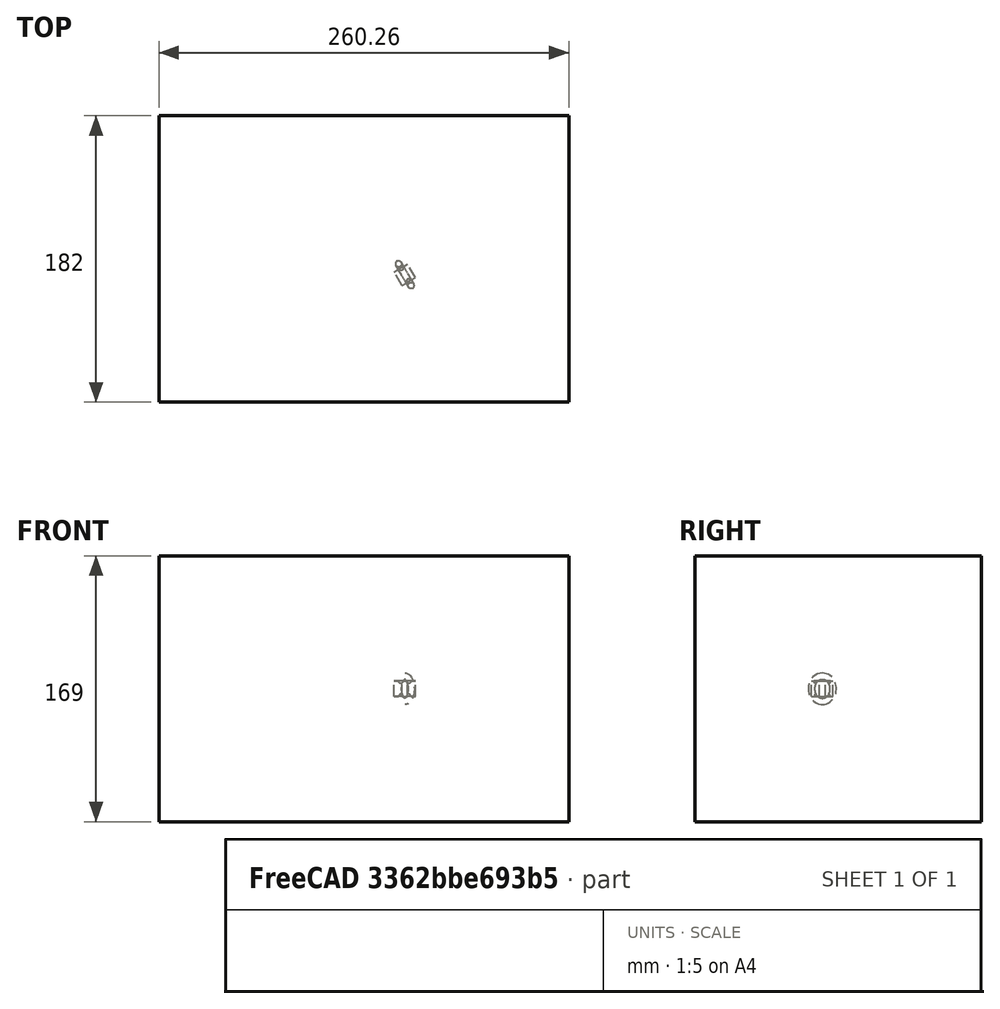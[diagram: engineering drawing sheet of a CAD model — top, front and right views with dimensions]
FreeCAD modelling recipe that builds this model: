
FCSTD DOCUMENT  (FreeCAD 0.21R33694 (Git))
Label: polarArray-7-Base-rotated-translated
License: All rights reserved
objects: App::DocumentObjectGroupPython×1251, Part::FeaturePython×4, App::Part×2, Part::MultiFuse×1
note: 4 computed .brp shape members not serialized (recipe doc carries the construction recipe); baked Part::Feature solids carry a one-line shape summary decoded from their .brp

FEATURE [App::DocumentObjectGroupPython] HALFPI  # scripted group (container) (typed FeaturePython)
  name = HALFPI
  value = pi/2.
FEATURE [App::DocumentObjectGroupPython] PI  # scripted group (container) (typed FeaturePython)
  name = PI
  value = 1.*pi
FEATURE [App::DocumentObjectGroupPython] TWOPI  # scripted group (container) (typed FeaturePython)
  name = TWOPI
  value = 2.*pi
FEATURE [App::DocumentObjectGroupPython] Constants  # scripted group (container) (typed FeaturePython)
  Group = -> [HALFPI,PI,TWOPI]
FEATURE [App::DocumentObjectGroupPython] Variables  # scripted group (container) (typed FeaturePython)
FEATURE [App::DocumentObjectGroupPython] Quantities  # scripted group (container) (typed FeaturePython)
FEATURE [App::DocumentObjectGroupPython] Isotopes  # scripted group (container) (typed FeaturePython)
FEATURE [App::DocumentObjectGroupPython] Elements  # scripted group (container) (typed FeaturePython)
FEATURE [App::DocumentObjectGroupPython] Matrix  # scripted group (container) (typed FeaturePython)
FEATURE [App::DocumentObjectGroupPython] Surfaces  # scripted group (container) (typed FeaturePython)
FEATURE [App::DocumentObjectGroupPython] Opticals  # scripted group (container) (typed FeaturePython)
  Group = -> [Matrix,Surfaces]
FEATURE [App::DocumentObjectGroupPython] G4Isotopes  # scripted group (container) (typed FeaturePython)
FEATURE [App::DocumentObjectGroupPython] H_element  # scripted group (container) (typed FeaturePython)
  Z = 1
  atom_value = 1.008
  formula = H
  name = H_element
FEATURE [App::DocumentObjectGroupPython] He_element  # scripted group (container) (typed FeaturePython)
  Z = 2
  atom_value = 4.0026
  formula = He
  name = He_element
FEATURE [App::DocumentObjectGroupPython] Li_element  # scripted group (container) (typed FeaturePython)
  Z = 3
  atom_value = 6.94
  formula = Li
  name = Li_element
FEATURE [App::DocumentObjectGroupPython] Be_element  # scripted group (container) (typed FeaturePython)
  Z = 4
  atom_value = 9.01218
  formula = Be
  name = Be_element
FEATURE [App::DocumentObjectGroupPython] B_element  # scripted group (container) (typed FeaturePython)
  Z = 5
  atom_value = 10.81
  formula = B
  name = B_element
FEATURE [App::DocumentObjectGroupPython] C_element  # scripted group (container) (typed FeaturePython)
  Z = 6
  atom_value = 12.011
  formula = C
  name = C_element
FEATURE [App::DocumentObjectGroupPython] N_element  # scripted group (container) (typed FeaturePython)
  Z = 7
  atom_value = 14.007
  formula = N
  name = N_element
FEATURE [App::DocumentObjectGroupPython] O_element  # scripted group (container) (typed FeaturePython)
  Z = 8
  atom_value = 15.999
  formula = O
  name = O_element
FEATURE [App::DocumentObjectGroupPython] F_element  # scripted group (container) (typed FeaturePython)
  Z = 9
  atom_value = 18.9984
  formula = F
  name = F_element
FEATURE [App::DocumentObjectGroupPython] Ne_element  # scripted group (container) (typed FeaturePython)
  Z = 10
  atom_value = 20.1797
  formula = Ne
  name = Ne_element
FEATURE [App::DocumentObjectGroupPython] Na_element  # scripted group (container) (typed FeaturePython)
  Z = 11
  atom_value = 22.9898
  formula = Na
  name = Na_element
FEATURE [App::DocumentObjectGroupPython] Mg_element  # scripted group (container) (typed FeaturePython)
  Z = 12
  atom_value = 24.305
  formula = Mg
  name = Mg_element
FEATURE [App::DocumentObjectGroupPython] Al_element  # scripted group (container) (typed FeaturePython)
  Z = 13
  atom_value = 26.9815
  formula = Al
  name = Al_element
FEATURE [App::DocumentObjectGroupPython] Si_element  # scripted group (container) (typed FeaturePython)
  Z = 14
  atom_value = 28.085
  formula = Si
  name = Si_element
FEATURE [App::DocumentObjectGroupPython] P_element  # scripted group (container) (typed FeaturePython)
  Z = 15
  atom_value = 30.9738
  formula = P
  name = P_element
FEATURE [App::DocumentObjectGroupPython] S_element  # scripted group (container) (typed FeaturePython)
  Z = 16
  atom_value = 32.06
  formula = S
  name = S_element
FEATURE [App::DocumentObjectGroupPython] Cl_element  # scripted group (container) (typed FeaturePython)
  Z = 17
  atom_value = 35.45
  formula = Cl
  name = Cl_element
FEATURE [App::DocumentObjectGroupPython] Ar_element  # scripted group (container) (typed FeaturePython)
  Z = 18
  atom_value = 39.95
  formula = Ar
  name = Ar_element
FEATURE [App::DocumentObjectGroupPython] K_element  # scripted group (container) (typed FeaturePython)
  Z = 19
  atom_value = 39.0983
  formula = K
  name = K_element
FEATURE [App::DocumentObjectGroupPython] Ca_element  # scripted group (container) (typed FeaturePython)
  Z = 20
  atom_value = 40.078
  formula = Ca
  name = Ca_element
FEATURE [App::DocumentObjectGroupPython] Sc_element  # scripted group (container) (typed FeaturePython)
  Z = 21
  atom_value = 44.9559
  formula = Sc
  name = Sc_element
FEATURE [App::DocumentObjectGroupPython] Ti_element  # scripted group (container) (typed FeaturePython)
  Z = 22
  atom_value = 47.867
  formula = Ti
  name = Ti_element
FEATURE [App::DocumentObjectGroupPython] V_element  # scripted group (container) (typed FeaturePython)
  Z = 23
  atom_value = 50.9415
  formula = V
  name = V_element
FEATURE [App::DocumentObjectGroupPython] Cr_element  # scripted group (container) (typed FeaturePython)
  Z = 24
  atom_value = 51.9961
  formula = Cr
  name = Cr_element
FEATURE [App::DocumentObjectGroupPython] Mn_element  # scripted group (container) (typed FeaturePython)
  Z = 25
  atom_value = 54.938
  formula = Mn
  name = Mn_element
FEATURE [App::DocumentObjectGroupPython] Fe_element  # scripted group (container) (typed FeaturePython)
  Z = 26
  atom_value = 55.845
  formula = Fe
  name = Fe_element
FEATURE [App::DocumentObjectGroupPython] Co_element  # scripted group (container) (typed FeaturePython)
  Z = 27
  atom_value = 58.9332
  formula = Co
  name = Co_element
FEATURE [App::DocumentObjectGroupPython] Ni_element  # scripted group (container) (typed FeaturePython)
  Z = 28
  atom_value = 58.6934
  formula = Ni
  name = Ni_element
FEATURE [App::DocumentObjectGroupPython] Cu_element  # scripted group (container) (typed FeaturePython)
  Z = 29
  atom_value = 63.546
  formula = Cu
  name = Cu_element
FEATURE [App::DocumentObjectGroupPython] Zn_element  # scripted group (container) (typed FeaturePython)
  Z = 30
  atom_value = 65.38
  formula = Zn
  name = Zn_element
FEATURE [App::DocumentObjectGroupPython] Ga_element  # scripted group (container) (typed FeaturePython)
  Z = 31
  atom_value = 69.723
  formula = Ga
  name = Ga_element
FEATURE [App::DocumentObjectGroupPython] Ge_element  # scripted group (container) (typed FeaturePython)
  Z = 32
  atom_value = 72.63
  formula = Ge
  name = Ge_element
FEATURE [App::DocumentObjectGroupPython] As_element  # scripted group (container) (typed FeaturePython)
  Z = 33
  atom_value = 74.9216
  formula = As
  name = As_element
FEATURE [App::DocumentObjectGroupPython] Se_element  # scripted group (container) (typed FeaturePython)
  Z = 34
  atom_value = 78.971
  formula = Se
  name = Se_element
FEATURE [App::DocumentObjectGroupPython] Br_element  # scripted group (container) (typed FeaturePython)
  Z = 35
  atom_value = 79.904
  formula = Br
  name = Br_element
FEATURE [App::DocumentObjectGroupPython] Kr_element  # scripted group (container) (typed FeaturePython)
  Z = 36
  atom_value = 83.798
  formula = Kr
  name = Kr_element
FEATURE [App::DocumentObjectGroupPython] Rb_element  # scripted group (container) (typed FeaturePython)
  Z = 37
  atom_value = 85.4678
  formula = Rb
  name = Rb_element
FEATURE [App::DocumentObjectGroupPython] Sr_element  # scripted group (container) (typed FeaturePython)
  Z = 38
  atom_value = 87.62
  formula = Sr
  name = Sr_element
FEATURE [App::DocumentObjectGroupPython] Y_element  # scripted group (container) (typed FeaturePython)
  Z = 39
  atom_value = 88.9058
  formula = Y
  name = Y_element
FEATURE [App::DocumentObjectGroupPython] Zr_element  # scripted group (container) (typed FeaturePython)
  Z = 40
  atom_value = 91.224
  formula = Zr
  name = Zr_element
FEATURE [App::DocumentObjectGroupPython] Nb_element  # scripted group (container) (typed FeaturePython)
  Z = 41
  atom_value = 92.9064
  formula = Nb
  name = Nb_element
FEATURE [App::DocumentObjectGroupPython] Mo_element  # scripted group (container) (typed FeaturePython)
  Z = 42
  atom_value = 95.95
  formula = Mo
  name = Mo_element
FEATURE [App::DocumentObjectGroupPython] Tc_element  # scripted group (container) (typed FeaturePython)
  Z = 43
  atom_value = 97
  formula = Tc
  name = Tc_element
FEATURE [App::DocumentObjectGroupPython] Ru_element  # scripted group (container) (typed FeaturePython)
  Z = 44
  atom_value = 101.07
  formula = Ru
  name = Ru_element
FEATURE [App::DocumentObjectGroupPython] Rh_element  # scripted group (container) (typed FeaturePython)
  Z = 45
  atom_value = 102.905
  formula = Rh
  name = Rh_element
FEATURE [App::DocumentObjectGroupPython] Pd_element  # scripted group (container) (typed FeaturePython)
  Z = 46
  atom_value = 106.42
  formula = Pd
  name = Pd_element
FEATURE [App::DocumentObjectGroupPython] Ag_element  # scripted group (container) (typed FeaturePython)
  Z = 47
  atom_value = 107.868
  formula = Ag
  name = Ag_element
FEATURE [App::DocumentObjectGroupPython] Cd_element  # scripted group (container) (typed FeaturePython)
  Z = 48
  atom_value = 112.414
  formula = Cd
  name = Cd_element
FEATURE [App::DocumentObjectGroupPython] In_element  # scripted group (container) (typed FeaturePython)
  Z = 49
  atom_value = 114.818
  formula = In
  name = In_element
FEATURE [App::DocumentObjectGroupPython] Sn_element  # scripted group (container) (typed FeaturePython)
  Z = 50
  atom_value = 118.71
  formula = Sn
  name = Sn_element
FEATURE [App::DocumentObjectGroupPython] Sb_element  # scripted group (container) (typed FeaturePython)
  Z = 51
  atom_value = 121.76
  formula = Sb
  name = Sb_element
FEATURE [App::DocumentObjectGroupPython] Te_element  # scripted group (container) (typed FeaturePython)
  Z = 52
  atom_value = 127.6
  formula = Te
  name = Te_element
FEATURE [App::DocumentObjectGroupPython] I_element  # scripted group (container) (typed FeaturePython)
  Z = 53
  atom_value = 126.904
  formula = I
  name = I_element
FEATURE [App::DocumentObjectGroupPython] Xe_element  # scripted group (container) (typed FeaturePython)
  Z = 54
  atom_value = 131.293
  formula = Xe
  name = Xe_element
FEATURE [App::DocumentObjectGroupPython] Cs_element  # scripted group (container) (typed FeaturePython)
  Z = 55
  atom_value = 132.905
  formula = Cs
  name = Cs_element
FEATURE [App::DocumentObjectGroupPython] Ba_element  # scripted group (container) (typed FeaturePython)
  Z = 56
  atom_value = 137.327
  formula = Ba
  name = Ba_element
FEATURE [App::DocumentObjectGroupPython] La_element  # scripted group (container) (typed FeaturePython)
  Z = 57
  atom_value = 138.905
  formula = La
  name = La_element
FEATURE [App::DocumentObjectGroupPython] Ce_element  # scripted group (container) (typed FeaturePython)
  Z = 58
  atom_value = 140.116
  formula = Ce
  name = Ce_element
FEATURE [App::DocumentObjectGroupPython] Pr_element  # scripted group (container) (typed FeaturePython)
  Z = 59
  atom_value = 140.908
  formula = Pr
  name = Pr_element
FEATURE [App::DocumentObjectGroupPython] Nd_element  # scripted group (container) (typed FeaturePython)
  Z = 60
  atom_value = 144.242
  formula = Nd
  name = Nd_element
FEATURE [App::DocumentObjectGroupPython] Pm_element  # scripted group (container) (typed FeaturePython)
  Z = 61
  atom_value = 145
  formula = Pm
  name = Pm_element
FEATURE [App::DocumentObjectGroupPython] Sm_element  # scripted group (container) (typed FeaturePython)
  Z = 62
  atom_value = 150.36
  formula = Sm
  name = Sm_element
FEATURE [App::DocumentObjectGroupPython] Eu_element  # scripted group (container) (typed FeaturePython)
  Z = 63
  atom_value = 151.964
  formula = Eu
  name = Eu_element
FEATURE [App::DocumentObjectGroupPython] Gd_element  # scripted group (container) (typed FeaturePython)
  Z = 64
  atom_value = 157.25
  formula = Gd
  name = Gd_element
FEATURE [App::DocumentObjectGroupPython] Tb_element  # scripted group (container) (typed FeaturePython)
  Z = 65
  atom_value = 158.925
  formula = Tb
  name = Tb_element
FEATURE [App::DocumentObjectGroupPython] Dy_element  # scripted group (container) (typed FeaturePython)
  Z = 66
  atom_value = 162.5
  formula = Dy
  name = Dy_element
FEATURE [App::DocumentObjectGroupPython] Ho_element  # scripted group (container) (typed FeaturePython)
  Z = 67
  atom_value = 164.93
  formula = Ho
  name = Ho_element
FEATURE [App::DocumentObjectGroupPython] Er_element  # scripted group (container) (typed FeaturePython)
  Z = 68
  atom_value = 167.259
  formula = Er
  name = Er_element
FEATURE [App::DocumentObjectGroupPython] Tm_element  # scripted group (container) (typed FeaturePython)
  Z = 69
  atom_value = 168.934
  formula = Tm
  name = Tm_element
FEATURE [App::DocumentObjectGroupPython] Yb_element  # scripted group (container) (typed FeaturePython)
  Z = 70
  atom_value = 173.045
  formula = Yb
  name = Yb_element
FEATURE [App::DocumentObjectGroupPython] Lu_element  # scripted group (container) (typed FeaturePython)
  Z = 71
  atom_value = 174.967
  formula = Lu
  name = Lu_element
FEATURE [App::DocumentObjectGroupPython] Hf_element  # scripted group (container) (typed FeaturePython)
  Z = 72
  atom_value = 178.49
  formula = Hf
  name = Hf_element
FEATURE [App::DocumentObjectGroupPython] Ta_element  # scripted group (container) (typed FeaturePython)
  Z = 73
  atom_value = 180.948
  formula = Ta
  name = Ta_element
FEATURE [App::DocumentObjectGroupPython] W_element  # scripted group (container) (typed FeaturePython)
  Z = 74
  atom_value = 183.84
  formula = W
  name = W_element
FEATURE [App::DocumentObjectGroupPython] Re_element  # scripted group (container) (typed FeaturePython)
  Z = 75
  atom_value = 186.207
  formula = Re
  name = Re_element
FEATURE [App::DocumentObjectGroupPython] Os_element  # scripted group (container) (typed FeaturePython)
  Z = 76
  atom_value = 190.23
  formula = Os
  name = Os_element
FEATURE [App::DocumentObjectGroupPython] Ir_element  # scripted group (container) (typed FeaturePython)
  Z = 77
  atom_value = 192.217
  formula = Ir
  name = Ir_element
FEATURE [App::DocumentObjectGroupPython] Pt_element  # scripted group (container) (typed FeaturePython)
  Z = 78
  atom_value = 195.084
  formula = Pt
  name = Pt_element
FEATURE [App::DocumentObjectGroupPython] Au_element  # scripted group (container) (typed FeaturePython)
  Z = 79
  atom_value = 196.967
  formula = Au
  name = Au_element
FEATURE [App::DocumentObjectGroupPython] Hg_element  # scripted group (container) (typed FeaturePython)
  Z = 80
  atom_value = 200.592
  formula = Hg
  name = Hg_element
FEATURE [App::DocumentObjectGroupPython] Tl_element  # scripted group (container) (typed FeaturePython)
  Z = 81
  atom_value = 204.38
  formula = Tl
  name = Tl_element
FEATURE [App::DocumentObjectGroupPython] Pb_element  # scripted group (container) (typed FeaturePython)
  Z = 82
  atom_value = 207.2
  formula = Pb
  name = Pb_element
FEATURE [App::DocumentObjectGroupPython] Bi_element  # scripted group (container) (typed FeaturePython)
  Z = 83
  atom_value = 208.98
  formula = Bi
  name = Bi_element
FEATURE [App::DocumentObjectGroupPython] Po_element  # scripted group (container) (typed FeaturePython)
  Z = 84
  atom_value = 209
  formula = Po
  name = Po_element
FEATURE [App::DocumentObjectGroupPython] At_element  # scripted group (container) (typed FeaturePython)
  Z = 85
  atom_value = 210
  formula = At
  name = At_element
FEATURE [App::DocumentObjectGroupPython] Rn_element  # scripted group (container) (typed FeaturePython)
  Z = 86
  atom_value = 222
  formula = Rn
  name = Rn_element
FEATURE [App::DocumentObjectGroupPython] Fr_element  # scripted group (container) (typed FeaturePython)
  Z = 87
  atom_value = 223
  formula = Fr
  name = Fr_element
FEATURE [App::DocumentObjectGroupPython] Ra_element  # scripted group (container) (typed FeaturePython)
  Z = 88
  atom_value = 226
  formula = Ra
  name = Ra_element
FEATURE [App::DocumentObjectGroupPython] Ac_element  # scripted group (container) (typed FeaturePython)
  Z = 89
  atom_value = 227
  formula = Ac
  name = Ac_element
FEATURE [App::DocumentObjectGroupPython] Th_element  # scripted group (container) (typed FeaturePython)
  Z = 90
  atom_value = 232.038
  formula = Th
  name = Th_element
FEATURE [App::DocumentObjectGroupPython] Pa_element  # scripted group (container) (typed FeaturePython)
  Z = 91
  atom_value = 231.036
  formula = Pa
  name = Pa_element
FEATURE [App::DocumentObjectGroupPython] U_element  # scripted group (container) (typed FeaturePython)
  Z = 92
  atom_value = 238.029
  formula = U
  name = U_element
FEATURE [App::DocumentObjectGroupPython] Np_element  # scripted group (container) (typed FeaturePython)
  Z = 93
  atom_value = 237
  formula = Np
  name = Np_element
FEATURE [App::DocumentObjectGroupPython] Pu_element  # scripted group (container) (typed FeaturePython)
  Z = 94
  atom_value = 244
  formula = Pu
  name = Pu_element
FEATURE [App::DocumentObjectGroupPython] Am_element  # scripted group (container) (typed FeaturePython)
  Z = 95
  atom_value = 243
  formula = Am
  name = Am_element
FEATURE [App::DocumentObjectGroupPython] Cm_element  # scripted group (container) (typed FeaturePython)
  Z = 96
  atom_value = 247
  formula = Cm
  name = Cm_element
FEATURE [App::DocumentObjectGroupPython] Bk_element  # scripted group (container) (typed FeaturePython)
  Z = 97
  atom_value = 247
  formula = Bk
  name = Bk_element
FEATURE [App::DocumentObjectGroupPython] Cf_element  # scripted group (container) (typed FeaturePython)
  Z = 98
  atom_value = 251
  formula = Cf
  name = Cf_element
FEATURE [App::DocumentObjectGroupPython] G4Elements  # scripted group (container) (typed FeaturePython)
  Group = -> [H_element,He_element,Li_element,Be_element,B_element,C_element,N_element,O_element,F_element,Ne_element,Na_element,Mg_element,Al_element,Si_element,P_element,S_element,Cl_element,Ar_element,K_element,Ca_element,Sc_element,Ti_element,V_element,Cr_element,Mn_element,Fe_element,Co_element,Ni_element,Cu_element,Zn_element,Ga_element,Ge_element,As_element,Se_element,Br_element,Kr_element,Rb_element,+61 more]
FEATURE [App::DocumentObjectGroupPython] H_element001  label="H_element : 0.101"  # scripted group (container) (typed FeaturePython)
  n = 0.101327
FEATURE [App::DocumentObjectGroupPython] C_element001  label="C_element : 0.775"  # scripted group (container) (typed FeaturePython)
  n = 0.7755
FEATURE [App::DocumentObjectGroupPython] N_element001  label="N_element : 0.035"  # scripted group (container) (typed FeaturePython)
  n = 0.035057
FEATURE [App::DocumentObjectGroupPython] O_element001  label="O_element : 0.052"  # scripted group (container) (typed FeaturePython)
  n = 0.0523159
FEATURE [App::DocumentObjectGroupPython] F_element001  label="F_element : 0.017"  # scripted group (container) (typed FeaturePython)
  n = 0.017422
FEATURE [App::DocumentObjectGroupPython] Ca_element001  label="Ca_element : 0.018"  # scripted group (container) (typed FeaturePython)
  n = 0.018378
FEATURE [App::DocumentObjectGroupPython] G4_A_150_TISSUE  label="G4_A-150_TISSUE"  # scripted group (container) (typed FeaturePython)
  Dunit = g/cm3
  Dvalue = 1.127
  Group = -> [H_element001,C_element001,N_element001,O_element001,F_element001,Ca_element001]
  conduct = 2
  density = 1
  expand = 3
  formula = G4_A-150_TISSUE
  name = G4_A-150_TISSUE
  specific = 4
FEATURE [App::DocumentObjectGroupPython] C_element002  label="C_element : 3"  # scripted group (container) (typed FeaturePython)
  n = 3
  ref = C_element
FEATURE [App::DocumentObjectGroupPython] H_element002  label="H_element : 6"  # scripted group (container) (typed FeaturePython)
  n = 6
  ref = H_element
FEATURE [App::DocumentObjectGroupPython] O_element002  label="O_element : 1"  # scripted group (container) (typed FeaturePython)
  n = 1
  ref = O_element
FEATURE [App::DocumentObjectGroupPython] G4_ACETONE  # scripted group (container) (typed FeaturePython)
  Dunit = g/cm3
  Dvalue = 0.7899
  Group = -> [C_element002,H_element002,O_element002]
  conduct = 2
  density = 1
  expand = 3
  formula = G4_ACETONE
  name = G4_ACETONE
  specific = 4
FEATURE [App::DocumentObjectGroupPython] C_element003  label="C_element : 2"  # scripted group (container) (typed FeaturePython)
  n = 2
  ref = C_element
FEATURE [App::DocumentObjectGroupPython] H_element003  label="H_element : 2"  # scripted group (container) (typed FeaturePython)
  n = 2
  ref = H_element
FEATURE [App::DocumentObjectGroupPython] G4_ACETYLENE  # scripted group (container) (typed FeaturePython)
  Dunit = g/cm3
  Dvalue = 0.0010967
  Group = -> [C_element003,H_element003]
  conduct = 2
  density = 1
  expand = 3
  formula = G4_ACETYLENE
  name = G4_ACETYLENE
  specific = 4
FEATURE [App::DocumentObjectGroupPython] C_element004  label="C_element : 5"  # scripted group (container) (typed FeaturePython)
  n = 5
  ref = C_element
FEATURE [App::DocumentObjectGroupPython] H_element004  label="H_element : 5"  # scripted group (container) (typed FeaturePython)
  n = 5
  ref = H_element
FEATURE [App::DocumentObjectGroupPython] N_element002  label="N_element : 5"  # scripted group (container) (typed FeaturePython)
  n = 5
  ref = N_element
FEATURE [App::DocumentObjectGroupPython] G4_ADENINE  # scripted group (container) (typed FeaturePython)
  Dunit = g/cm3
  Dvalue = 1.6
  Group = -> [C_element004,H_element004,N_element002]
  conduct = 2
  density = 1
  expand = 3
  formula = G4_ADENINE
  name = G4_ADENINE
  specific = 4
FEATURE [App::DocumentObjectGroupPython] H_element005  label="H_element : 0.114"  # scripted group (container) (typed FeaturePython)
  n = 0.114
FEATURE [App::DocumentObjectGroupPython] C_element005  label="C_element : 0.598"  # scripted group (container) (typed FeaturePython)
  n = 0.598
FEATURE [App::DocumentObjectGroupPython] N_element003  label="N_element : 0.007"  # scripted group (container) (typed FeaturePython)
  n = 0.007
FEATURE [App::DocumentObjectGroupPython] O_element003  label="O_element : 0.278"  # scripted group (container) (typed FeaturePython)
  n = 0.278
FEATURE [App::DocumentObjectGroupPython] Na_element001  label="Na_element : 0.001"  # scripted group (container) (typed FeaturePython)
  n = 0.001
FEATURE [App::DocumentObjectGroupPython] S_element001  label="S_element : 0.001"  # scripted group (container) (typed FeaturePython)
  n = 0.001
FEATURE [App::DocumentObjectGroupPython] Cl_element001  label="Cl_element : 0.001"  # scripted group (container) (typed FeaturePython)
  n = 0.001
FEATURE [App::DocumentObjectGroupPython] G4_ADIPOSE_TISSUE_ICRP  # scripted group (container) (typed FeaturePython)
  Dunit = g/cm3
  Dvalue = 0.95
  Group = -> [H_element005,C_element005,N_element003,O_element003,Na_element001,S_element001,Cl_element001]
  conduct = 2
  density = 1
  expand = 3
  formula = G4_ADIPOSE_TISSUE_ICRP
  name = G4_ADIPOSE_TISSUE_ICRP
  specific = 4
FEATURE [App::DocumentObjectGroupPython] C_element006  label="C_element : 0.000"  # scripted group (container) (typed FeaturePython)
  n = 0.000124
FEATURE [App::DocumentObjectGroupPython] N_element004  label="N_element : 0.755"  # scripted group (container) (typed FeaturePython)
  n = 0.755268
FEATURE [App::DocumentObjectGroupPython] O_element004  label="O_element : 0.232"  # scripted group (container) (typed FeaturePython)
  n = 0.231781
FEATURE [App::DocumentObjectGroupPython] Ar_element001  label="Ar_element : 0.013"  # scripted group (container) (typed FeaturePython)
  n = 0.012827
FEATURE [App::DocumentObjectGroupPython] G4_AIR  # scripted group (container) (typed FeaturePython)
  Dunit = g/cm3
  Dvalue = 0.00120479
  Group = -> [C_element006,N_element004,O_element004,Ar_element001]
  conduct = 2
  density = 1
  expand = 3
  formula = G4_AIR
  name = G4_AIR
  specific = 4
FEATURE [App::DocumentObjectGroupPython] C_element007  label="C_element : 006"  # scripted group (container) (typed FeaturePython)
  n = 3
  ref = C_element
FEATURE [App::DocumentObjectGroupPython] H_element006  label="H_element : 7"  # scripted group (container) (typed FeaturePython)
  n = 7
  ref = H_element
FEATURE [App::DocumentObjectGroupPython] N_element005  label="N_element : 1"  # scripted group (container) (typed FeaturePython)
  n = 1
  ref = N_element
FEATURE [App::DocumentObjectGroupPython] O_element005  label="O_element : 2"  # scripted group (container) (typed FeaturePython)
  n = 2
  ref = O_element
FEATURE [App::DocumentObjectGroupPython] G4_ALANINE  # scripted group (container) (typed FeaturePython)
  Dunit = g/cm3
  Dvalue = 1.42
  Group = -> [C_element007,H_element006,N_element005,O_element005]
  conduct = 2
  density = 1
  expand = 3
  formula = G4_ALANINE
  name = G4_ALANINE
  specific = 4
FEATURE [App::DocumentObjectGroupPython] Al_element001  label="Al_element : 2"  # scripted group (container) (typed FeaturePython)
  n = 2
  ref = Al_element
FEATURE [App::DocumentObjectGroupPython] O_element006  label="O_element : 3"  # scripted group (container) (typed FeaturePython)
  n = 3
  ref = O_element
FEATURE [App::DocumentObjectGroupPython] G4_ALUMINUM_OXIDE  # scripted group (container) (typed FeaturePython)
  Dunit = g/cm3
  Dvalue = 3.97
  Group = -> [Al_element001,O_element006]
  conduct = 2
  density = 1
  expand = 3
  formula = G4_ALUMINUM_OXIDE
  name = G4_ALUMINUM_OXIDE
  specific = 4
FEATURE [App::DocumentObjectGroupPython] H_element007  label="H_element : 0.106"  # scripted group (container) (typed FeaturePython)
  n = 0.10593
FEATURE [App::DocumentObjectGroupPython] C_element008  label="C_element : 0.789"  # scripted group (container) (typed FeaturePython)
  n = 0.788974
FEATURE [App::DocumentObjectGroupPython] O_element007  label="O_element : 0.105"  # scripted group (container) (typed FeaturePython)
  n = 0.105096
FEATURE [App::DocumentObjectGroupPython] G4_AMBER  # scripted group (container) (typed FeaturePython)
  Dunit = g/cm3
  Dvalue = 1.1
  Group = -> [H_element007,C_element008,O_element007]
  conduct = 2
  density = 1
  expand = 3
  formula = G4_AMBER
  name = G4_AMBER
  specific = 4
FEATURE [App::DocumentObjectGroupPython] N_element006  label="N_element : 006"  # scripted group (container) (typed FeaturePython)
  n = 1
  ref = N_element
FEATURE [App::DocumentObjectGroupPython] H_element008  label="H_element : 3"  # scripted group (container) (typed FeaturePython)
  n = 3
  ref = H_element
FEATURE [App::DocumentObjectGroupPython] G4_AMMONIA  # scripted group (container) (typed FeaturePython)
  Dunit = g/cm3
  Dvalue = 0.000826019
  Group = -> [N_element006,H_element008]
  conduct = 2
  density = 1
  expand = 3
  formula = G4_AMMONIA
  name = G4_AMMONIA
  specific = 4
FEATURE [App::DocumentObjectGroupPython] C_element009  label="C_element : 6"  # scripted group (container) (typed FeaturePython)
  n = 6
  ref = C_element
FEATURE [App::DocumentObjectGroupPython] H_element009  label="H_element : 008"  # scripted group (container) (typed FeaturePython)
  n = 7
  ref = H_element
FEATURE [App::DocumentObjectGroupPython] N_element007  label="N_element : 007"  # scripted group (container) (typed FeaturePython)
  n = 1
  ref = N_element
FEATURE [App::DocumentObjectGroupPython] G4_ANILINE  # scripted group (container) (typed FeaturePython)
  Dunit = g/cm3
  Dvalue = 1.0235
  Group = -> [C_element009,H_element009,N_element007]
  conduct = 2
  density = 1
  expand = 3
  formula = G4_ANILINE
  name = G4_ANILINE
  specific = 4
FEATURE [App::DocumentObjectGroupPython] C_element010  label="C_element : 14"  # scripted group (container) (typed FeaturePython)
  n = 14
  ref = C_element
FEATURE [App::DocumentObjectGroupPython] H_element010  label="H_element : 10"  # scripted group (container) (typed FeaturePython)
  n = 10
  ref = H_element
FEATURE [App::DocumentObjectGroupPython] G4_ANTHRACENE  # scripted group (container) (typed FeaturePython)
  Dunit = g/cm3
  Dvalue = 1.283
  Group = -> [C_element010,H_element010]
  conduct = 2
  density = 1
  expand = 3
  formula = G4_ANTHRACENE
  name = G4_ANTHRACENE
  specific = 4
FEATURE [App::DocumentObjectGroupPython] H_element011  label="H_element : 0.065"  # scripted group (container) (typed FeaturePython)
  n = 0.0654709
FEATURE [App::DocumentObjectGroupPython] C_element011  label="C_element : 0.537"  # scripted group (container) (typed FeaturePython)
  n = 0.536944
FEATURE [App::DocumentObjectGroupPython] N_element008  label="N_element : 0.021"  # scripted group (container) (typed FeaturePython)
  n = 0.0215
FEATURE [App::DocumentObjectGroupPython] O_element008  label="O_element : 0.032"  # scripted group (container) (typed FeaturePython)
  n = 0.032085
FEATURE [App::DocumentObjectGroupPython] F_element002  label="F_element : 0.167"  # scripted group (container) (typed FeaturePython)
  n = 0.167411
FEATURE [App::DocumentObjectGroupPython] Ca_element002  label="Ca_element : 0.177"  # scripted group (container) (typed FeaturePython)
  n = 0.176589
FEATURE [App::DocumentObjectGroupPython] G4_B_100_BONE  label="G4_B-100_BONE"  # scripted group (container) (typed FeaturePython)
  Dunit = g/cm3
  Dvalue = 1.45
  Group = -> [H_element011,C_element011,N_element008,O_element008,F_element002,Ca_element002]
  conduct = 2
  density = 1
  expand = 3
  formula = G4_B-100_BONE
  name = G4_B-100_BONE
  specific = 4
FEATURE [App::DocumentObjectGroupPython] H_element012  label="H_element : 0.057"  # scripted group (container) (typed FeaturePython)
  n = 0.057441
FEATURE [App::DocumentObjectGroupPython] C_element012  label="C_element : 0.790"  # scripted group (container) (typed FeaturePython)
  n = 0.774591
FEATURE [App::DocumentObjectGroupPython] O_element009  label="O_element : 0.168"  # scripted group (container) (typed FeaturePython)
  n = 0.167968
FEATURE [App::DocumentObjectGroupPython] G4_BAKELITE  # scripted group (container) (typed FeaturePython)
  Dunit = g/cm3
  Dvalue = 1.25
  Group = -> [H_element012,C_element012,O_element009]
  conduct = 2
  density = 1
  expand = 3
  formula = G4_BAKELITE
  name = G4_BAKELITE
  specific = 4
FEATURE [App::DocumentObjectGroupPython] Ba_element001  label="Ba_element : 1"  # scripted group (container) (typed FeaturePython)
  n = 1
  ref = Ba_element
FEATURE [App::DocumentObjectGroupPython] F_element003  label="F_element : 2"  # scripted group (container) (typed FeaturePython)
  n = 2
  ref = F_element
FEATURE [App::DocumentObjectGroupPython] G4_BARIUM_FLUORIDE  # scripted group (container) (typed FeaturePython)
  Dunit = g/cm3
  Dvalue = 4.89
  Group = -> [Ba_element001,F_element003]
  conduct = 2
  density = 1
  expand = 3
  formula = G4_BARIUM_FLUORIDE
  name = G4_BARIUM_FLUORIDE
  specific = 4
FEATURE [App::DocumentObjectGroupPython] Ba_element002  label="Ba_element : 002"  # scripted group (container) (typed FeaturePython)
  n = 1
  ref = Ba_element
FEATURE [App::DocumentObjectGroupPython] S_element002  label="S_element : 1"  # scripted group (container) (typed FeaturePython)
  n = 1
  ref = S_element
FEATURE [App::DocumentObjectGroupPython] O_element010  label="O_element : 4"  # scripted group (container) (typed FeaturePython)
  n = 4
  ref = O_element
FEATURE [App::DocumentObjectGroupPython] G4_BARIUM_SULFATE  # scripted group (container) (typed FeaturePython)
  Dunit = g/cm3
  Dvalue = 4.5
  Group = -> [Ba_element002,S_element002,O_element010]
  conduct = 2
  density = 1
  expand = 3
  formula = G4_BARIUM_SULFATE
  name = G4_BARIUM_SULFATE
  specific = 4
FEATURE [App::DocumentObjectGroupPython] C_element013  label="C_element : 007"  # scripted group (container) (typed FeaturePython)
  n = 6
  ref = C_element
FEATURE [App::DocumentObjectGroupPython] H_element013  label="H_element : 009"  # scripted group (container) (typed FeaturePython)
  n = 6
  ref = H_element
FEATURE [App::DocumentObjectGroupPython] G4_BENZENE  # scripted group (container) (typed FeaturePython)
  Dunit = g/cm3
  Dvalue = 0.87865
  Group = -> [C_element013,H_element013]
  conduct = 2
  density = 1
  expand = 3
  formula = G4_BENZENE
  name = G4_BENZENE
  specific = 4
FEATURE [App::DocumentObjectGroupPython] Be_element001  label="Be_element : 1"  # scripted group (container) (typed FeaturePython)
  n = 1
  ref = Be_element
FEATURE [App::DocumentObjectGroupPython] O_element011  label="O_element : 005"  # scripted group (container) (typed FeaturePython)
  n = 1
  ref = O_element
FEATURE [App::DocumentObjectGroupPython] G4_BERYLLIUM_OXIDE  # scripted group (container) (typed FeaturePython)
  Dunit = g/cm3
  Dvalue = 3.01
  Group = -> [Be_element001,O_element011]
  conduct = 2
  density = 1
  expand = 3
  formula = G4_BERYLLIUM_OXIDE
  name = G4_BERYLLIUM_OXIDE
  specific = 4
FEATURE [App::DocumentObjectGroupPython] Bi_element001  label="Bi_element : 4"  # scripted group (container) (typed FeaturePython)
  n = 4
  ref = Bi_element
FEATURE [App::DocumentObjectGroupPython] Ge_element001  label="Ge_element : 3"  # scripted group (container) (typed FeaturePython)
  n = 3
  ref = Ge_element
FEATURE [App::DocumentObjectGroupPython] O_element012  label="O_element : 12"  # scripted group (container) (typed FeaturePython)
  n = 12
  ref = O_element
FEATURE [App::DocumentObjectGroupPython] G4_BGO  # scripted group (container) (typed FeaturePython)
  Dunit = g/cm3
  Dvalue = 7.13
  Group = -> [Bi_element001,Ge_element001,O_element012]
  conduct = 2
  density = 1
  expand = 3
  formula = G4_BGO
  name = G4_BGO
  specific = 4
FEATURE [App::DocumentObjectGroupPython] H_element014  label="H_element : 0.102"  # scripted group (container) (typed FeaturePython)
  n = 0.102
FEATURE [App::DocumentObjectGroupPython] C_element014  label="C_element : 0.110"  # scripted group (container) (typed FeaturePython)
  n = 0.11
FEATURE [App::DocumentObjectGroupPython] N_element009  label="N_element : 0.033"  # scripted group (container) (typed FeaturePython)
  n = 0.033
FEATURE [App::DocumentObjectGroupPython] O_element013  label="O_element : 0.745"  # scripted group (container) (typed FeaturePython)
  n = 0.745
FEATURE [App::DocumentObjectGroupPython] Na_element002  label="Na_element : 0.002"  # scripted group (container) (typed FeaturePython)
  n = 0.001
FEATURE [App::DocumentObjectGroupPython] P_element001  label="P_element : 0.001"  # scripted group (container) (typed FeaturePython)
  n = 0.001
FEATURE [App::DocumentObjectGroupPython] S_element003  label="S_element : 0.002"  # scripted group (container) (typed FeaturePython)
  n = 0.002
FEATURE [App::DocumentObjectGroupPython] Cl_element002  label="Cl_element : 0.003"  # scripted group (container) (typed FeaturePython)
  n = 0.003
FEATURE [App::DocumentObjectGroupPython] K_element001  label="K_element : 0.002"  # scripted group (container) (typed FeaturePython)
  n = 0.002
FEATURE [App::DocumentObjectGroupPython] Fe_element001  label="Fe_element : 0.001"  # scripted group (container) (typed FeaturePython)
  n = 0.001
FEATURE [App::DocumentObjectGroupPython] G4_BLOOD_ICRP  # scripted group (container) (typed FeaturePython)
  Dunit = g/cm3
  Dvalue = 1.06
  Group = -> [H_element014,C_element014,N_element009,O_element013,Na_element002,P_element001,S_element003,Cl_element002,K_element001,Fe_element001]
  conduct = 2
  density = 1
  expand = 3
  formula = G4_BLOOD_ICRP
  name = G4_BLOOD_ICRP
  specific = 4
FEATURE [App::DocumentObjectGroupPython] H_element015  label="H_element : 0.064"  # scripted group (container) (typed FeaturePython)
  n = 0.064
FEATURE [App::DocumentObjectGroupPython] C_element015  label="C_element : 0.278"  # scripted group (container) (typed FeaturePython)
  n = 0.278
FEATURE [App::DocumentObjectGroupPython] N_element010  label="N_element : 0.027"  # scripted group (container) (typed FeaturePython)
  n = 0.027
FEATURE [App::DocumentObjectGroupPython] O_element014  label="O_element : 0.410"  # scripted group (container) (typed FeaturePython)
  n = 0.41
FEATURE [App::DocumentObjectGroupPython] Mg_element001  label="Mg_element : 0.002"  # scripted group (container) (typed FeaturePython)
  n = 0.002
FEATURE [App::DocumentObjectGroupPython] P_element002  label="P_element : 0.070"  # scripted group (container) (typed FeaturePython)
  n = 0.07
FEATURE [App::DocumentObjectGroupPython] S_element004  label="S_element : 0.003"  # scripted group (container) (typed FeaturePython)
  n = 0.002
FEATURE [App::DocumentObjectGroupPython] Ca_element003  label="Ca_element : 0.147"  # scripted group (container) (typed FeaturePython)
  n = 0.147
FEATURE [App::DocumentObjectGroupPython] G4_BONE_COMPACT_ICRU  # scripted group (container) (typed FeaturePython)
  Dunit = g/cm3
  Dvalue = 1.85
  Group = -> [H_element015,C_element015,N_element010,O_element014,Mg_element001,P_element002,S_element004,Ca_element003]
  conduct = 2
  density = 1
  expand = 3
  formula = G4_BONE_COMPACT_ICRU
  name = G4_BONE_COMPACT_ICRU
  specific = 4
FEATURE [App::DocumentObjectGroupPython] H_element016  label="H_element : 0.034"  # scripted group (container) (typed FeaturePython)
  n = 0.034
FEATURE [App::DocumentObjectGroupPython] C_element016  label="C_element : 0.155"  # scripted group (container) (typed FeaturePython)
  n = 0.155
FEATURE [App::DocumentObjectGroupPython] N_element011  label="N_element : 0.042"  # scripted group (container) (typed FeaturePython)
  n = 0.042
FEATURE [App::DocumentObjectGroupPython] O_element015  label="O_element : 0.435"  # scripted group (container) (typed FeaturePython)
  n = 0.435
FEATURE [App::DocumentObjectGroupPython] Na_element003  label="Na_element : 0.003"  # scripted group (container) (typed FeaturePython)
  n = 0.001
FEATURE [App::DocumentObjectGroupPython] Mg_element002  label="Mg_element : 0.003"  # scripted group (container) (typed FeaturePython)
  n = 0.002
FEATURE [App::DocumentObjectGroupPython] P_element003  label="P_element : 0.103"  # scripted group (container) (typed FeaturePython)
  n = 0.103
FEATURE [App::DocumentObjectGroupPython] S_element005  label="S_element : 0.004"  # scripted group (container) (typed FeaturePython)
  n = 0.003
FEATURE [App::DocumentObjectGroupPython] Ca_element004  label="Ca_element : 0.225"  # scripted group (container) (typed FeaturePython)
  n = 0.225
FEATURE [App::DocumentObjectGroupPython] G4_BONE_CORTICAL_ICRP  # scripted group (container) (typed FeaturePython)
  Dunit = g/cm3
  Dvalue = 1.92
  Group = -> [H_element016,C_element016,N_element011,O_element015,Na_element003,Mg_element002,P_element003,S_element005,Ca_element004]
  conduct = 2
  density = 1
  expand = 3
  formula = G4_BONE_CORTICAL_ICRP
  name = G4_BONE_CORTICAL_ICRP
  specific = 4
FEATURE [App::DocumentObjectGroupPython] B_element001  label="B_element : 4"  # scripted group (container) (typed FeaturePython)
  n = 4
  ref = B_element
FEATURE [App::DocumentObjectGroupPython] C_element017  label="C_element : 1"  # scripted group (container) (typed FeaturePython)
  n = 1
  ref = C_element
FEATURE [App::DocumentObjectGroupPython] G4_BORON_CARBIDE  # scripted group (container) (typed FeaturePython)
  Dunit = g/cm3
  Dvalue = 2.52
  Group = -> [B_element001,C_element017]
  conduct = 2
  density = 1
  expand = 3
  formula = G4_BORON_CARBIDE
  name = G4_BORON_CARBIDE
  specific = 4
FEATURE [App::DocumentObjectGroupPython] B_element002  label="B_element : 2"  # scripted group (container) (typed FeaturePython)
  n = 2
  ref = B_element
FEATURE [App::DocumentObjectGroupPython] O_element016  label="O_element : 006"  # scripted group (container) (typed FeaturePython)
  n = 3
  ref = O_element
FEATURE [App::DocumentObjectGroupPython] G4_BORON_OXIDE  # scripted group (container) (typed FeaturePython)
  Dunit = g/cm3
  Dvalue = 1.812
  Group = -> [B_element002,O_element016]
  conduct = 2
  density = 1
  expand = 3
  formula = G4_BORON_OXIDE
  name = G4_BORON_OXIDE
  specific = 4
FEATURE [App::DocumentObjectGroupPython] H_element017  label="H_element : 0.107"  # scripted group (container) (typed FeaturePython)
  n = 0.107
FEATURE [App::DocumentObjectGroupPython] C_element018  label="C_element : 0.145"  # scripted group (container) (typed FeaturePython)
  n = 0.145
FEATURE [App::DocumentObjectGroupPython] N_element012  label="N_element : 0.022"  # scripted group (container) (typed FeaturePython)
  n = 0.022
FEATURE [App::DocumentObjectGroupPython] O_element017  label="O_element : 0.712"  # scripted group (container) (typed FeaturePython)
  n = 0.712
FEATURE [App::DocumentObjectGroupPython] Na_element004  label="Na_element : 0.004"  # scripted group (container) (typed FeaturePython)
  n = 0.002
FEATURE [App::DocumentObjectGroupPython] P_element004  label="P_element : 0.004"  # scripted group (container) (typed FeaturePython)
  n = 0.004
FEATURE [App::DocumentObjectGroupPython] S_element006  label="S_element : 0.005"  # scripted group (container) (typed FeaturePython)
  n = 0.002
FEATURE [App::DocumentObjectGroupPython] Cl_element003  label="Cl_element : 0.004"  # scripted group (container) (typed FeaturePython)
  n = 0.003
FEATURE [App::DocumentObjectGroupPython] K_element002  label="K_element : 0.003"  # scripted group (container) (typed FeaturePython)
  n = 0.003
FEATURE [App::DocumentObjectGroupPython] G4_BRAIN_ICRP  # scripted group (container) (typed FeaturePython)
  Dunit = g/cm3
  Dvalue = 1.04
  Group = -> [H_element017,C_element018,N_element012,O_element017,Na_element004,P_element004,S_element006,Cl_element003,K_element002]
  conduct = 2
  density = 1
  expand = 3
  formula = G4_BRAIN_ICRP
  name = G4_BRAIN_ICRP
  specific = 4
FEATURE [App::DocumentObjectGroupPython] C_element019  label="C_element : 4"  # scripted group (container) (typed FeaturePython)
  n = 4
  ref = C_element
FEATURE [App::DocumentObjectGroupPython] H_element018  label="H_element : 010"  # scripted group (container) (typed FeaturePython)
  n = 10
  ref = H_element
FEATURE [App::DocumentObjectGroupPython] G4_BUTANE  # scripted group (container) (typed FeaturePython)
  Dunit = g/cm3
  Dvalue = 0.00249343
  Group = -> [C_element019,H_element018]
  conduct = 2
  density = 1
  expand = 3
  formula = G4_BUTANE
  name = G4_BUTANE
  specific = 4
FEATURE [App::DocumentObjectGroupPython] C_element020  label="C_element : 008"  # scripted group (container) (typed FeaturePython)
  n = 4
  ref = C_element
FEATURE [App::DocumentObjectGroupPython] H_element019  label="H_element : 011"  # scripted group (container) (typed FeaturePython)
  n = 10
  ref = H_element
FEATURE [App::DocumentObjectGroupPython] O_element018  label="O_element : 007"  # scripted group (container) (typed FeaturePython)
  n = 1
  ref = O_element
FEATURE [App::DocumentObjectGroupPython] G4_N_BUTYL_ALCOHOL  label="G4_N-BUTYL_ALCOHOL"  # scripted group (container) (typed FeaturePython)
  Dunit = g/cm3
  Dvalue = 0.8098
  Group = -> [C_element020,H_element019,O_element018]
  conduct = 2
  density = 1
  expand = 3
  formula = G4_N-BUTYL_ALCOHOL
  name = G4_N-BUTYL_ALCOHOL
  specific = 4
FEATURE [App::DocumentObjectGroupPython] H_element020  label="H_element : 0.025"  # scripted group (container) (typed FeaturePython)
  n = 0.02468
FEATURE [App::DocumentObjectGroupPython] C_element021  label="C_element : 0.502"  # scripted group (container) (typed FeaturePython)
  n = 0.501611
FEATURE [App::DocumentObjectGroupPython] O_element019  label="O_element : 0.005"  # scripted group (container) (typed FeaturePython)
  n = 0.004527
FEATURE [App::DocumentObjectGroupPython] F_element004  label="F_element : 0.465"  # scripted group (container) (typed FeaturePython)
  n = 0.465209
FEATURE [App::DocumentObjectGroupPython] Si_element001  label="Si_element : 0.004"  # scripted group (container) (typed FeaturePython)
  n = 0.003973
FEATURE [App::DocumentObjectGroupPython] G4_C_552  label="G4_C-552"  # scripted group (container) (typed FeaturePython)
  Dunit = g/cm3
  Dvalue = 1.76
  Group = -> [H_element020,C_element021,O_element019,F_element004,Si_element001]
  conduct = 2
  density = 1
  expand = 3
  formula = G4_C-552
  name = G4_C-552
  specific = 4
FEATURE [App::DocumentObjectGroupPython] Cd_element001  label="Cd_element : 1"  # scripted group (container) (typed FeaturePython)
  n = 1
  ref = Cd_element
FEATURE [App::DocumentObjectGroupPython] Te_element001  label="Te_element : 1"  # scripted group (container) (typed FeaturePython)
  n = 1
  ref = Te_element
FEATURE [App::DocumentObjectGroupPython] G4_CADMIUM_TELLURIDE  # scripted group (container) (typed FeaturePython)
  Dunit = g/cm3
  Dvalue = 6.2
  Group = -> [Cd_element001,Te_element001]
  conduct = 2
  density = 1
  expand = 3
  formula = G4_CADMIUM_TELLURIDE
  name = G4_CADMIUM_TELLURIDE
  specific = 4
FEATURE [App::DocumentObjectGroupPython] Cd_element002  label="Cd_element : 002"  # scripted group (container) (typed FeaturePython)
  n = 1
  ref = Cd_element
FEATURE [App::DocumentObjectGroupPython] W_element001  label="W_element : 1"  # scripted group (container) (typed FeaturePython)
  n = 1
  ref = W_element
FEATURE [App::DocumentObjectGroupPython] O_element020  label="O_element : 008"  # scripted group (container) (typed FeaturePython)
  n = 4
  ref = O_element
FEATURE [App::DocumentObjectGroupPython] G4_CADMIUM_TUNGSTATE  # scripted group (container) (typed FeaturePython)
  Dunit = g/cm3
  Dvalue = 7.9
  Group = -> [Cd_element002,W_element001,O_element020]
  conduct = 2
  density = 1
  expand = 3
  formula = G4_CADMIUM_TUNGSTATE
  name = G4_CADMIUM_TUNGSTATE
  specific = 4
FEATURE [App::DocumentObjectGroupPython] Ca_element005  label="Ca_element : 1"  # scripted group (container) (typed FeaturePython)
  n = 1
  ref = Ca_element
FEATURE [App::DocumentObjectGroupPython] C_element022  label="C_element : 009"  # scripted group (container) (typed FeaturePython)
  n = 1
  ref = C_element
FEATURE [App::DocumentObjectGroupPython] O_element021  label="O_element : 009"  # scripted group (container) (typed FeaturePython)
  n = 3
  ref = O_element
FEATURE [App::DocumentObjectGroupPython] G4_CALCIUM_CARBONATE  # scripted group (container) (typed FeaturePython)
  Dunit = g/cm3
  Dvalue = 2.8
  Group = -> [Ca_element005,C_element022,O_element021]
  conduct = 2
  density = 1
  expand = 3
  formula = G4_CALCIUM_CARBONATE
  name = G4_CALCIUM_CARBONATE
  specific = 4
FEATURE [App::DocumentObjectGroupPython] Ca_element006  label="Ca_element : 002"  # scripted group (container) (typed FeaturePython)
  n = 1
  ref = Ca_element
FEATURE [App::DocumentObjectGroupPython] F_element005  label="F_element : 003"  # scripted group (container) (typed FeaturePython)
  n = 2
  ref = F_element
FEATURE [App::DocumentObjectGroupPython] G4_CALCIUM_FLUORIDE  # scripted group (container) (typed FeaturePython)
  Dunit = g/cm3
  Dvalue = 3.18
  Group = -> [Ca_element006,F_element005]
  conduct = 2
  density = 1
  expand = 3
  formula = G4_CALCIUM_FLUORIDE
  name = G4_CALCIUM_FLUORIDE
  specific = 4
FEATURE [App::DocumentObjectGroupPython] Ca_element007  label="Ca_element : 003"  # scripted group (container) (typed FeaturePython)
  n = 1
  ref = Ca_element
FEATURE [App::DocumentObjectGroupPython] O_element022  label="O_element : 010"  # scripted group (container) (typed FeaturePython)
  n = 1
  ref = O_element
FEATURE [App::DocumentObjectGroupPython] G4_CALCIUM_OXIDE  # scripted group (container) (typed FeaturePython)
  Dunit = g/cm3
  Dvalue = 3.3
  Group = -> [Ca_element007,O_element022]
  conduct = 2
  density = 1
  expand = 3
  formula = G4_CALCIUM_OXIDE
  name = G4_CALCIUM_OXIDE
  specific = 4
FEATURE [App::DocumentObjectGroupPython] Ca_element008  label="Ca_element : 004"  # scripted group (container) (typed FeaturePython)
  n = 1
  ref = Ca_element
FEATURE [App::DocumentObjectGroupPython] S_element007  label="S_element : 002"  # scripted group (container) (typed FeaturePython)
  n = 1
  ref = S_element
FEATURE [App::DocumentObjectGroupPython] O_element023  label="O_element : 011"  # scripted group (container) (typed FeaturePython)
  n = 4
  ref = O_element
FEATURE [App::DocumentObjectGroupPython] G4_CALCIUM_SULFATE  # scripted group (container) (typed FeaturePython)
  Dunit = g/cm3
  Dvalue = 2.96
  Group = -> [Ca_element008,S_element007,O_element023]
  conduct = 2
  density = 1
  expand = 3
  formula = G4_CALCIUM_SULFATE
  name = G4_CALCIUM_SULFATE
  specific = 4
FEATURE [App::DocumentObjectGroupPython] Ca_element009  label="Ca_element : 005"  # scripted group (container) (typed FeaturePython)
  n = 1
  ref = Ca_element
FEATURE [App::DocumentObjectGroupPython] W_element002  label="W_element : 002"  # scripted group (container) (typed FeaturePython)
  n = 1
  ref = W_element
FEATURE [App::DocumentObjectGroupPython] O_element024  label="O_element : 012"  # scripted group (container) (typed FeaturePython)
  n = 4
  ref = O_element
FEATURE [App::DocumentObjectGroupPython] G4_CALCIUM_TUNGSTATE  # scripted group (container) (typed FeaturePython)
  Dunit = g/cm3
  Dvalue = 6.062
  Group = -> [Ca_element009,W_element002,O_element024]
  conduct = 2
  density = 1
  expand = 3
  formula = G4_CALCIUM_TUNGSTATE
  name = G4_CALCIUM_TUNGSTATE
  specific = 4
FEATURE [App::DocumentObjectGroupPython] C_element023  label="C_element : 010"  # scripted group (container) (typed FeaturePython)
  n = 1
  ref = C_element
FEATURE [App::DocumentObjectGroupPython] O_element025  label="O_element : 013"  # scripted group (container) (typed FeaturePython)
  n = 2
  ref = O_element
FEATURE [App::DocumentObjectGroupPython] G4_CARBON_DIOXIDE  # scripted group (container) (typed FeaturePython)
  Dunit = g/cm3
  Dvalue = 0.00184212
  Group = -> [C_element023,O_element025]
  conduct = 2
  density = 1
  expand = 3
  formula = G4_CARBON_DIOXIDE
  name = G4_CARBON_DIOXIDE
  specific = 4
FEATURE [App::DocumentObjectGroupPython] C_element024  label="C_element : 011"  # scripted group (container) (typed FeaturePython)
  n = 1
  ref = C_element
FEATURE [App::DocumentObjectGroupPython] Cl_element004  label="Cl_element : 4"  # scripted group (container) (typed FeaturePython)
  n = 4
  ref = Cl_element
FEATURE [App::DocumentObjectGroupPython] G4_CARBON_TETRACHLORIDE  # scripted group (container) (typed FeaturePython)
  Dunit = g/cm3
  Dvalue = 1.594
  Group = -> [C_element024,Cl_element004]
  conduct = 2
  density = 1
  expand = 3
  formula = G4_CARBON_TETRACHLORIDE
  name = G4_CARBON_TETRACHLORIDE
  specific = 4
FEATURE [App::DocumentObjectGroupPython] C_element025  label="C_element : 012"  # scripted group (container) (typed FeaturePython)
  n = 6
  ref = C_element
FEATURE [App::DocumentObjectGroupPython] H_element021  label="H_element : 012"  # scripted group (container) (typed FeaturePython)
  n = 10
  ref = H_element
FEATURE [App::DocumentObjectGroupPython] O_element026  label="O_element : 5"  # scripted group (container) (typed FeaturePython)
  n = 5
  ref = O_element
FEATURE [App::DocumentObjectGroupPython] G4_CELLULOSE_CELLOPHANE  # scripted group (container) (typed FeaturePython)
  Dunit = g/cm3
  Dvalue = 1.42
  Group = -> [C_element025,H_element021,O_element026]
  conduct = 2
  density = 1
  expand = 3
  formula = G4_CELLULOSE_CELLOPHANE
  name = G4_CELLULOSE_CELLOPHANE
  specific = 4
FEATURE [App::DocumentObjectGroupPython] H_element022  label="H_element : 0.067"  # scripted group (container) (typed FeaturePython)
  n = 0.067125
FEATURE [App::DocumentObjectGroupPython] C_element026  label="C_element : 0.545"  # scripted group (container) (typed FeaturePython)
  n = 0.545403
FEATURE [App::DocumentObjectGroupPython] O_element027  label="O_element : 0.387"  # scripted group (container) (typed FeaturePython)
  n = 0.387472
FEATURE [App::DocumentObjectGroupPython] G4_CELLULOSE_BUTYRATE  # scripted group (container) (typed FeaturePython)
  Dunit = g/cm3
  Dvalue = 1.2
  Group = -> [H_element022,C_element026,O_element027]
  conduct = 2
  density = 1
  expand = 3
  formula = G4_CELLULOSE_BUTYRATE
  name = G4_CELLULOSE_BUTYRATE
  specific = 4
FEATURE [App::DocumentObjectGroupPython] H_element023  label="H_element : 0.029"  # scripted group (container) (typed FeaturePython)
  n = 0.029216
FEATURE [App::DocumentObjectGroupPython] C_element027  label="C_element : 0.271"  # scripted group (container) (typed FeaturePython)
  n = 0.271296
FEATURE [App::DocumentObjectGroupPython] N_element013  label="N_element : 0.121"  # scripted group (container) (typed FeaturePython)
  n = 0.121276
FEATURE [App::DocumentObjectGroupPython] O_element028  label="O_element : 0.578"  # scripted group (container) (typed FeaturePython)
  n = 0.578212
FEATURE [App::DocumentObjectGroupPython] G4_CELLULOSE_NITRATE  # scripted group (container) (typed FeaturePython)
  Dunit = g/cm3
  Dvalue = 1.49
  Group = -> [H_element023,C_element027,N_element013,O_element028]
  conduct = 2
  density = 1
  expand = 3
  formula = G4_CELLULOSE_NITRATE
  name = G4_CELLULOSE_NITRATE
  specific = 4
FEATURE [App::DocumentObjectGroupPython] H_element024  label="H_element : 0.108"  # scripted group (container) (typed FeaturePython)
  n = 0.107596
FEATURE [App::DocumentObjectGroupPython] N_element014  label="N_element : 0.001"  # scripted group (container) (typed FeaturePython)
  n = 0.0008
FEATURE [App::DocumentObjectGroupPython] O_element029  label="O_element : 0.875"  # scripted group (container) (typed FeaturePython)
  n = 0.874976
FEATURE [App::DocumentObjectGroupPython] S_element008  label="S_element : 0.015"  # scripted group (container) (typed FeaturePython)
  n = 0.014627
FEATURE [App::DocumentObjectGroupPython] Ce_element001  label="Ce_element : 0.002"  # scripted group (container) (typed FeaturePython)
  n = 0.002001
FEATURE [App::DocumentObjectGroupPython] G4_CERIC_SULFATE  # scripted group (container) (typed FeaturePython)
  Dunit = g/cm3
  Dvalue = 1.03
  Group = -> [H_element024,N_element014,O_element029,S_element008,Ce_element001]
  conduct = 2
  density = 1
  expand = 3
  formula = G4_CERIC_SULFATE
  name = G4_CERIC_SULFATE
  specific = 4
FEATURE [App::DocumentObjectGroupPython] Cs_element001  label="Cs_element : 1"  # scripted group (container) (typed FeaturePython)
  n = 1
  ref = Cs_element
FEATURE [App::DocumentObjectGroupPython] F_element006  label="F_element : 1"  # scripted group (container) (typed FeaturePython)
  n = 1
  ref = F_element
FEATURE [App::DocumentObjectGroupPython] G4_CESIUM_FLUORIDE  # scripted group (container) (typed FeaturePython)
  Dunit = g/cm3
  Dvalue = 4.115
  Group = -> [Cs_element001,F_element006]
  conduct = 2
  density = 1
  expand = 3
  formula = G4_CESIUM_FLUORIDE
  name = G4_CESIUM_FLUORIDE
  specific = 4
FEATURE [App::DocumentObjectGroupPython] Cs_element002  label="Cs_element : 002"  # scripted group (container) (typed FeaturePython)
  n = 1
  ref = Cs_element
FEATURE [App::DocumentObjectGroupPython] I_element001  label="I_element : 1"  # scripted group (container) (typed FeaturePython)
  n = 1
  ref = I_element
FEATURE [App::DocumentObjectGroupPython] G4_CESIUM_IODIDE  # scripted group (container) (typed FeaturePython)
  Dunit = g/cm3
  Dvalue = 4.51
  Group = -> [Cs_element002,I_element001]
  conduct = 2
  density = 1
  expand = 3
  formula = G4_CESIUM_IODIDE
  name = G4_CESIUM_IODIDE
  specific = 4
FEATURE [App::DocumentObjectGroupPython] C_element028  label="C_element : 013"  # scripted group (container) (typed FeaturePython)
  n = 6
  ref = C_element
FEATURE [App::DocumentObjectGroupPython] H_element025  label="H_element : 013"  # scripted group (container) (typed FeaturePython)
  n = 5
  ref = H_element
FEATURE [App::DocumentObjectGroupPython] Cl_element005  label="Cl_element : 1"  # scripted group (container) (typed FeaturePython)
  n = 1
  ref = Cl_element
FEATURE [App::DocumentObjectGroupPython] G4_CHLOROBENZENE  # scripted group (container) (typed FeaturePython)
  Dunit = g/cm3
  Dvalue = 1.1058
  Group = -> [C_element028,H_element025,Cl_element005]
  conduct = 2
  density = 1
  expand = 3
  formula = G4_CHLOROBENZENE
  name = G4_CHLOROBENZENE
  specific = 4
FEATURE [App::DocumentObjectGroupPython] C_element029  label="C_element : 014"  # scripted group (container) (typed FeaturePython)
  n = 1
  ref = C_element
FEATURE [App::DocumentObjectGroupPython] H_element026  label="H_element : 1"  # scripted group (container) (typed FeaturePython)
  n = 1
  ref = H_element
FEATURE [App::DocumentObjectGroupPython] Cl_element006  label="Cl_element : 3"  # scripted group (container) (typed FeaturePython)
  n = 3
  ref = Cl_element
FEATURE [App::DocumentObjectGroupPython] G4_CHLOROFORM  # scripted group (container) (typed FeaturePython)
  Dunit = g/cm3
  Dvalue = 1.4832
  Group = -> [C_element029,H_element026,Cl_element006]
  conduct = 2
  density = 1
  expand = 3
  formula = G4_CHLOROFORM
  name = G4_CHLOROFORM
  specific = 4
FEATURE [App::DocumentObjectGroupPython] H_element027  label="H_element : 0.010"  # scripted group (container) (typed FeaturePython)
  n = 0.01
FEATURE [App::DocumentObjectGroupPython] C_element030  label="C_element : 0.001"  # scripted group (container) (typed FeaturePython)
  n = 0.001
FEATURE [App::DocumentObjectGroupPython] O_element030  label="O_element : 0.529"  # scripted group (container) (typed FeaturePython)
  n = 0.529107
FEATURE [App::DocumentObjectGroupPython] Na_element005  label="Na_element : 0.016"  # scripted group (container) (typed FeaturePython)
  n = 0.016
FEATURE [App::DocumentObjectGroupPython] Mg_element003  label="Mg_element : 0.004"  # scripted group (container) (typed FeaturePython)
  n = 0.002
FEATURE [App::DocumentObjectGroupPython] Al_element002  label="Al_element : 0.034"  # scripted group (container) (typed FeaturePython)
  n = 0.033872
FEATURE [App::DocumentObjectGroupPython] Si_element002  label="Si_element : 0.337"  # scripted group (container) (typed FeaturePython)
  n = 0.337021
FEATURE [App::DocumentObjectGroupPython] K_element003  label="K_element : 0.013"  # scripted group (container) (typed FeaturePython)
  n = 0.013
FEATURE [App::DocumentObjectGroupPython] Ca_element010  label="Ca_element : 0.044"  # scripted group (container) (typed FeaturePython)
  n = 0.044
FEATURE [App::DocumentObjectGroupPython] Fe_element002  label="Fe_element : 0.014"  # scripted group (container) (typed FeaturePython)
  n = 0.014
FEATURE [App::DocumentObjectGroupPython] G4_CONCRETE  # scripted group (container) (typed FeaturePython)
  Dunit = g/cm3
  Dvalue = 2.3
  Group = -> [H_element027,C_element030,O_element030,Na_element005,Mg_element003,Al_element002,Si_element002,K_element003,Ca_element010,Fe_element002]
  conduct = 2
  density = 1
  expand = 3
  formula = G4_CONCRETE
  name = G4_CONCRETE
  specific = 4
FEATURE [App::DocumentObjectGroupPython] C_element031  label="C_element : 015"  # scripted group (container) (typed FeaturePython)
  n = 6
  ref = C_element
FEATURE [App::DocumentObjectGroupPython] H_element028  label="H_element : 12"  # scripted group (container) (typed FeaturePython)
  n = 12
  ref = H_element
FEATURE [App::DocumentObjectGroupPython] G4_CYCLOHEXANE  # scripted group (container) (typed FeaturePython)
  Dunit = g/cm3
  Dvalue = 0.779
  Group = -> [C_element031,H_element028]
  conduct = 2
  density = 1
  expand = 3
  formula = G4_CYCLOHEXANE
  name = G4_CYCLOHEXANE
  specific = 4
FEATURE [App::DocumentObjectGroupPython] C_element032  label="C_element : 016"  # scripted group (container) (typed FeaturePython)
  n = 6
  ref = C_element
FEATURE [App::DocumentObjectGroupPython] H_element029  label="H_element : 4"  # scripted group (container) (typed FeaturePython)
  n = 4
  ref = H_element
FEATURE [App::DocumentObjectGroupPython] Cl_element007  label="Cl_element : 2"  # scripted group (container) (typed FeaturePython)
  n = 2
  ref = Cl_element
FEATURE [App::DocumentObjectGroupPython] G4_1_2_DICHLOROBENZENE  label="G4_1.2-DICHLOROBENZENE"  # scripted group (container) (typed FeaturePython)
  Dunit = g/cm3
  Dvalue = 1.3048
  Group = -> [C_element032,H_element029,Cl_element007]
  conduct = 2
  density = 1
  expand = 3
  formula = G4_1.2-DICHLOROBENZENE
  name = G4_1.2-DICHLOROBENZENE
  specific = 4
FEATURE [App::DocumentObjectGroupPython] C_element033  label="C_element : 017"  # scripted group (container) (typed FeaturePython)
  n = 4
  ref = C_element
FEATURE [App::DocumentObjectGroupPython] H_element030  label="H_element : 8"  # scripted group (container) (typed FeaturePython)
  n = 8
  ref = H_element
FEATURE [App::DocumentObjectGroupPython] O_element031  label="O_element : 014"  # scripted group (container) (typed FeaturePython)
  n = 1
  ref = O_element
FEATURE [App::DocumentObjectGroupPython] Cl_element008  label="Cl_element : 005"  # scripted group (container) (typed FeaturePython)
  n = 2
  ref = Cl_element
FEATURE [App::DocumentObjectGroupPython] G4_DICHLORODIETHYL_ETHER  # scripted group (container) (typed FeaturePython)
  Dunit = g/cm3
  Dvalue = 1.2199
  Group = -> [C_element033,H_element030,O_element031,Cl_element008]
  conduct = 2
  density = 1
  expand = 3
  formula = G4_DICHLORODIETHYL_ETHER
  name = G4_DICHLORODIETHYL_ETHER
  specific = 4
FEATURE [App::DocumentObjectGroupPython] C_element034  label="C_element : 018"  # scripted group (container) (typed FeaturePython)
  n = 2
  ref = C_element
FEATURE [App::DocumentObjectGroupPython] H_element031  label="H_element : 014"  # scripted group (container) (typed FeaturePython)
  n = 4
  ref = H_element
FEATURE [App::DocumentObjectGroupPython] Cl_element009  label="Cl_element : 006"  # scripted group (container) (typed FeaturePython)
  n = 2
  ref = Cl_element
FEATURE [App::DocumentObjectGroupPython] G4_1_2_DICHLOROETHANE  label="G4_1.2-DICHLOROETHANE"  # scripted group (container) (typed FeaturePython)
  Dunit = g/cm3
  Dvalue = 1.2351
  Group = -> [C_element034,H_element031,Cl_element009]
  conduct = 2
  density = 1
  expand = 3
  formula = G4_1.2-DICHLOROETHANE
  name = G4_1.2-DICHLOROETHANE
  specific = 4
FEATURE [App::DocumentObjectGroupPython] C_element035  label="C_element : 019"  # scripted group (container) (typed FeaturePython)
  n = 4
  ref = C_element
FEATURE [App::DocumentObjectGroupPython] H_element032  label="H_element : 015"  # scripted group (container) (typed FeaturePython)
  n = 10
  ref = H_element
FEATURE [App::DocumentObjectGroupPython] O_element032  label="O_element : 015"  # scripted group (container) (typed FeaturePython)
  n = 1
  ref = O_element
FEATURE [App::DocumentObjectGroupPython] G4_DIETHYL_ETHER  # scripted group (container) (typed FeaturePython)
  Dunit = g/cm3
  Dvalue = 0.71378
  Group = -> [C_element035,H_element032,O_element032]
  conduct = 2
  density = 1
  expand = 3
  formula = G4_DIETHYL_ETHER
  name = G4_DIETHYL_ETHER
  specific = 4
FEATURE [App::DocumentObjectGroupPython] C_element036  label="C_element : 020"  # scripted group (container) (typed FeaturePython)
  n = 3
  ref = C_element
FEATURE [App::DocumentObjectGroupPython] H_element033  label="H_element : 016"  # scripted group (container) (typed FeaturePython)
  n = 7
  ref = H_element
FEATURE [App::DocumentObjectGroupPython] N_element015  label="N_element : 008"  # scripted group (container) (typed FeaturePython)
  n = 1
  ref = N_element
FEATURE [App::DocumentObjectGroupPython] O_element033  label="O_element : 016"  # scripted group (container) (typed FeaturePython)
  n = 1
  ref = O_element
FEATURE [App::DocumentObjectGroupPython] G4_N_N_DIMETHYL_FORMAMIDE  label="G4_N.N-DIMETHYL_FORMAMIDE"  # scripted group (container) (typed FeaturePython)
  Dunit = g/cm3
  Dvalue = 0.9487
  Group = -> [C_element036,H_element033,N_element015,O_element033]
  conduct = 2
  density = 1
  expand = 3
  formula = G4_N.N-DIMETHYL_FORMAMIDE
  name = G4_N.N-DIMETHYL_FORMAMIDE
  specific = 4
FEATURE [App::DocumentObjectGroupPython] C_element037  label="C_element : 021"  # scripted group (container) (typed FeaturePython)
  n = 2
  ref = C_element
FEATURE [App::DocumentObjectGroupPython] H_element034  label="H_element : 017"  # scripted group (container) (typed FeaturePython)
  n = 6
  ref = H_element
FEATURE [App::DocumentObjectGroupPython] O_element034  label="O_element : 017"  # scripted group (container) (typed FeaturePython)
  n = 1
  ref = O_element
FEATURE [App::DocumentObjectGroupPython] S_element009  label="S_element : 003"  # scripted group (container) (typed FeaturePython)
  n = 1
  ref = S_element
FEATURE [App::DocumentObjectGroupPython] G4_DIMETHYL_SULFOXIDE  # scripted group (container) (typed FeaturePython)
  Dunit = g/cm3
  Dvalue = 1.1014
  Group = -> [C_element037,H_element034,O_element034,S_element009]
  conduct = 2
  density = 1
  expand = 3
  formula = G4_DIMETHYL_SULFOXIDE
  name = G4_DIMETHYL_SULFOXIDE
  specific = 4
FEATURE [App::DocumentObjectGroupPython] C_element038  label="C_element : 022"  # scripted group (container) (typed FeaturePython)
  n = 2
  ref = C_element
FEATURE [App::DocumentObjectGroupPython] H_element035  label="H_element : 018"  # scripted group (container) (typed FeaturePython)
  n = 6
  ref = H_element
FEATURE [App::DocumentObjectGroupPython] G4_ETHANE  # scripted group (container) (typed FeaturePython)
  Dunit = g/cm3
  Dvalue = 0.00125324
  Group = -> [C_element038,H_element035]
  conduct = 2
  density = 1
  expand = 3
  formula = G4_ETHANE
  name = G4_ETHANE
  specific = 4
FEATURE [App::DocumentObjectGroupPython] C_element039  label="C_element : 023"  # scripted group (container) (typed FeaturePython)
  n = 2
  ref = C_element
FEATURE [App::DocumentObjectGroupPython] H_element036  label="H_element : 019"  # scripted group (container) (typed FeaturePython)
  n = 6
  ref = H_element
FEATURE [App::DocumentObjectGroupPython] O_element035  label="O_element : 018"  # scripted group (container) (typed FeaturePython)
  n = 1
  ref = O_element
FEATURE [App::DocumentObjectGroupPython] G4_ETHYL_ALCOHOL  # scripted group (container) (typed FeaturePython)
  Dunit = g/cm3
  Dvalue = 0.7893
  Group = -> [C_element039,H_element036,O_element035]
  conduct = 2
  density = 1
  expand = 3
  formula = G4_ETHYL_ALCOHOL
  name = G4_ETHYL_ALCOHOL
  specific = 4
FEATURE [App::DocumentObjectGroupPython] H_element037  label="H_element : 0.090"  # scripted group (container) (typed FeaturePython)
  n = 0.090027
FEATURE [App::DocumentObjectGroupPython] C_element040  label="C_element : 0.585"  # scripted group (container) (typed FeaturePython)
  n = 0.585182
FEATURE [App::DocumentObjectGroupPython] O_element036  label="O_element : 0.325"  # scripted group (container) (typed FeaturePython)
  n = 0.324791
FEATURE [App::DocumentObjectGroupPython] G4_ETHYL_CELLULOSE  # scripted group (container) (typed FeaturePython)
  Dunit = g/cm3
  Dvalue = 1.13
  Group = -> [H_element037,C_element040,O_element036]
  conduct = 2
  density = 1
  expand = 3
  formula = G4_ETHYL_CELLULOSE
  name = G4_ETHYL_CELLULOSE
  specific = 4
FEATURE [App::DocumentObjectGroupPython] C_element041  label="C_element : 024"  # scripted group (container) (typed FeaturePython)
  n = 2
  ref = C_element
FEATURE [App::DocumentObjectGroupPython] H_element038  label="H_element : 020"  # scripted group (container) (typed FeaturePython)
  n = 4
  ref = H_element
FEATURE [App::DocumentObjectGroupPython] G4_ETHYLENE  # scripted group (container) (typed FeaturePython)
  Dunit = g/cm3
  Dvalue = 0.00117497
  Group = -> [C_element041,H_element038]
  conduct = 2
  density = 1
  expand = 3
  formula = G4_ETHYLENE
  name = G4_ETHYLENE
  specific = 4
FEATURE [App::DocumentObjectGroupPython] H_element039  label="H_element : 0.096"  # scripted group (container) (typed FeaturePython)
  n = 0.096
FEATURE [App::DocumentObjectGroupPython] C_element042  label="C_element : 0.195"  # scripted group (container) (typed FeaturePython)
  n = 0.195
FEATURE [App::DocumentObjectGroupPython] N_element016  label="N_element : 0.057"  # scripted group (container) (typed FeaturePython)
  n = 0.057
FEATURE [App::DocumentObjectGroupPython] O_element037  label="O_element : 0.646"  # scripted group (container) (typed FeaturePython)
  n = 0.646
FEATURE [App::DocumentObjectGroupPython] Na_element006  label="Na_element : 0.017"  # scripted group (container) (typed FeaturePython)
  n = 0.001
FEATURE [App::DocumentObjectGroupPython] P_element005  label="P_element : 0.104"  # scripted group (container) (typed FeaturePython)
  n = 0.001
FEATURE [App::DocumentObjectGroupPython] S_element010  label="S_element : 0.016"  # scripted group (container) (typed FeaturePython)
  n = 0.003
FEATURE [App::DocumentObjectGroupPython] Cl_element010  label="Cl_element : 0.005"  # scripted group (container) (typed FeaturePython)
  n = 0.001
FEATURE [App::DocumentObjectGroupPython] G4_EYE_LENS_ICRP  # scripted group (container) (typed FeaturePython)
  Dunit = g/cm3
  Dvalue = 1.07
  Group = -> [H_element039,C_element042,N_element016,O_element037,Na_element006,P_element005,S_element010,Cl_element010]
  conduct = 2
  density = 1
  expand = 3
  formula = G4_EYE_LENS_ICRP
  name = G4_EYE_LENS_ICRP
  specific = 4
FEATURE [App::DocumentObjectGroupPython] Fe_element003  label="Fe_element : 2"  # scripted group (container) (typed FeaturePython)
  n = 2
  ref = Fe_element
FEATURE [App::DocumentObjectGroupPython] O_element038  label="O_element : 019"  # scripted group (container) (typed FeaturePython)
  n = 3
  ref = O_element
FEATURE [App::DocumentObjectGroupPython] G4_FERRIC_OXIDE  # scripted group (container) (typed FeaturePython)
  Dunit = g/cm3
  Dvalue = 5.2
  Group = -> [Fe_element003,O_element038]
  conduct = 2
  density = 1
  expand = 3
  formula = G4_FERRIC_OXIDE
  name = G4_FERRIC_OXIDE
  specific = 4
FEATURE [App::DocumentObjectGroupPython] Fe_element004  label="Fe_element : 1"  # scripted group (container) (typed FeaturePython)
  n = 1
  ref = Fe_element
FEATURE [App::DocumentObjectGroupPython] B_element003  label="B_element : 1"  # scripted group (container) (typed FeaturePython)
  n = 1
  ref = B_element
FEATURE [App::DocumentObjectGroupPython] G4_FERROBORIDE  # scripted group (container) (typed FeaturePython)
  Dunit = g/cm3
  Dvalue = 7.15
  Group = -> [Fe_element004,B_element003]
  conduct = 2
  density = 1
  expand = 3
  formula = G4_FERROBORIDE
  name = G4_FERROBORIDE
  specific = 4
FEATURE [App::DocumentObjectGroupPython] Fe_element005  label="Fe_element : 003"  # scripted group (container) (typed FeaturePython)
  n = 1
  ref = Fe_element
FEATURE [App::DocumentObjectGroupPython] O_element039  label="O_element : 020"  # scripted group (container) (typed FeaturePython)
  n = 1
  ref = O_element
FEATURE [App::DocumentObjectGroupPython] G4_FERROUS_OXIDE  # scripted group (container) (typed FeaturePython)
  Dunit = g/cm3
  Dvalue = 5.7
  Group = -> [Fe_element005,O_element039]
  conduct = 2
  density = 1
  expand = 3
  formula = G4_FERROUS_OXIDE
  name = G4_FERROUS_OXIDE
  specific = 4
FEATURE [App::DocumentObjectGroupPython] H_element040  label="H_element : 0.115"  # scripted group (container) (typed FeaturePython)
  n = 0.108259
FEATURE [App::DocumentObjectGroupPython] N_element017  label="N_element : 0.000"  # scripted group (container) (typed FeaturePython)
  n = 2.7e-05
FEATURE [App::DocumentObjectGroupPython] O_element040  label="O_element : 0.879"  # scripted group (container) (typed FeaturePython)
  n = 0.878636
FEATURE [App::DocumentObjectGroupPython] Na_element007  label="Na_element : 0.000"  # scripted group (container) (typed FeaturePython)
  n = 2.2e-05
FEATURE [App::DocumentObjectGroupPython] S_element011  label="S_element : 0.013"  # scripted group (container) (typed FeaturePython)
  n = 0.012968
FEATURE [App::DocumentObjectGroupPython] Cl_element011  label="Cl_element : 0.000"  # scripted group (container) (typed FeaturePython)
  n = 3.4e-05
FEATURE [App::DocumentObjectGroupPython] Fe_element006  label="Fe_element : 0.000"  # scripted group (container) (typed FeaturePython)
  n = 5.4e-05
FEATURE [App::DocumentObjectGroupPython] G4_FERROUS_SULFATE  # scripted group (container) (typed FeaturePython)
  Dunit = g/cm3
  Dvalue = 1.024
  Group = -> [H_element040,N_element017,O_element040,Na_element007,S_element011,Cl_element011,Fe_element006]
  conduct = 2
  density = 1
  expand = 3
  formula = G4_FERROUS_SULFATE
  name = G4_FERROUS_SULFATE
  specific = 4
FEATURE [App::DocumentObjectGroupPython] C_element043  label="C_element : 0.099"  # scripted group (container) (typed FeaturePython)
  n = 0.099335
FEATURE [App::DocumentObjectGroupPython] F_element007  label="F_element : 0.314"  # scripted group (container) (typed FeaturePython)
  n = 0.314247
FEATURE [App::DocumentObjectGroupPython] Cl_element012  label="Cl_element : 0.586"  # scripted group (container) (typed FeaturePython)
  n = 0.586418
FEATURE [App::DocumentObjectGroupPython] G4_FREON_12  label="G4_FREON-12"  # scripted group (container) (typed FeaturePython)
  Dunit = g/cm3
  Dvalue = 1.12
  Group = -> [C_element043,F_element007,Cl_element012]
  conduct = 2
  density = 1
  expand = 3
  formula = G4_FREON-12
  name = G4_FREON-12
  specific = 4
FEATURE [App::DocumentObjectGroupPython] C_element044  label="C_element : 0.057"  # scripted group (container) (typed FeaturePython)
  n = 0.057245
FEATURE [App::DocumentObjectGroupPython] F_element008  label="F_element : 0.181"  # scripted group (container) (typed FeaturePython)
  n = 0.181096
FEATURE [App::DocumentObjectGroupPython] Br_element001  label="Br_element : 0.762"  # scripted group (container) (typed FeaturePython)
  n = 0.761659
FEATURE [App::DocumentObjectGroupPython] G4_FREON_12B2  label="G4_FREON-12B2"  # scripted group (container) (typed FeaturePython)
  Dunit = g/cm3
  Dvalue = 1.8
  Group = -> [C_element044,F_element008,Br_element001]
  conduct = 2
  density = 1
  expand = 3
  formula = G4_FREON-12B2
  name = G4_FREON-12B2
  specific = 4
FEATURE [App::DocumentObjectGroupPython] C_element045  label="C_element : 0.115"  # scripted group (container) (typed FeaturePython)
  n = 0.114983
FEATURE [App::DocumentObjectGroupPython] F_element009  label="F_element : 0.546"  # scripted group (container) (typed FeaturePython)
  n = 0.545621
FEATURE [App::DocumentObjectGroupPython] Cl_element013  label="Cl_element : 0.339"  # scripted group (container) (typed FeaturePython)
  n = 0.339396
FEATURE [App::DocumentObjectGroupPython] G4_FREON_13  label="G4_FREON-13"  # scripted group (container) (typed FeaturePython)
  Dunit = g/cm3
  Dvalue = 0.95
  Group = -> [C_element045,F_element009,Cl_element013]
  conduct = 2
  density = 1
  expand = 3
  formula = G4_FREON-13
  name = G4_FREON-13
  specific = 4
FEATURE [App::DocumentObjectGroupPython] C_element046  label="C_element : 025"  # scripted group (container) (typed FeaturePython)
  n = 1
  ref = C_element
FEATURE [App::DocumentObjectGroupPython] F_element010  label="F_element : 3"  # scripted group (container) (typed FeaturePython)
  n = 3
  ref = F_element
FEATURE [App::DocumentObjectGroupPython] Br_element002  label="Br_element : 1"  # scripted group (container) (typed FeaturePython)
  n = 1
  ref = Br_element
FEATURE [App::DocumentObjectGroupPython] G4_FREON_13B1  label="G4_FREON-13B1"  # scripted group (container) (typed FeaturePython)
  Dunit = g/cm3
  Dvalue = 1.5
  Group = -> [C_element046,F_element010,Br_element002]
  conduct = 2
  density = 1
  expand = 3
  formula = G4_FREON-13B1
  name = G4_FREON-13B1
  specific = 4
FEATURE [App::DocumentObjectGroupPython] C_element047  label="C_element : 0.061"  # scripted group (container) (typed FeaturePython)
  n = 0.061309
FEATURE [App::DocumentObjectGroupPython] F_element011  label="F_element : 0.291"  # scripted group (container) (typed FeaturePython)
  n = 0.290924
FEATURE [App::DocumentObjectGroupPython] I_element002  label="I_element : 0.648"  # scripted group (container) (typed FeaturePython)
  n = 0.647767
FEATURE [App::DocumentObjectGroupPython] G4_FREON_13I1  label="G4_FREON-13I1"  # scripted group (container) (typed FeaturePython)
  Dunit = g/cm3
  Dvalue = 1.8
  Group = -> [C_element047,F_element011,I_element002]
  conduct = 2
  density = 1
  expand = 3
  formula = G4_FREON-13I1
  name = G4_FREON-13I1
  specific = 4
FEATURE [App::DocumentObjectGroupPython] Gd_element001  label="Gd_element : 2"  # scripted group (container) (typed FeaturePython)
  n = 2
  ref = Gd_element
FEATURE [App::DocumentObjectGroupPython] O_element041  label="O_element : 021"  # scripted group (container) (typed FeaturePython)
  n = 2
  ref = O_element
FEATURE [App::DocumentObjectGroupPython] S_element012  label="S_element : 004"  # scripted group (container) (typed FeaturePython)
  n = 1
  ref = S_element
FEATURE [App::DocumentObjectGroupPython] G4_GADOLINIUM_OXYSULFIDE  # scripted group (container) (typed FeaturePython)
  Dunit = g/cm3
  Dvalue = 7.44
  Group = -> [Gd_element001,O_element041,S_element012]
  conduct = 2
  density = 1
  expand = 3
  formula = G4_GADOLINIUM_OXYSULFIDE
  name = G4_GADOLINIUM_OXYSULFIDE
  specific = 4
FEATURE [App::DocumentObjectGroupPython] Ga_element001  label="Ga_element : 1"  # scripted group (container) (typed FeaturePython)
  n = 1
  ref = Ga_element
FEATURE [App::DocumentObjectGroupPython] As_element001  label="As_element : 1"  # scripted group (container) (typed FeaturePython)
  n = 1
  ref = As_element
FEATURE [App::DocumentObjectGroupPython] G4_GALLIUM_ARSENIDE  # scripted group (container) (typed FeaturePython)
  Dunit = g/cm3
  Dvalue = 5.31
  Group = -> [Ga_element001,As_element001]
  conduct = 2
  density = 1
  expand = 3
  formula = G4_GALLIUM_ARSENIDE
  name = G4_GALLIUM_ARSENIDE
  specific = 4
FEATURE [App::DocumentObjectGroupPython] H_element041  label="H_element : 0.081"  # scripted group (container) (typed FeaturePython)
  n = 0.08118
FEATURE [App::DocumentObjectGroupPython] C_element048  label="C_element : 0.416"  # scripted group (container) (typed FeaturePython)
  n = 0.41606
FEATURE [App::DocumentObjectGroupPython] N_element018  label="N_element : 0.111"  # scripted group (container) (typed FeaturePython)
  n = 0.11124
FEATURE [App::DocumentObjectGroupPython] O_element042  label="O_element : 0.381"  # scripted group (container) (typed FeaturePython)
  n = 0.38064
FEATURE [App::DocumentObjectGroupPython] S_element013  label="S_element : 0.011"  # scripted group (container) (typed FeaturePython)
  n = 0.01088
FEATURE [App::DocumentObjectGroupPython] G4_GEL_PHOTO_EMULSION  # scripted group (container) (typed FeaturePython)
  Dunit = g/cm3
  Dvalue = 1.2914
  Group = -> [H_element041,C_element048,N_element018,O_element042,S_element013]
  conduct = 2
  density = 1
  expand = 3
  formula = G4_GEL_PHOTO_EMULSION
  name = G4_GEL_PHOTO_EMULSION
  specific = 4
FEATURE [App::DocumentObjectGroupPython] B_element004  label="B_element : 0.040"  # scripted group (container) (typed FeaturePython)
  n = 0.0400639
FEATURE [App::DocumentObjectGroupPython] O_element043  label="O_element : 0.540"  # scripted group (container) (typed FeaturePython)
  n = 0.539561
FEATURE [App::DocumentObjectGroupPython] Na_element008  label="Na_element : 0.028"  # scripted group (container) (typed FeaturePython)
  n = 0.0281909
FEATURE [App::DocumentObjectGroupPython] Al_element003  label="Al_element : 0.012"  # scripted group (container) (typed FeaturePython)
  n = 0.011644
FEATURE [App::DocumentObjectGroupPython] Si_element003  label="Si_element : 0.377"  # scripted group (container) (typed FeaturePython)
  n = 0.377219
FEATURE [App::DocumentObjectGroupPython] K_element004  label="K_element : 0.014"  # scripted group (container) (typed FeaturePython)
  n = 0.00332099
FEATURE [App::DocumentObjectGroupPython] G4_Pyrex_Glass  # scripted group (container) (typed FeaturePython)
  Dunit = g/cm3
  Dvalue = 2.23
  Group = -> [B_element004,O_element043,Na_element008,Al_element003,Si_element003,K_element004]
  conduct = 2
  density = 1
  expand = 3
  formula = G4_Pyrex_Glass
  name = G4_Pyrex_Glass
  specific = 4
FEATURE [App::DocumentObjectGroupPython] O_element044  label="O_element : 0.156"  # scripted group (container) (typed FeaturePython)
  n = 0.156453
FEATURE [App::DocumentObjectGroupPython] Si_element004  label="Si_element : 0.081"  # scripted group (container) (typed FeaturePython)
  n = 0.080866
FEATURE [App::DocumentObjectGroupPython] Ti_element001  label="Ti_element : 0.008"  # scripted group (container) (typed FeaturePython)
  n = 0.008092
FEATURE [App::DocumentObjectGroupPython] As_element002  label="As_element : 0.003"  # scripted group (container) (typed FeaturePython)
  n = 0.002651
FEATURE [App::DocumentObjectGroupPython] Pb_element001  label="Pb_element : 0.752"  # scripted group (container) (typed FeaturePython)
  n = 0.751938
FEATURE [App::DocumentObjectGroupPython] G4_GLASS_LEAD  # scripted group (container) (typed FeaturePython)
  Dunit = g/cm3
  Dvalue = 6.22
  Group = -> [O_element044,Si_element004,Ti_element001,As_element002,Pb_element001]
  conduct = 2
  density = 1
  expand = 3
  formula = G4_GLASS_LEAD
  name = G4_GLASS_LEAD
  specific = 4
FEATURE [App::DocumentObjectGroupPython] O_element045  label="O_element : 0.460"  # scripted group (container) (typed FeaturePython)
  n = 0.4598
FEATURE [App::DocumentObjectGroupPython] Na_element009  label="Na_element : 0.096"  # scripted group (container) (typed FeaturePython)
  n = 0.0964411
FEATURE [App::DocumentObjectGroupPython] Si_element005  label="Si_element : 0.378"  # scripted group (container) (typed FeaturePython)
  n = 0.336553
FEATURE [App::DocumentObjectGroupPython] Ca_element011  label="Ca_element : 0.107"  # scripted group (container) (typed FeaturePython)
  n = 0.107205
FEATURE [App::DocumentObjectGroupPython] G4_GLASS_PLATE  # scripted group (container) (typed FeaturePython)
  Dunit = g/cm3
  Dvalue = 2.4
  Group = -> [O_element045,Na_element009,Si_element005,Ca_element011]
  conduct = 2
  density = 1
  expand = 3
  formula = G4_GLASS_PLATE
  name = G4_GLASS_PLATE
  specific = 4
FEATURE [App::DocumentObjectGroupPython] C_element049  label="C_element : 026"  # scripted group (container) (typed FeaturePython)
  n = 5
  ref = C_element
FEATURE [App::DocumentObjectGroupPython] H_element042  label="H_element : 021"  # scripted group (container) (typed FeaturePython)
  n = 10
  ref = H_element
FEATURE [App::DocumentObjectGroupPython] N_element019  label="N_element : 2"  # scripted group (container) (typed FeaturePython)
  n = 2
  ref = N_element
FEATURE [App::DocumentObjectGroupPython] O_element046  label="O_element : 022"  # scripted group (container) (typed FeaturePython)
  n = 3
  ref = O_element
FEATURE [App::DocumentObjectGroupPython] G4_GLUTAMINE  # scripted group (container) (typed FeaturePython)
  Dunit = g/cm3
  Dvalue = 1.46
  Group = -> [C_element049,H_element042,N_element019,O_element046]
  conduct = 2
  density = 1
  expand = 3
  formula = G4_GLUTAMINE
  name = G4_GLUTAMINE
  specific = 4
FEATURE [App::DocumentObjectGroupPython] C_element050  label="C_element : 027"  # scripted group (container) (typed FeaturePython)
  n = 3
  ref = C_element
FEATURE [App::DocumentObjectGroupPython] H_element043  label="H_element : 022"  # scripted group (container) (typed FeaturePython)
  n = 8
  ref = H_element
FEATURE [App::DocumentObjectGroupPython] O_element047  label="O_element : 023"  # scripted group (container) (typed FeaturePython)
  n = 3
  ref = O_element
FEATURE [App::DocumentObjectGroupPython] G4_GLYCEROL  # scripted group (container) (typed FeaturePython)
  Dunit = g/cm3
  Dvalue = 1.2613
  Group = -> [C_element050,H_element043,O_element047]
  conduct = 2
  density = 1
  expand = 3
  formula = G4_GLYCEROL
  name = G4_GLYCEROL
  specific = 4
FEATURE [App::DocumentObjectGroupPython] C_element051  label="C_element : 028"  # scripted group (container) (typed FeaturePython)
  n = 5
  ref = C_element
FEATURE [App::DocumentObjectGroupPython] H_element044  label="H_element : 023"  # scripted group (container) (typed FeaturePython)
  n = 5
  ref = H_element
FEATURE [App::DocumentObjectGroupPython] N_element020  label="N_element : 009"  # scripted group (container) (typed FeaturePython)
  n = 5
  ref = N_element
FEATURE [App::DocumentObjectGroupPython] O_element048  label="O_element : 024"  # scripted group (container) (typed FeaturePython)
  n = 1
  ref = O_element
FEATURE [App::DocumentObjectGroupPython] G4_GUANINE  # scripted group (container) (typed FeaturePython)
  Dunit = g/cm3
  Dvalue = 2.2
  Group = -> [C_element051,H_element044,N_element020,O_element048]
  conduct = 2
  density = 1
  expand = 3
  formula = G4_GUANINE
  name = G4_GUANINE
  specific = 4
FEATURE [App::DocumentObjectGroupPython] Ca_element012  label="Ca_element : 006"  # scripted group (container) (typed FeaturePython)
  n = 1
  ref = Ca_element
FEATURE [App::DocumentObjectGroupPython] S_element014  label="S_element : 005"  # scripted group (container) (typed FeaturePython)
  n = 1
  ref = S_element
FEATURE [App::DocumentObjectGroupPython] O_element049  label="O_element : 6"  # scripted group (container) (typed FeaturePython)
  n = 6
  ref = O_element
FEATURE [App::DocumentObjectGroupPython] H_element045  label="H_element : 024"  # scripted group (container) (typed FeaturePython)
  n = 4
  ref = H_element
FEATURE [App::DocumentObjectGroupPython] G4_GYPSUM  # scripted group (container) (typed FeaturePython)
  Dunit = g/cm3
  Dvalue = 2.32
  Group = -> [Ca_element012,S_element014,O_element049,H_element045]
  conduct = 2
  density = 1
  expand = 3
  formula = G4_GYPSUM
  name = G4_GYPSUM
  specific = 4
FEATURE [App::DocumentObjectGroupPython] C_element052  label="C_element : 7"  # scripted group (container) (typed FeaturePython)
  n = 7
  ref = C_element
FEATURE [App::DocumentObjectGroupPython] H_element046  label="H_element : 16"  # scripted group (container) (typed FeaturePython)
  n = 16
  ref = H_element
FEATURE [App::DocumentObjectGroupPython] G4_N_HEPTANE  label="G4_N-HEPTANE"  # scripted group (container) (typed FeaturePython)
  Dunit = g/cm3
  Dvalue = 0.68376
  Group = -> [C_element052,H_element046]
  conduct = 2
  density = 1
  expand = 3
  formula = G4_N-HEPTANE
  name = G4_N-HEPTANE
  specific = 4
FEATURE [App::DocumentObjectGroupPython] C_element053  label="C_element : 029"  # scripted group (container) (typed FeaturePython)
  n = 6
  ref = C_element
FEATURE [App::DocumentObjectGroupPython] H_element047  label="H_element : 14"  # scripted group (container) (typed FeaturePython)
  n = 14
  ref = H_element
FEATURE [App::DocumentObjectGroupPython] G4_N_HEXANE  label="G4_N-HEXANE"  # scripted group (container) (typed FeaturePython)
  Dunit = g/cm3
  Dvalue = 0.6603
  Group = -> [C_element053,H_element047]
  conduct = 2
  density = 1
  expand = 3
  formula = G4_N-HEXANE
  name = G4_N-HEXANE
  specific = 4
FEATURE [App::DocumentObjectGroupPython] C_element054  label="C_element : 22"  # scripted group (container) (typed FeaturePython)
  n = 22
  ref = C_element
FEATURE [App::DocumentObjectGroupPython] H_element048  label="H_element : 025"  # scripted group (container) (typed FeaturePython)
  n = 10
  ref = H_element
FEATURE [App::DocumentObjectGroupPython] N_element021  label="N_element : 010"  # scripted group (container) (typed FeaturePython)
  n = 2
  ref = N_element
FEATURE [App::DocumentObjectGroupPython] O_element050  label="O_element : 025"  # scripted group (container) (typed FeaturePython)
  n = 5
  ref = O_element
FEATURE [App::DocumentObjectGroupPython] G4_KAPTON  # scripted group (container) (typed FeaturePython)
  Dunit = g/cm3
  Dvalue = 1.42
  Group = -> [C_element054,H_element048,N_element021,O_element050]
  conduct = 2
  density = 1
  expand = 3
  formula = G4_KAPTON
  name = G4_KAPTON
  specific = 4
FEATURE [App::DocumentObjectGroupPython] La_element001  label="La_element : 1"  # scripted group (container) (typed FeaturePython)
  n = 1
  ref = La_element
FEATURE [App::DocumentObjectGroupPython] Br_element003  label="Br_element : 002"  # scripted group (container) (typed FeaturePython)
  n = 1
  ref = Br_element
FEATURE [App::DocumentObjectGroupPython] O_element051  label="O_element : 026"  # scripted group (container) (typed FeaturePython)
  n = 1
  ref = O_element
FEATURE [App::DocumentObjectGroupPython] G4_LANTHANUM_OXYBROMIDE  # scripted group (container) (typed FeaturePython)
  Dunit = g/cm3
  Dvalue = 6.28
  Group = -> [La_element001,Br_element003,O_element051]
  conduct = 2
  density = 1
  expand = 3
  formula = G4_LANTHANUM_OXYBROMIDE
  name = G4_LANTHANUM_OXYBROMIDE
  specific = 4
FEATURE [App::DocumentObjectGroupPython] La_element002  label="La_element : 2"  # scripted group (container) (typed FeaturePython)
  n = 2
  ref = La_element
FEATURE [App::DocumentObjectGroupPython] O_element052  label="O_element : 027"  # scripted group (container) (typed FeaturePython)
  n = 2
  ref = O_element
FEATURE [App::DocumentObjectGroupPython] S_element015  label="S_element : 006"  # scripted group (container) (typed FeaturePython)
  n = 1
  ref = S_element
FEATURE [App::DocumentObjectGroupPython] G4_LANTHANUM_OXYSULFIDE  # scripted group (container) (typed FeaturePython)
  Dunit = g/cm3
  Dvalue = 5.86
  Group = -> [La_element002,O_element052,S_element015]
  conduct = 2
  density = 1
  expand = 3
  formula = G4_LANTHANUM_OXYSULFIDE
  name = G4_LANTHANUM_OXYSULFIDE
  specific = 4
FEATURE [App::DocumentObjectGroupPython] O_element053  label="O_element : 0.072"  # scripted group (container) (typed FeaturePython)
  n = 0.071682
FEATURE [App::DocumentObjectGroupPython] Pb_element002  label="Pb_element : 0.928"  # scripted group (container) (typed FeaturePython)
  n = 0.928318
FEATURE [App::DocumentObjectGroupPython] G4_LEAD_OXIDE  # scripted group (container) (typed FeaturePython)
  Dunit = g/cm3
  Dvalue = 9.53
  Group = -> [O_element053,Pb_element002]
  conduct = 2
  density = 1
  expand = 3
  formula = G4_LEAD_OXIDE
  name = G4_LEAD_OXIDE
  specific = 4
FEATURE [App::DocumentObjectGroupPython] Li_element001  label="Li_element : 1"  # scripted group (container) (typed FeaturePython)
  n = 1
  ref = Li_element
FEATURE [App::DocumentObjectGroupPython] N_element022  label="N_element : 011"  # scripted group (container) (typed FeaturePython)
  n = 1
  ref = N_element
FEATURE [App::DocumentObjectGroupPython] H_element049  label="H_element : 026"  # scripted group (container) (typed FeaturePython)
  n = 2
  ref = H_element
FEATURE [App::DocumentObjectGroupPython] G4_LITHIUM_AMIDE  # scripted group (container) (typed FeaturePython)
  Dunit = g/cm3
  Dvalue = 1.178
  Group = -> [Li_element001,N_element022,H_element049]
  conduct = 2
  density = 1
  expand = 3
  formula = G4_LITHIUM_AMIDE
  name = G4_LITHIUM_AMIDE
  specific = 4
FEATURE [App::DocumentObjectGroupPython] Li_element002  label="Li_element : 2"  # scripted group (container) (typed FeaturePython)
  n = 2
  ref = Li_element
FEATURE [App::DocumentObjectGroupPython] C_element055  label="C_element : 030"  # scripted group (container) (typed FeaturePython)
  n = 1
  ref = C_element
FEATURE [App::DocumentObjectGroupPython] O_element054  label="O_element : 028"  # scripted group (container) (typed FeaturePython)
  n = 3
  ref = O_element
FEATURE [App::DocumentObjectGroupPython] G4_LITHIUM_CARBONATE  # scripted group (container) (typed FeaturePython)
  Dunit = g/cm3
  Dvalue = 2.11
  Group = -> [Li_element002,C_element055,O_element054]
  conduct = 2
  density = 1
  expand = 3
  formula = G4_LITHIUM_CARBONATE
  name = G4_LITHIUM_CARBONATE
  specific = 4
FEATURE [App::DocumentObjectGroupPython] Li_element003  label="Li_element : 003"  # scripted group (container) (typed FeaturePython)
  n = 1
  ref = Li_element
FEATURE [App::DocumentObjectGroupPython] F_element012  label="F_element : 004"  # scripted group (container) (typed FeaturePython)
  n = 1
  ref = F_element
FEATURE [App::DocumentObjectGroupPython] G4_LITHIUM_FLUORIDE  # scripted group (container) (typed FeaturePython)
  Dunit = g/cm3
  Dvalue = 2.635
  Group = -> [Li_element003,F_element012]
  conduct = 2
  density = 1
  expand = 3
  formula = G4_LITHIUM_FLUORIDE
  name = G4_LITHIUM_FLUORIDE
  specific = 4
FEATURE [App::DocumentObjectGroupPython] Li_element004  label="Li_element : 004"  # scripted group (container) (typed FeaturePython)
  n = 1
  ref = Li_element
FEATURE [App::DocumentObjectGroupPython] H_element050  label="H_element : 027"  # scripted group (container) (typed FeaturePython)
  n = 1
  ref = H_element
FEATURE [App::DocumentObjectGroupPython] G4_LITHIUM_HYDRIDE  # scripted group (container) (typed FeaturePython)
  Dunit = g/cm3
  Dvalue = 0.82
  Group = -> [Li_element004,H_element050]
  conduct = 2
  density = 1
  expand = 3
  formula = G4_LITHIUM_HYDRIDE
  name = G4_LITHIUM_HYDRIDE
  specific = 4
FEATURE [App::DocumentObjectGroupPython] Li_element005  label="Li_element : 005"  # scripted group (container) (typed FeaturePython)
  n = 1
  ref = Li_element
FEATURE [App::DocumentObjectGroupPython] I_element003  label="I_element : 002"  # scripted group (container) (typed FeaturePython)
  n = 1
  ref = I_element
FEATURE [App::DocumentObjectGroupPython] G4_LITHIUM_IODIDE  # scripted group (container) (typed FeaturePython)
  Dunit = g/cm3
  Dvalue = 3.494
  Group = -> [Li_element005,I_element003]
  conduct = 2
  density = 1
  expand = 3
  formula = G4_LITHIUM_IODIDE
  name = G4_LITHIUM_IODIDE
  specific = 4
FEATURE [App::DocumentObjectGroupPython] Li_element006  label="Li_element : 006"  # scripted group (container) (typed FeaturePython)
  n = 2
  ref = Li_element
FEATURE [App::DocumentObjectGroupPython] O_element055  label="O_element : 029"  # scripted group (container) (typed FeaturePython)
  n = 1
  ref = O_element
FEATURE [App::DocumentObjectGroupPython] G4_LITHIUM_OXIDE  # scripted group (container) (typed FeaturePython)
  Dunit = g/cm3
  Dvalue = 2.013
  Group = -> [Li_element006,O_element055]
  conduct = 2
  density = 1
  expand = 3
  formula = G4_LITHIUM_OXIDE
  name = G4_LITHIUM_OXIDE
  specific = 4
FEATURE [App::DocumentObjectGroupPython] Li_element007  label="Li_element : 007"  # scripted group (container) (typed FeaturePython)
  n = 2
  ref = Li_element
FEATURE [App::DocumentObjectGroupPython] B_element005  label="B_element : 005"  # scripted group (container) (typed FeaturePython)
  n = 4
  ref = B_element
FEATURE [App::DocumentObjectGroupPython] O_element056  label="O_element : 7"  # scripted group (container) (typed FeaturePython)
  n = 7
  ref = O_element
FEATURE [App::DocumentObjectGroupPython] G4_LITHIUM_TETRABORATE  # scripted group (container) (typed FeaturePython)
  Dunit = g/cm3
  Dvalue = 2.44
  Group = -> [Li_element007,B_element005,O_element056]
  conduct = 2
  density = 1
  expand = 3
  formula = G4_LITHIUM_TETRABORATE
  name = G4_LITHIUM_TETRABORATE
  specific = 4
FEATURE [App::DocumentObjectGroupPython] H_element051  label="H_element : 0.105"  # scripted group (container) (typed FeaturePython)
  n = 0.105
FEATURE [App::DocumentObjectGroupPython] C_element056  label="C_element : 0.083"  # scripted group (container) (typed FeaturePython)
  n = 0.083
FEATURE [App::DocumentObjectGroupPython] N_element023  label="N_element : 0.023"  # scripted group (container) (typed FeaturePython)
  n = 0.023
FEATURE [App::DocumentObjectGroupPython] O_element057  label="O_element : 0.779"  # scripted group (container) (typed FeaturePython)
  n = 0.779
FEATURE [App::DocumentObjectGroupPython] Na_element010  label="Na_element : 0.097"  # scripted group (container) (typed FeaturePython)
  n = 0.002
FEATURE [App::DocumentObjectGroupPython] P_element006  label="P_element : 0.105"  # scripted group (container) (typed FeaturePython)
  n = 0.001
FEATURE [App::DocumentObjectGroupPython] S_element016  label="S_element : 0.017"  # scripted group (container) (typed FeaturePython)
  n = 0.002
FEATURE [App::DocumentObjectGroupPython] Cl_element014  label="Cl_element : 0.587"  # scripted group (container) (typed FeaturePython)
  n = 0.003
FEATURE [App::DocumentObjectGroupPython] K_element005  label="K_element : 0.015"  # scripted group (container) (typed FeaturePython)
  n = 0.002
FEATURE [App::DocumentObjectGroupPython] G4_LUNG_ICRP  # scripted group (container) (typed FeaturePython)
  Dunit = g/cm3
  Dvalue = 1.04
  Group = -> [H_element051,C_element056,N_element023,O_element057,Na_element010,P_element006,S_element016,Cl_element014,K_element005]
  conduct = 2
  density = 1
  expand = 3
  formula = G4_LUNG_ICRP
  name = G4_LUNG_ICRP
  specific = 4
FEATURE [App::DocumentObjectGroupPython] H_element052  label="H_element : 0.116"  # scripted group (container) (typed FeaturePython)
  n = 0.114318
FEATURE [App::DocumentObjectGroupPython] C_element057  label="C_element : 0.656"  # scripted group (container) (typed FeaturePython)
  n = 0.655824
FEATURE [App::DocumentObjectGroupPython] O_element058  label="O_element : 0.092"  # scripted group (container) (typed FeaturePython)
  n = 0.0921831
FEATURE [App::DocumentObjectGroupPython] Mg_element004  label="Mg_element : 0.135"  # scripted group (container) (typed FeaturePython)
  n = 0.134792
FEATURE [App::DocumentObjectGroupPython] Ca_element013  label="Ca_element : 0.003"  # scripted group (container) (typed FeaturePython)
  n = 0.002883
FEATURE [App::DocumentObjectGroupPython] G4_M3_WAX  # scripted group (container) (typed FeaturePython)
  Dunit = g/cm3
  Dvalue = 1.05
  Group = -> [H_element052,C_element057,O_element058,Mg_element004,Ca_element013]
  conduct = 2
  density = 1
  expand = 3
  formula = G4_M3_WAX
  name = G4_M3_WAX
  specific = 4
FEATURE [App::DocumentObjectGroupPython] Mg_element005  label="Mg_element : 1"  # scripted group (container) (typed FeaturePython)
  n = 1
  ref = Mg_element
FEATURE [App::DocumentObjectGroupPython] C_element058  label="C_element : 031"  # scripted group (container) (typed FeaturePython)
  n = 1
  ref = C_element
FEATURE [App::DocumentObjectGroupPython] O_element059  label="O_element : 030"  # scripted group (container) (typed FeaturePython)
  n = 3
  ref = O_element
FEATURE [App::DocumentObjectGroupPython] G4_MAGNESIUM_CARBONATE  # scripted group (container) (typed FeaturePython)
  Dunit = g/cm3
  Dvalue = 2.958
  Group = -> [Mg_element005,C_element058,O_element059]
  conduct = 2
  density = 1
  expand = 3
  formula = G4_MAGNESIUM_CARBONATE
  name = G4_MAGNESIUM_CARBONATE
  specific = 4
FEATURE [App::DocumentObjectGroupPython] Mg_element006  label="Mg_element : 002"  # scripted group (container) (typed FeaturePython)
  n = 1
  ref = Mg_element
FEATURE [App::DocumentObjectGroupPython] F_element013  label="F_element : 005"  # scripted group (container) (typed FeaturePython)
  n = 2
  ref = F_element
FEATURE [App::DocumentObjectGroupPython] G4_MAGNESIUM_FLUORIDE  # scripted group (container) (typed FeaturePython)
  Dunit = g/cm3
  Dvalue = 3
  Group = -> [Mg_element006,F_element013]
  conduct = 2
  density = 1
  expand = 3
  formula = G4_MAGNESIUM_FLUORIDE
  name = G4_MAGNESIUM_FLUORIDE
  specific = 4
FEATURE [App::DocumentObjectGroupPython] Mg_element007  label="Mg_element : 003"  # scripted group (container) (typed FeaturePython)
  n = 1
  ref = Mg_element
FEATURE [App::DocumentObjectGroupPython] O_element060  label="O_element : 031"  # scripted group (container) (typed FeaturePython)
  n = 1
  ref = O_element
FEATURE [App::DocumentObjectGroupPython] G4_MAGNESIUM_OXIDE  # scripted group (container) (typed FeaturePython)
  Dunit = g/cm3
  Dvalue = 3.58
  Group = -> [Mg_element007,O_element060]
  conduct = 2
  density = 1
  expand = 3
  formula = G4_MAGNESIUM_OXIDE
  name = G4_MAGNESIUM_OXIDE
  specific = 4
FEATURE [App::DocumentObjectGroupPython] Mg_element008  label="Mg_element : 004"  # scripted group (container) (typed FeaturePython)
  n = 1
  ref = Mg_element
FEATURE [App::DocumentObjectGroupPython] B_element006  label="B_element : 006"  # scripted group (container) (typed FeaturePython)
  n = 4
  ref = B_element
FEATURE [App::DocumentObjectGroupPython] O_element061  label="O_element : 032"  # scripted group (container) (typed FeaturePython)
  n = 7
  ref = O_element
FEATURE [App::DocumentObjectGroupPython] G4_MAGNESIUM_TETRABORATE  # scripted group (container) (typed FeaturePython)
  Dunit = g/cm3
  Dvalue = 2.53
  Group = -> [Mg_element008,B_element006,O_element061]
  conduct = 2
  density = 1
  expand = 3
  formula = G4_MAGNESIUM_TETRABORATE
  name = G4_MAGNESIUM_TETRABORATE
  specific = 4
FEATURE [App::DocumentObjectGroupPython] Hg_element001  label="Hg_element : 1"  # scripted group (container) (typed FeaturePython)
  n = 1
  ref = Hg_element
FEATURE [App::DocumentObjectGroupPython] I_element004  label="I_element : 2"  # scripted group (container) (typed FeaturePython)
  n = 2
  ref = I_element
FEATURE [App::DocumentObjectGroupPython] G4_MERCURIC_IODIDE  # scripted group (container) (typed FeaturePython)
  Dunit = g/cm3
  Dvalue = 6.36
  Group = -> [Hg_element001,I_element004]
  conduct = 2
  density = 1
  expand = 3
  formula = G4_MERCURIC_IODIDE
  name = G4_MERCURIC_IODIDE
  specific = 4
FEATURE [App::DocumentObjectGroupPython] C_element059  label="C_element : 032"  # scripted group (container) (typed FeaturePython)
  n = 1
  ref = C_element
FEATURE [App::DocumentObjectGroupPython] H_element053  label="H_element : 028"  # scripted group (container) (typed FeaturePython)
  n = 4
  ref = H_element
FEATURE [App::DocumentObjectGroupPython] G4_METHANE  # scripted group (container) (typed FeaturePython)
  Dunit = g/cm3
  Dvalue = 0.000667151
  Group = -> [C_element059,H_element053]
  conduct = 2
  density = 1
  expand = 3
  formula = G4_METHANE
  name = G4_METHANE
  specific = 4
FEATURE [App::DocumentObjectGroupPython] C_element060  label="C_element : 033"  # scripted group (container) (typed FeaturePython)
  n = 1
  ref = C_element
FEATURE [App::DocumentObjectGroupPython] H_element054  label="H_element : 029"  # scripted group (container) (typed FeaturePython)
  n = 4
  ref = H_element
FEATURE [App::DocumentObjectGroupPython] O_element062  label="O_element : 033"  # scripted group (container) (typed FeaturePython)
  n = 1
  ref = O_element
FEATURE [App::DocumentObjectGroupPython] G4_METHANOL  # scripted group (container) (typed FeaturePython)
  Dunit = g/cm3
  Dvalue = 0.7914
  Group = -> [C_element060,H_element054,O_element062]
  conduct = 2
  density = 1
  expand = 3
  formula = G4_METHANOL
  name = G4_METHANOL
  specific = 4
FEATURE [App::DocumentObjectGroupPython] H_element055  label="H_element : 0.134"  # scripted group (container) (typed FeaturePython)
  n = 0.13404
FEATURE [App::DocumentObjectGroupPython] C_element061  label="C_element : 0.778"  # scripted group (container) (typed FeaturePython)
  n = 0.77796
FEATURE [App::DocumentObjectGroupPython] O_element063  label="O_element : 0.035"  # scripted group (container) (typed FeaturePython)
  n = 0.03502
FEATURE [App::DocumentObjectGroupPython] Mg_element009  label="Mg_element : 0.039"  # scripted group (container) (typed FeaturePython)
  n = 0.038594
FEATURE [App::DocumentObjectGroupPython] Ti_element002  label="Ti_element : 0.014"  # scripted group (container) (typed FeaturePython)
  n = 0.014386
FEATURE [App::DocumentObjectGroupPython] G4_MIX_D_WAX  # scripted group (container) (typed FeaturePython)
  Dunit = g/cm3
  Dvalue = 0.99
  Group = -> [H_element055,C_element061,O_element063,Mg_element009,Ti_element002]
  conduct = 2
  density = 1
  expand = 3
  formula = G4_MIX_D_WAX
  name = G4_MIX_D_WAX
  specific = 4
FEATURE [App::DocumentObjectGroupPython] H_element056  label="H_element : 0.135"  # scripted group (container) (typed FeaturePython)
  n = 0.081192
FEATURE [App::DocumentObjectGroupPython] C_element062  label="C_element : 0.583"  # scripted group (container) (typed FeaturePython)
  n = 0.583442
FEATURE [App::DocumentObjectGroupPython] N_element024  label="N_element : 0.018"  # scripted group (container) (typed FeaturePython)
  n = 0.017798
FEATURE [App::DocumentObjectGroupPython] O_element064  label="O_element : 0.186"  # scripted group (container) (typed FeaturePython)
  n = 0.186381
FEATURE [App::DocumentObjectGroupPython] Mg_element010  label="Mg_element : 0.130"  # scripted group (container) (typed FeaturePython)
  n = 0.130287
FEATURE [App::DocumentObjectGroupPython] Cl_element015  label="Cl_element : 0.588"  # scripted group (container) (typed FeaturePython)
  n = 0.0009
FEATURE [App::DocumentObjectGroupPython] G4_MS20_TISSUE  # scripted group (container) (typed FeaturePython)
  Dunit = g/cm3
  Dvalue = 1
  Group = -> [H_element056,C_element062,N_element024,O_element064,Mg_element010,Cl_element015]
  conduct = 2
  density = 1
  expand = 3
  formula = G4_MS20_TISSUE
  name = G4_MS20_TISSUE
  specific = 4
FEATURE [App::DocumentObjectGroupPython] H_element057  label="H_element : 0.136"  # scripted group (container) (typed FeaturePython)
  n = 0.102
FEATURE [App::DocumentObjectGroupPython] C_element063  label="C_element : 0.143"  # scripted group (container) (typed FeaturePython)
  n = 0.143
FEATURE [App::DocumentObjectGroupPython] N_element025  label="N_element : 0.034"  # scripted group (container) (typed FeaturePython)
  n = 0.034
FEATURE [App::DocumentObjectGroupPython] O_element065  label="O_element : 0.710"  # scripted group (container) (typed FeaturePython)
  n = 0.71
FEATURE [App::DocumentObjectGroupPython] Na_element011  label="Na_element : 0.098"  # scripted group (container) (typed FeaturePython)
  n = 0.001
FEATURE [App::DocumentObjectGroupPython] P_element007  label="P_element : 0.002"  # scripted group (container) (typed FeaturePython)
  n = 0.002
FEATURE [App::DocumentObjectGroupPython] S_element017  label="S_element : 0.018"  # scripted group (container) (typed FeaturePython)
  n = 0.003
FEATURE [App::DocumentObjectGroupPython] Cl_element016  label="Cl_element : 0.589"  # scripted group (container) (typed FeaturePython)
  n = 0.001
FEATURE [App::DocumentObjectGroupPython] K_element006  label="K_element : 0.004"  # scripted group (container) (typed FeaturePython)
  n = 0.004
FEATURE [App::DocumentObjectGroupPython] G4_MUSCLE_SKELETAL_ICRP  # scripted group (container) (typed FeaturePython)
  Dunit = g/cm3
  Dvalue = 1.05
  Group = -> [H_element057,C_element063,N_element025,O_element065,Na_element011,P_element007,S_element017,Cl_element016,K_element006]
  conduct = 2
  density = 1
  expand = 3
  formula = G4_MUSCLE_SKELETAL_ICRP
  name = G4_MUSCLE_SKELETAL_ICRP
  specific = 4
FEATURE [App::DocumentObjectGroupPython] H_element058  label="H_element : 0.137"  # scripted group (container) (typed FeaturePython)
  n = 0.102102
FEATURE [App::DocumentObjectGroupPython] C_element064  label="C_element : 0.123"  # scripted group (container) (typed FeaturePython)
  n = 0.123123
FEATURE [App::DocumentObjectGroupPython] N_element026  label="N_element : 0.756"  # scripted group (container) (typed FeaturePython)
  n = 0.035035
FEATURE [App::DocumentObjectGroupPython] O_element066  label="O_element : 0.730"  # scripted group (container) (typed FeaturePython)
  n = 0.72973
FEATURE [App::DocumentObjectGroupPython] Na_element012  label="Na_element : 0.099"  # scripted group (container) (typed FeaturePython)
  n = 0.001001
FEATURE [App::DocumentObjectGroupPython] P_element008  label="P_element : 0.106"  # scripted group (container) (typed FeaturePython)
  n = 0.002002
FEATURE [App::DocumentObjectGroupPython] S_element018  label="S_element : 0.019"  # scripted group (container) (typed FeaturePython)
  n = 0.004004
FEATURE [App::DocumentObjectGroupPython] K_element007  label="K_element : 0.016"  # scripted group (container) (typed FeaturePython)
  n = 0.003003
FEATURE [App::DocumentObjectGroupPython] G4_MUSCLE_STRIATED_ICRU  # scripted group (container) (typed FeaturePython)
  Dunit = g/cm3
  Dvalue = 1.04
  Group = -> [H_element058,C_element064,N_element026,O_element066,Na_element012,P_element008,S_element018,K_element007]
  conduct = 2
  density = 1
  expand = 3
  formula = G4_MUSCLE_STRIATED_ICRU
  name = G4_MUSCLE_STRIATED_ICRU
  specific = 4
FEATURE [App::DocumentObjectGroupPython] H_element059  label="H_element : 0.098"  # scripted group (container) (typed FeaturePython)
  n = 0.0982341
FEATURE [App::DocumentObjectGroupPython] C_element065  label="C_element : 0.156"  # scripted group (container) (typed FeaturePython)
  n = 0.156214
FEATURE [App::DocumentObjectGroupPython] N_element027  label="N_element : 0.757"  # scripted group (container) (typed FeaturePython)
  n = 0.035451
FEATURE [App::DocumentObjectGroupPython] O_element067  label="O_element : 0.880"  # scripted group (container) (typed FeaturePython)
  n = 0.710101
FEATURE [App::DocumentObjectGroupPython] G4_MUSCLE_WITH_SUCROSE  # scripted group (container) (typed FeaturePython)
  Dunit = g/cm3
  Dvalue = 1.11
  Group = -> [H_element059,C_element065,N_element027,O_element067]
  conduct = 2
  density = 1
  expand = 3
  formula = G4_MUSCLE_WITH_SUCROSE
  name = G4_MUSCLE_WITH_SUCROSE
  specific = 4
FEATURE [App::DocumentObjectGroupPython] H_element060  label="H_element : 0.138"  # scripted group (container) (typed FeaturePython)
  n = 0.101969
FEATURE [App::DocumentObjectGroupPython] C_element066  label="C_element : 0.120"  # scripted group (container) (typed FeaturePython)
  n = 0.120058
FEATURE [App::DocumentObjectGroupPython] N_element028  label="N_element : 0.758"  # scripted group (container) (typed FeaturePython)
  n = 0.035451
FEATURE [App::DocumentObjectGroupPython] O_element068  label="O_element : 0.743"  # scripted group (container) (typed FeaturePython)
  n = 0.742522
FEATURE [App::DocumentObjectGroupPython] G4_MUSCLE_WITHOUT_SUCROSE  # scripted group (container) (typed FeaturePython)
  Dunit = g/cm3
  Dvalue = 1.07
  Group = -> [H_element060,C_element066,N_element028,O_element068]
  conduct = 2
  density = 1
  expand = 3
  formula = G4_MUSCLE_WITHOUT_SUCROSE
  name = G4_MUSCLE_WITHOUT_SUCROSE
  specific = 4
FEATURE [App::DocumentObjectGroupPython] C_element067  label="C_element : 10"  # scripted group (container) (typed FeaturePython)
  n = 10
  ref = C_element
FEATURE [App::DocumentObjectGroupPython] H_element061  label="H_element : 030"  # scripted group (container) (typed FeaturePython)
  n = 8
  ref = H_element
FEATURE [App::DocumentObjectGroupPython] G4_NAPHTHALENE  # scripted group (container) (typed FeaturePython)
  Dunit = g/cm3
  Dvalue = 1.145
  Group = -> [C_element067,H_element061]
  conduct = 2
  density = 1
  expand = 3
  formula = G4_NAPHTHALENE
  name = G4_NAPHTHALENE
  specific = 4
FEATURE [App::DocumentObjectGroupPython] C_element068  label="C_element : 034"  # scripted group (container) (typed FeaturePython)
  n = 6
  ref = C_element
FEATURE [App::DocumentObjectGroupPython] H_element062  label="H_element : 031"  # scripted group (container) (typed FeaturePython)
  n = 5
  ref = H_element
FEATURE [App::DocumentObjectGroupPython] N_element029  label="N_element : 012"  # scripted group (container) (typed FeaturePython)
  n = 1
  ref = N_element
FEATURE [App::DocumentObjectGroupPython] O_element069  label="O_element : 034"  # scripted group (container) (typed FeaturePython)
  n = 2
  ref = O_element
FEATURE [App::DocumentObjectGroupPython] G4_NITROBENZENE  # scripted group (container) (typed FeaturePython)
  Dunit = g/cm3
  Dvalue = 1.19867
  Group = -> [C_element068,H_element062,N_element029,O_element069]
  conduct = 2
  density = 1
  expand = 3
  formula = G4_NITROBENZENE
  name = G4_NITROBENZENE
  specific = 4
FEATURE [App::DocumentObjectGroupPython] N_element030  label="N_element : 013"  # scripted group (container) (typed FeaturePython)
  n = 2
  ref = N_element
FEATURE [App::DocumentObjectGroupPython] O_element070  label="O_element : 035"  # scripted group (container) (typed FeaturePython)
  n = 1
  ref = O_element
FEATURE [App::DocumentObjectGroupPython] G4_NITROUS_OXIDE  # scripted group (container) (typed FeaturePython)
  Dunit = g/cm3
  Dvalue = 0.00183094
  Group = -> [N_element030,O_element070]
  conduct = 2
  density = 1
  expand = 3
  formula = G4_NITROUS_OXIDE
  name = G4_NITROUS_OXIDE
  specific = 4
FEATURE [App::DocumentObjectGroupPython] H_element063  label="H_element : 0.104"  # scripted group (container) (typed FeaturePython)
  n = 0.103509
FEATURE [App::DocumentObjectGroupPython] C_element069  label="C_element : 0.648"  # scripted group (container) (typed FeaturePython)
  n = 0.648416
FEATURE [App::DocumentObjectGroupPython] N_element031  label="N_element : 0.100"  # scripted group (container) (typed FeaturePython)
  n = 0.0995361
FEATURE [App::DocumentObjectGroupPython] O_element071  label="O_element : 0.149"  # scripted group (container) (typed FeaturePython)
  n = 0.148539
FEATURE [App::DocumentObjectGroupPython] G4_NYLON_8062  label="G4_NYLON-8062"  # scripted group (container) (typed FeaturePython)
  Dunit = g/cm3
  Dvalue = 1.08
  Group = -> [H_element063,C_element069,N_element031,O_element071]
  conduct = 2
  density = 1
  expand = 3
  formula = G4_NYLON-8062
  name = G4_NYLON-8062
  specific = 4
FEATURE [App::DocumentObjectGroupPython] C_element070  label="C_element : 035"  # scripted group (container) (typed FeaturePython)
  n = 6
  ref = C_element
FEATURE [App::DocumentObjectGroupPython] H_element064  label="H_element : 11"  # scripted group (container) (typed FeaturePython)
  n = 11
  ref = H_element
FEATURE [App::DocumentObjectGroupPython] N_element032  label="N_element : 014"  # scripted group (container) (typed FeaturePython)
  n = 1
  ref = N_element
FEATURE [App::DocumentObjectGroupPython] O_element072  label="O_element : 036"  # scripted group (container) (typed FeaturePython)
  n = 1
  ref = O_element
FEATURE [App::DocumentObjectGroupPython] G4_NYLON_6_6  label="G4_NYLON-6-6"  # scripted group (container) (typed FeaturePython)
  Dunit = g/cm3
  Dvalue = 1.14
  Group = -> [C_element070,H_element064,N_element032,O_element072]
  conduct = 2
  density = 1
  expand = 3
  formula = G4_NYLON-6-6
  name = G4_NYLON-6-6
  specific = 4
FEATURE [App::DocumentObjectGroupPython] H_element065  label="H_element : 0.139"  # scripted group (container) (typed FeaturePython)
  n = 0.107062
FEATURE [App::DocumentObjectGroupPython] C_element071  label="C_element : 0.680"  # scripted group (container) (typed FeaturePython)
  n = 0.680449
FEATURE [App::DocumentObjectGroupPython] N_element033  label="N_element : 0.099"  # scripted group (container) (typed FeaturePython)
  n = 0.099189
FEATURE [App::DocumentObjectGroupPython] O_element073  label="O_element : 0.113"  # scripted group (container) (typed FeaturePython)
  n = 0.1133
FEATURE [App::DocumentObjectGroupPython] G4_NYLON_6_10  label="G4_NYLON-6-10"  # scripted group (container) (typed FeaturePython)
  Dunit = g/cm3
  Dvalue = 1.14
  Group = -> [H_element065,C_element071,N_element033,O_element073]
  conduct = 2
  density = 1
  expand = 3
  formula = G4_NYLON-6-10
  name = G4_NYLON-6-10
  specific = 4
FEATURE [App::DocumentObjectGroupPython] H_element066  label="H_element : 0.140"  # scripted group (container) (typed FeaturePython)
  n = 0.115476
FEATURE [App::DocumentObjectGroupPython] C_element072  label="C_element : 0.721"  # scripted group (container) (typed FeaturePython)
  n = 0.720818
FEATURE [App::DocumentObjectGroupPython] N_element034  label="N_element : 0.076"  # scripted group (container) (typed FeaturePython)
  n = 0.0764169
FEATURE [App::DocumentObjectGroupPython] O_element074  label="O_element : 0.087"  # scripted group (container) (typed FeaturePython)
  n = 0.0872889
FEATURE [App::DocumentObjectGroupPython] G4_NYLON_11_RILSAN  label="G4_NYLON-11_RILSAN"  # scripted group (container) (typed FeaturePython)
  Dunit = g/cm3
  Dvalue = 1.425
  Group = -> [H_element066,C_element072,N_element034,O_element074]
  conduct = 2
  density = 1
  expand = 3
  formula = G4_NYLON-11_RILSAN
  name = G4_NYLON-11_RILSAN
  specific = 4
FEATURE [App::DocumentObjectGroupPython] C_element073  label="C_element : 8"  # scripted group (container) (typed FeaturePython)
  n = 8
  ref = C_element
FEATURE [App::DocumentObjectGroupPython] H_element067  label="H_element : 18"  # scripted group (container) (typed FeaturePython)
  n = 18
  ref = H_element
FEATURE [App::DocumentObjectGroupPython] G4_OCTANE  # scripted group (container) (typed FeaturePython)
  Dunit = g/cm3
  Dvalue = 0.7026
  Group = -> [C_element073,H_element067]
  conduct = 2
  density = 1
  expand = 3
  formula = G4_OCTANE
  name = G4_OCTANE
  specific = 4
FEATURE [App::DocumentObjectGroupPython] C_element074  label="C_element : 25"  # scripted group (container) (typed FeaturePython)
  n = 25
  ref = C_element
FEATURE [App::DocumentObjectGroupPython] H_element068  label="H_element : 52"  # scripted group (container) (typed FeaturePython)
  n = 52
  ref = H_element
FEATURE [App::DocumentObjectGroupPython] G4_PARAFFIN  # scripted group (container) (typed FeaturePython)
  Dunit = g/cm3
  Dvalue = 0.93
  Group = -> [C_element074,H_element068]
  conduct = 2
  density = 1
  expand = 3
  formula = G4_PARAFFIN
  name = G4_PARAFFIN
  specific = 4
FEATURE [App::DocumentObjectGroupPython] C_element075  label="C_element : 036"  # scripted group (container) (typed FeaturePython)
  n = 5
  ref = C_element
FEATURE [App::DocumentObjectGroupPython] H_element069  label="H_element : 032"  # scripted group (container) (typed FeaturePython)
  n = 12
  ref = H_element
FEATURE [App::DocumentObjectGroupPython] G4_N_PENTANE  label="G4_N-PENTANE"  # scripted group (container) (typed FeaturePython)
  Dunit = g/cm3
  Dvalue = 0.6262
  Group = -> [C_element075,H_element069]
  conduct = 2
  density = 1
  expand = 3
  formula = G4_N-PENTANE
  name = G4_N-PENTANE
  specific = 4
FEATURE [App::DocumentObjectGroupPython] H_element070  label="H_element : 0.014"  # scripted group (container) (typed FeaturePython)
  n = 0.0141
FEATURE [App::DocumentObjectGroupPython] C_element076  label="C_element : 0.072"  # scripted group (container) (typed FeaturePython)
  n = 0.072261
FEATURE [App::DocumentObjectGroupPython] N_element035  label="N_element : 0.019"  # scripted group (container) (typed FeaturePython)
  n = 0.01932
FEATURE [App::DocumentObjectGroupPython] O_element075  label="O_element : 0.066"  # scripted group (container) (typed FeaturePython)
  n = 0.066101
FEATURE [App::DocumentObjectGroupPython] S_element019  label="S_element : 0.020"  # scripted group (container) (typed FeaturePython)
  n = 0.00189
FEATURE [App::DocumentObjectGroupPython] Br_element004  label="Br_element : 0.349"  # scripted group (container) (typed FeaturePython)
  n = 0.349103
FEATURE [App::DocumentObjectGroupPython] Ag_element001  label="Ag_element : 0.474"  # scripted group (container) (typed FeaturePython)
  n = 0.474105
FEATURE [App::DocumentObjectGroupPython] I_element005  label="I_element : 0.003"  # scripted group (container) (typed FeaturePython)
  n = 0.00312
FEATURE [App::DocumentObjectGroupPython] G4_PHOTO_EMULSION  # scripted group (container) (typed FeaturePython)
  Dunit = g/cm3
  Dvalue = 3.815
  Group = -> [H_element070,C_element076,N_element035,O_element075,S_element019,Br_element004,Ag_element001,I_element005]
  conduct = 2
  density = 1
  expand = 3
  formula = G4_PHOTO_EMULSION
  name = G4_PHOTO_EMULSION
  specific = 4
FEATURE [App::DocumentObjectGroupPython] C_element077  label="C_element : 9"  # scripted group (container) (typed FeaturePython)
  n = 9
  ref = C_element
FEATURE [App::DocumentObjectGroupPython] H_element071  label="H_element : 033"  # scripted group (container) (typed FeaturePython)
  n = 10
  ref = H_element
FEATURE [App::DocumentObjectGroupPython] G4_PLASTIC_SC_VINYLTOLUENE  # scripted group (container) (typed FeaturePython)
  Dunit = g/cm3
  Dvalue = 1.032
  Group = -> [C_element077,H_element071]
  conduct = 2
  density = 1
  expand = 3
  formula = G4_PLASTIC_SC_VINYLTOLUENE
  name = G4_PLASTIC_SC_VINYLTOLUENE
  specific = 4
FEATURE [App::DocumentObjectGroupPython] Pu_element001  label="Pu_element : 1"  # scripted group (container) (typed FeaturePython)
  n = 1
  ref = Pu_element
FEATURE [App::DocumentObjectGroupPython] O_element076  label="O_element : 037"  # scripted group (container) (typed FeaturePython)
  n = 2
  ref = O_element
FEATURE [App::DocumentObjectGroupPython] G4_PLUTONIUM_DIOXIDE  # scripted group (container) (typed FeaturePython)
  Dunit = g/cm3
  Dvalue = 11.46
  Group = -> [Pu_element001,O_element076]
  conduct = 2
  density = 1
  expand = 3
  formula = G4_PLUTONIUM_DIOXIDE
  name = G4_PLUTONIUM_DIOXIDE
  specific = 4
FEATURE [App::DocumentObjectGroupPython] C_element078  label="C_element : 037"  # scripted group (container) (typed FeaturePython)
  n = 3
  ref = C_element
FEATURE [App::DocumentObjectGroupPython] H_element072  label="H_element : 034"  # scripted group (container) (typed FeaturePython)
  n = 3
  ref = H_element
FEATURE [App::DocumentObjectGroupPython] N_element036  label="N_element : 015"  # scripted group (container) (typed FeaturePython)
  n = 1
  ref = N_element
FEATURE [App::DocumentObjectGroupPython] G4_POLYACRYLONITRILE  # scripted group (container) (typed FeaturePython)
  Dunit = g/cm3
  Dvalue = 1.17
  Group = -> [C_element078,H_element072,N_element036]
  conduct = 2
  density = 1
  expand = 3
  formula = G4_POLYACRYLONITRILE
  name = G4_POLYACRYLONITRILE
  specific = 4
FEATURE [App::DocumentObjectGroupPython] C_element079  label="C_element : 16"  # scripted group (container) (typed FeaturePython)
  n = 16
  ref = C_element
FEATURE [App::DocumentObjectGroupPython] H_element073  label="H_element : 035"  # scripted group (container) (typed FeaturePython)
  n = 14
  ref = H_element
FEATURE [App::DocumentObjectGroupPython] O_element077  label="O_element : 038"  # scripted group (container) (typed FeaturePython)
  n = 3
  ref = O_element
FEATURE [App::DocumentObjectGroupPython] G4_POLYCARBONATE  # scripted group (container) (typed FeaturePython)
  Dunit = g/cm3
  Dvalue = 1.2
  Group = -> [C_element079,H_element073,O_element077]
  conduct = 2
  density = 1
  expand = 3
  formula = G4_POLYCARBONATE
  name = G4_POLYCARBONATE
  specific = 4
FEATURE [App::DocumentObjectGroupPython] C_element080  label="C_element : 038"  # scripted group (container) (typed FeaturePython)
  n = 8
  ref = C_element
FEATURE [App::DocumentObjectGroupPython] H_element074  label="H_element : 036"  # scripted group (container) (typed FeaturePython)
  n = 7
  ref = H_element
FEATURE [App::DocumentObjectGroupPython] Cl_element017  label="Cl_element : 007"  # scripted group (container) (typed FeaturePython)
  n = 1
  ref = Cl_element
FEATURE [App::DocumentObjectGroupPython] G4_POLYCHLOROSTYRENE  # scripted group (container) (typed FeaturePython)
  Dunit = g/cm3
  Dvalue = 1.3
  Group = -> [C_element080,H_element074,Cl_element017]
  conduct = 2
  density = 1
  expand = 3
  formula = G4_POLYCHLOROSTYRENE
  name = G4_POLYCHLOROSTYRENE
  specific = 4
FEATURE [App::DocumentObjectGroupPython] C_element081  label="C_element : 039"  # scripted group (container) (typed FeaturePython)
  n = 1
  ref = C_element
FEATURE [App::DocumentObjectGroupPython] H_element075  label="H_element : 037"  # scripted group (container) (typed FeaturePython)
  n = 2
  ref = H_element
FEATURE [App::DocumentObjectGroupPython] G4_POLYETHYLENE  # scripted group (container) (typed FeaturePython)
  Dunit = g/cm3
  Dvalue = 0.94
  Group = -> [C_element081,H_element075]
  conduct = 2
  density = 1
  expand = 3
  formula = G4_POLYETHYLENE
  name = G4_POLYETHYLENE
  specific = 4
FEATURE [App::DocumentObjectGroupPython] C_element082  label="C_element : 040"  # scripted group (container) (typed FeaturePython)
  n = 10
  ref = C_element
FEATURE [App::DocumentObjectGroupPython] H_element076  label="H_element : 038"  # scripted group (container) (typed FeaturePython)
  n = 8
  ref = H_element
FEATURE [App::DocumentObjectGroupPython] O_element078  label="O_element : 039"  # scripted group (container) (typed FeaturePython)
  n = 4
  ref = O_element
FEATURE [App::DocumentObjectGroupPython] G4_MYLAR  # scripted group (container) (typed FeaturePython)
  Dunit = g/cm3
  Dvalue = 1.4
  Group = -> [C_element082,H_element076,O_element078]
  conduct = 2
  density = 1
  expand = 3
  formula = G4_MYLAR
  name = G4_MYLAR
  specific = 4
FEATURE [App::DocumentObjectGroupPython] C_element083  label="C_element : 041"  # scripted group (container) (typed FeaturePython)
  n = 5
  ref = C_element
FEATURE [App::DocumentObjectGroupPython] H_element077  label="H_element : 039"  # scripted group (container) (typed FeaturePython)
  n = 8
  ref = H_element
FEATURE [App::DocumentObjectGroupPython] O_element079  label="O_element : 040"  # scripted group (container) (typed FeaturePython)
  n = 2
  ref = O_element
FEATURE [App::DocumentObjectGroupPython] G4_PLEXIGLASS  # scripted group (container) (typed FeaturePython)
  Dunit = g/cm3
  Dvalue = 1.19
  Group = -> [C_element083,H_element077,O_element079]
  conduct = 2
  density = 1
  expand = 3
  formula = G4_PLEXIGLASS
  name = G4_PLEXIGLASS
  specific = 4
FEATURE [App::DocumentObjectGroupPython] C_element084  label="C_element : 042"  # scripted group (container) (typed FeaturePython)
  n = 1
  ref = C_element
FEATURE [App::DocumentObjectGroupPython] H_element078  label="H_element : 040"  # scripted group (container) (typed FeaturePython)
  n = 2
  ref = H_element
FEATURE [App::DocumentObjectGroupPython] O_element080  label="O_element : 041"  # scripted group (container) (typed FeaturePython)
  n = 1
  ref = O_element
FEATURE [App::DocumentObjectGroupPython] G4_POLYOXYMETHYLENE  # scripted group (container) (typed FeaturePython)
  Dunit = g/cm3
  Dvalue = 1.425
  Group = -> [C_element084,H_element078,O_element080]
  conduct = 2
  density = 1
  expand = 3
  formula = G4_POLYOXYMETHYLENE
  name = G4_POLYOXYMETHYLENE
  specific = 4
FEATURE [App::DocumentObjectGroupPython] C_element085  label="C_element : 043"  # scripted group (container) (typed FeaturePython)
  n = 2
  ref = C_element
FEATURE [App::DocumentObjectGroupPython] H_element079  label="H_element : 041"  # scripted group (container) (typed FeaturePython)
  n = 4
  ref = H_element
FEATURE [App::DocumentObjectGroupPython] G4_POLYPROPYLENE  # scripted group (container) (typed FeaturePython)
  Dunit = g/cm3
  Dvalue = 0.9
  Group = -> [C_element085,H_element079]
  conduct = 2
  density = 1
  expand = 3
  formula = G4_POLYPROPYLENE
  name = G4_POLYPROPYLENE
  specific = 4
FEATURE [App::DocumentObjectGroupPython] C_element086  label="C_element : 044"  # scripted group (container) (typed FeaturePython)
  n = 8
  ref = C_element
FEATURE [App::DocumentObjectGroupPython] H_element080  label="H_element : 042"  # scripted group (container) (typed FeaturePython)
  n = 8
  ref = H_element
FEATURE [App::DocumentObjectGroupPython] G4_POLYSTYRENE  # scripted group (container) (typed FeaturePython)
  Dunit = g/cm3
  Dvalue = 1.06
  Group = -> [C_element086,H_element080]
  conduct = 2
  density = 1
  expand = 3
  formula = G4_POLYSTYRENE
  name = G4_POLYSTYRENE
  specific = 4
FEATURE [App::DocumentObjectGroupPython] C_element087  label="C_element : 045"  # scripted group (container) (typed FeaturePython)
  n = 2
  ref = C_element
FEATURE [App::DocumentObjectGroupPython] F_element014  label="F_element : 4"  # scripted group (container) (typed FeaturePython)
  n = 4
  ref = F_element
FEATURE [App::DocumentObjectGroupPython] G4_TEFLON  # scripted group (container) (typed FeaturePython)
  Dunit = g/cm3
  Dvalue = 2.2
  Group = -> [C_element087,F_element014]
  conduct = 2
  density = 1
  expand = 3
  formula = G4_TEFLON
  name = G4_TEFLON
  specific = 4
FEATURE [App::DocumentObjectGroupPython] C_element088  label="C_element : 046"  # scripted group (container) (typed FeaturePython)
  n = 2
  ref = C_element
FEATURE [App::DocumentObjectGroupPython] F_element015  label="F_element : 006"  # scripted group (container) (typed FeaturePython)
  n = 3
  ref = F_element
FEATURE [App::DocumentObjectGroupPython] Cl_element018  label="Cl_element : 008"  # scripted group (container) (typed FeaturePython)
  n = 1
  ref = Cl_element
FEATURE [App::DocumentObjectGroupPython] G4_POLYTRIFLUOROCHLOROETHYLENE  # scripted group (container) (typed FeaturePython)
  Dunit = g/cm3
  Dvalue = 2.1
  Group = -> [C_element088,F_element015,Cl_element018]
  conduct = 2
  density = 1
  expand = 3
  formula = G4_POLYTRIFLUOROCHLOROETHYLENE
  name = G4_POLYTRIFLUOROCHLOROETHYLENE
  specific = 4
FEATURE [App::DocumentObjectGroupPython] C_element089  label="C_element : 047"  # scripted group (container) (typed FeaturePython)
  n = 4
  ref = C_element
FEATURE [App::DocumentObjectGroupPython] H_element081  label="H_element : 043"  # scripted group (container) (typed FeaturePython)
  n = 6
  ref = H_element
FEATURE [App::DocumentObjectGroupPython] O_element081  label="O_element : 042"  # scripted group (container) (typed FeaturePython)
  n = 2
  ref = O_element
FEATURE [App::DocumentObjectGroupPython] G4_POLYVINYL_ACETATE  # scripted group (container) (typed FeaturePython)
  Dunit = g/cm3
  Dvalue = 1.19
  Group = -> [C_element089,H_element081,O_element081]
  conduct = 2
  density = 1
  expand = 3
  formula = G4_POLYVINYL_ACETATE
  name = G4_POLYVINYL_ACETATE
  specific = 4
FEATURE [App::DocumentObjectGroupPython] C_element090  label="C_element : 048"  # scripted group (container) (typed FeaturePython)
  n = 2
  ref = C_element
FEATURE [App::DocumentObjectGroupPython] H_element082  label="H_element : 044"  # scripted group (container) (typed FeaturePython)
  n = 4
  ref = H_element
FEATURE [App::DocumentObjectGroupPython] O_element082  label="O_element : 043"  # scripted group (container) (typed FeaturePython)
  n = 1
  ref = O_element
FEATURE [App::DocumentObjectGroupPython] G4_POLYVINYL_ALCOHOL  # scripted group (container) (typed FeaturePython)
  Dunit = g/cm3
  Dvalue = 1.3
  Group = -> [C_element090,H_element082,O_element082]
  conduct = 2
  density = 1
  expand = 3
  formula = G4_POLYVINYL_ALCOHOL
  name = G4_POLYVINYL_ALCOHOL
  specific = 4
FEATURE [App::DocumentObjectGroupPython] C_element091  label="C_element : 049"  # scripted group (container) (typed FeaturePython)
  n = 8
  ref = C_element
FEATURE [App::DocumentObjectGroupPython] H_element083  label="H_element : 045"  # scripted group (container) (typed FeaturePython)
  n = 14
  ref = H_element
FEATURE [App::DocumentObjectGroupPython] O_element083  label="O_element : 044"  # scripted group (container) (typed FeaturePython)
  n = 2
  ref = O_element
FEATURE [App::DocumentObjectGroupPython] G4_POLYVINYL_BUTYRAL  # scripted group (container) (typed FeaturePython)
  Dunit = g/cm3
  Dvalue = 1.12
  Group = -> [C_element091,H_element083,O_element083]
  conduct = 2
  density = 1
  expand = 3
  formula = G4_POLYVINYL_BUTYRAL
  name = G4_POLYVINYL_BUTYRAL
  specific = 4
FEATURE [App::DocumentObjectGroupPython] C_element092  label="C_element : 050"  # scripted group (container) (typed FeaturePython)
  n = 2
  ref = C_element
FEATURE [App::DocumentObjectGroupPython] H_element084  label="H_element : 046"  # scripted group (container) (typed FeaturePython)
  n = 3
  ref = H_element
FEATURE [App::DocumentObjectGroupPython] Cl_element019  label="Cl_element : 009"  # scripted group (container) (typed FeaturePython)
  n = 1
  ref = Cl_element
FEATURE [App::DocumentObjectGroupPython] G4_POLYVINYL_CHLORIDE  # scripted group (container) (typed FeaturePython)
  Dunit = g/cm3
  Dvalue = 1.3
  Group = -> [C_element092,H_element084,Cl_element019]
  conduct = 2
  density = 1
  expand = 3
  formula = G4_POLYVINYL_CHLORIDE
  name = G4_POLYVINYL_CHLORIDE
  specific = 4
FEATURE [App::DocumentObjectGroupPython] C_element093  label="C_element : 051"  # scripted group (container) (typed FeaturePython)
  n = 2
  ref = C_element
FEATURE [App::DocumentObjectGroupPython] H_element085  label="H_element : 047"  # scripted group (container) (typed FeaturePython)
  n = 2
  ref = H_element
FEATURE [App::DocumentObjectGroupPython] Cl_element020  label="Cl_element : 010"  # scripted group (container) (typed FeaturePython)
  n = 2
  ref = Cl_element
FEATURE [App::DocumentObjectGroupPython] G4_POLYVINYLIDENE_CHLORIDE  # scripted group (container) (typed FeaturePython)
  Dunit = g/cm3
  Dvalue = 1.7
  Group = -> [C_element093,H_element085,Cl_element020]
  conduct = 2
  density = 1
  expand = 3
  formula = G4_POLYVINYLIDENE_CHLORIDE
  name = G4_POLYVINYLIDENE_CHLORIDE
  specific = 4
FEATURE [App::DocumentObjectGroupPython] C_element094  label="C_element : 052"  # scripted group (container) (typed FeaturePython)
  n = 2
  ref = C_element
FEATURE [App::DocumentObjectGroupPython] H_element086  label="H_element : 048"  # scripted group (container) (typed FeaturePython)
  n = 2
  ref = H_element
FEATURE [App::DocumentObjectGroupPython] F_element016  label="F_element : 007"  # scripted group (container) (typed FeaturePython)
  n = 2
  ref = F_element
FEATURE [App::DocumentObjectGroupPython] G4_POLYVINYLIDENE_FLUORIDE  # scripted group (container) (typed FeaturePython)
  Dunit = g/cm3
  Dvalue = 1.76
  Group = -> [C_element094,H_element086,F_element016]
  conduct = 2
  density = 1
  expand = 3
  formula = G4_POLYVINYLIDENE_FLUORIDE
  name = G4_POLYVINYLIDENE_FLUORIDE
  specific = 4
FEATURE [App::DocumentObjectGroupPython] C_element095  label="C_element : 053"  # scripted group (container) (typed FeaturePython)
  n = 6
  ref = C_element
FEATURE [App::DocumentObjectGroupPython] H_element087  label="H_element : 9"  # scripted group (container) (typed FeaturePython)
  n = 9
  ref = H_element
FEATURE [App::DocumentObjectGroupPython] N_element037  label="N_element : 016"  # scripted group (container) (typed FeaturePython)
  n = 1
  ref = N_element
FEATURE [App::DocumentObjectGroupPython] O_element084  label="O_element : 045"  # scripted group (container) (typed FeaturePython)
  n = 1
  ref = O_element
FEATURE [App::DocumentObjectGroupPython] G4_POLYVINYL_PYRROLIDONE  # scripted group (container) (typed FeaturePython)
  Dunit = g/cm3
  Dvalue = 1.25
  Group = -> [C_element095,H_element087,N_element037,O_element084]
  conduct = 2
  density = 1
  expand = 3
  formula = G4_POLYVINYL_PYRROLIDONE
  name = G4_POLYVINYL_PYRROLIDONE
  specific = 4
FEATURE [App::DocumentObjectGroupPython] K_element008  label="K_element : 1"  # scripted group (container) (typed FeaturePython)
  n = 1
  ref = K_element
FEATURE [App::DocumentObjectGroupPython] I_element006  label="I_element : 003"  # scripted group (container) (typed FeaturePython)
  n = 1
  ref = I_element
FEATURE [App::DocumentObjectGroupPython] G4_POTASSIUM_IODIDE  # scripted group (container) (typed FeaturePython)
  Dunit = g/cm3
  Dvalue = 3.13
  Group = -> [K_element008,I_element006]
  conduct = 2
  density = 1
  expand = 3
  formula = G4_POTASSIUM_IODIDE
  name = G4_POTASSIUM_IODIDE
  specific = 4
FEATURE [App::DocumentObjectGroupPython] K_element009  label="K_element : 2"  # scripted group (container) (typed FeaturePython)
  n = 2
  ref = K_element
FEATURE [App::DocumentObjectGroupPython] O_element085  label="O_element : 046"  # scripted group (container) (typed FeaturePython)
  n = 1
  ref = O_element
FEATURE [App::DocumentObjectGroupPython] G4_POTASSIUM_OXIDE  # scripted group (container) (typed FeaturePython)
  Dunit = g/cm3
  Dvalue = 2.32
  Group = -> [K_element009,O_element085]
  conduct = 2
  density = 1
  expand = 3
  formula = G4_POTASSIUM_OXIDE
  name = G4_POTASSIUM_OXIDE
  specific = 4
FEATURE [App::DocumentObjectGroupPython] C_element096  label="C_element : 054"  # scripted group (container) (typed FeaturePython)
  n = 3
  ref = C_element
FEATURE [App::DocumentObjectGroupPython] H_element088  label="H_element : 049"  # scripted group (container) (typed FeaturePython)
  n = 8
  ref = H_element
FEATURE [App::DocumentObjectGroupPython] G4_PROPANE  # scripted group (container) (typed FeaturePython)
  Dunit = g/cm3
  Dvalue = 0.00187939
  Group = -> [C_element096,H_element088]
  conduct = 2
  density = 1
  expand = 3
  formula = G4_PROPANE
  name = G4_PROPANE
  specific = 4
FEATURE [App::DocumentObjectGroupPython] C_element097  label="C_element : 055"  # scripted group (container) (typed FeaturePython)
  n = 3
  ref = C_element
FEATURE [App::DocumentObjectGroupPython] H_element089  label="H_element : 050"  # scripted group (container) (typed FeaturePython)
  n = 8
  ref = H_element
FEATURE [App::DocumentObjectGroupPython] G4_lPROPANE  # scripted group (container) (typed FeaturePython)
  Dunit = g/cm3
  Dvalue = 0.43
  Group = -> [C_element097,H_element089]
  conduct = 2
  density = 1
  expand = 3
  formula = G4_lPROPANE
  name = G4_lPROPANE
  specific = 4
FEATURE [App::DocumentObjectGroupPython] C_element098  label="C_element : 056"  # scripted group (container) (typed FeaturePython)
  n = 3
  ref = C_element
FEATURE [App::DocumentObjectGroupPython] H_element090  label="H_element : 051"  # scripted group (container) (typed FeaturePython)
  n = 8
  ref = H_element
FEATURE [App::DocumentObjectGroupPython] O_element086  label="O_element : 047"  # scripted group (container) (typed FeaturePython)
  n = 1
  ref = O_element
FEATURE [App::DocumentObjectGroupPython] G4_N_PROPYL_ALCOHOL  label="G4_N-PROPYL_ALCOHOL"  # scripted group (container) (typed FeaturePython)
  Dunit = g/cm3
  Dvalue = 0.8035
  Group = -> [C_element098,H_element090,O_element086]
  conduct = 2
  density = 1
  expand = 3
  formula = G4_N-PROPYL_ALCOHOL
  name = G4_N-PROPYL_ALCOHOL
  specific = 4
FEATURE [App::DocumentObjectGroupPython] C_element099  label="C_element : 057"  # scripted group (container) (typed FeaturePython)
  n = 5
  ref = C_element
FEATURE [App::DocumentObjectGroupPython] H_element091  label="H_element : 052"  # scripted group (container) (typed FeaturePython)
  n = 5
  ref = H_element
FEATURE [App::DocumentObjectGroupPython] N_element038  label="N_element : 017"  # scripted group (container) (typed FeaturePython)
  n = 1
  ref = N_element
FEATURE [App::DocumentObjectGroupPython] G4_PYRIDINE  # scripted group (container) (typed FeaturePython)
  Dunit = g/cm3
  Dvalue = 0.9819
  Group = -> [C_element099,H_element091,N_element038]
  conduct = 2
  density = 1
  expand = 3
  formula = G4_PYRIDINE
  name = G4_PYRIDINE
  specific = 4
FEATURE [App::DocumentObjectGroupPython] H_element092  label="H_element : 0.144"  # scripted group (container) (typed FeaturePython)
  n = 0.143711
FEATURE [App::DocumentObjectGroupPython] C_element100  label="C_element : 0.856"  # scripted group (container) (typed FeaturePython)
  n = 0.856289
FEATURE [App::DocumentObjectGroupPython] G4_RUBBER_BUTYL  # scripted group (container) (typed FeaturePython)
  Dunit = g/cm3
  Dvalue = 0.92
  Group = -> [H_element092,C_element100]
  conduct = 2
  density = 1
  expand = 3
  formula = G4_RUBBER_BUTYL
  name = G4_RUBBER_BUTYL
  specific = 4
FEATURE [App::DocumentObjectGroupPython] H_element093  label="H_element : 0.118"  # scripted group (container) (typed FeaturePython)
  n = 0.118371
FEATURE [App::DocumentObjectGroupPython] C_element101  label="C_element : 0.882"  # scripted group (container) (typed FeaturePython)
  n = 0.881629
FEATURE [App::DocumentObjectGroupPython] G4_RUBBER_NATURAL  # scripted group (container) (typed FeaturePython)
  Dunit = g/cm3
  Dvalue = 0.92
  Group = -> [H_element093,C_element101]
  conduct = 2
  density = 1
  expand = 3
  formula = G4_RUBBER_NATURAL
  name = G4_RUBBER_NATURAL
  specific = 4
FEATURE [App::DocumentObjectGroupPython] H_element094  label="H_element : 0.145"  # scripted group (container) (typed FeaturePython)
  n = 0.05692
FEATURE [App::DocumentObjectGroupPython] C_element102  label="C_element : 0.543"  # scripted group (container) (typed FeaturePython)
  n = 0.542646
FEATURE [App::DocumentObjectGroupPython] Cl_element021  label="Cl_element : 0.400"  # scripted group (container) (typed FeaturePython)
  n = 0.400434
FEATURE [App::DocumentObjectGroupPython] G4_RUBBER_NEOPRENE  # scripted group (container) (typed FeaturePython)
  Dunit = g/cm3
  Dvalue = 1.23
  Group = -> [H_element094,C_element102,Cl_element021]
  conduct = 2
  density = 1
  expand = 3
  formula = G4_RUBBER_NEOPRENE
  name = G4_RUBBER_NEOPRENE
  specific = 4
FEATURE [App::DocumentObjectGroupPython] Si_element006  label="Si_element : 1"  # scripted group (container) (typed FeaturePython)
  n = 1
  ref = Si_element
FEATURE [App::DocumentObjectGroupPython] O_element087  label="O_element : 048"  # scripted group (container) (typed FeaturePython)
  n = 2
  ref = O_element
FEATURE [App::DocumentObjectGroupPython] G4_SILICON_DIOXIDE  # scripted group (container) (typed FeaturePython)
  Dunit = g/cm3
  Dvalue = 2.32
  Group = -> [Si_element006,O_element087]
  conduct = 2
  density = 1
  expand = 3
  formula = G4_SILICON_DIOXIDE
  name = G4_SILICON_DIOXIDE
  specific = 4
FEATURE [App::DocumentObjectGroupPython] Ag_element002  label="Ag_element : 1"  # scripted group (container) (typed FeaturePython)
  n = 1
  ref = Ag_element
FEATURE [App::DocumentObjectGroupPython] Br_element005  label="Br_element : 003"  # scripted group (container) (typed FeaturePython)
  n = 1
  ref = Br_element
FEATURE [App::DocumentObjectGroupPython] G4_SILVER_BROMIDE  # scripted group (container) (typed FeaturePython)
  Dunit = g/cm3
  Dvalue = 6.473
  Group = -> [Ag_element002,Br_element005]
  conduct = 2
  density = 1
  expand = 3
  formula = G4_SILVER_BROMIDE
  name = G4_SILVER_BROMIDE
  specific = 4
FEATURE [App::DocumentObjectGroupPython] Ag_element003  label="Ag_element : 002"  # scripted group (container) (typed FeaturePython)
  n = 1
  ref = Ag_element
FEATURE [App::DocumentObjectGroupPython] Cl_element022  label="Cl_element : 011"  # scripted group (container) (typed FeaturePython)
  n = 1
  ref = Cl_element
FEATURE [App::DocumentObjectGroupPython] G4_SILVER_CHLORIDE  # scripted group (container) (typed FeaturePython)
  Dunit = g/cm3
  Dvalue = 5.56
  Group = -> [Ag_element003,Cl_element022]
  conduct = 2
  density = 1
  expand = 3
  formula = G4_SILVER_CHLORIDE
  name = G4_SILVER_CHLORIDE
  specific = 4
FEATURE [App::DocumentObjectGroupPython] Br_element006  label="Br_element : 0.423"  # scripted group (container) (typed FeaturePython)
  n = 0.422895
FEATURE [App::DocumentObjectGroupPython] Ag_element004  label="Ag_element : 0.574"  # scripted group (container) (typed FeaturePython)
  n = 0.573748
FEATURE [App::DocumentObjectGroupPython] I_element007  label="I_element : 0.649"  # scripted group (container) (typed FeaturePython)
  n = 0.003357
FEATURE [App::DocumentObjectGroupPython] G4_SILVER_HALIDES  # scripted group (container) (typed FeaturePython)
  Dunit = g/cm3
  Dvalue = 6.47
  Group = -> [Br_element006,Ag_element004,I_element007]
  conduct = 2
  density = 1
  expand = 3
  formula = G4_SILVER_HALIDES
  name = G4_SILVER_HALIDES
  specific = 4
FEATURE [App::DocumentObjectGroupPython] Ag_element005  label="Ag_element : 003"  # scripted group (container) (typed FeaturePython)
  n = 1
  ref = Ag_element
FEATURE [App::DocumentObjectGroupPython] I_element008  label="I_element : 004"  # scripted group (container) (typed FeaturePython)
  n = 1
  ref = I_element
FEATURE [App::DocumentObjectGroupPython] G4_SILVER_IODIDE  # scripted group (container) (typed FeaturePython)
  Dunit = g/cm3
  Dvalue = 6.01
  Group = -> [Ag_element005,I_element008]
  conduct = 2
  density = 1
  expand = 3
  formula = G4_SILVER_IODIDE
  name = G4_SILVER_IODIDE
  specific = 4
FEATURE [App::DocumentObjectGroupPython] H_element095  label="H_element : 0.100"  # scripted group (container) (typed FeaturePython)
  n = 0.1
FEATURE [App::DocumentObjectGroupPython] C_element103  label="C_element : 0.204"  # scripted group (container) (typed FeaturePython)
  n = 0.204
FEATURE [App::DocumentObjectGroupPython] N_element039  label="N_element : 0.759"  # scripted group (container) (typed FeaturePython)
  n = 0.042
FEATURE [App::DocumentObjectGroupPython] O_element088  label="O_element : 0.645"  # scripted group (container) (typed FeaturePython)
  n = 0.645
FEATURE [App::DocumentObjectGroupPython] Na_element013  label="Na_element : 0.100"  # scripted group (container) (typed FeaturePython)
  n = 0.002
FEATURE [App::DocumentObjectGroupPython] P_element009  label="P_element : 0.107"  # scripted group (container) (typed FeaturePython)
  n = 0.001
FEATURE [App::DocumentObjectGroupPython] S_element020  label="S_element : 0.021"  # scripted group (container) (typed FeaturePython)
  n = 0.002
FEATURE [App::DocumentObjectGroupPython] Cl_element023  label="Cl_element : 0.590"  # scripted group (container) (typed FeaturePython)
  n = 0.003
FEATURE [App::DocumentObjectGroupPython] K_element010  label="K_element : 0.001"  # scripted group (container) (typed FeaturePython)
  n = 0.001
FEATURE [App::DocumentObjectGroupPython] G4_SKIN_ICRP  # scripted group (container) (typed FeaturePython)
  Dunit = g/cm3
  Dvalue = 1.09
  Group = -> [H_element095,C_element103,N_element039,O_element088,Na_element013,P_element009,S_element020,Cl_element023,K_element010]
  conduct = 2
  density = 1
  expand = 3
  formula = G4_SKIN_ICRP
  name = G4_SKIN_ICRP
  specific = 4
FEATURE [App::DocumentObjectGroupPython] Na_element014  label="Na_element : 2"  # scripted group (container) (typed FeaturePython)
  n = 2
  ref = Na_element
FEATURE [App::DocumentObjectGroupPython] C_element104  label="C_element : 058"  # scripted group (container) (typed FeaturePython)
  n = 1
  ref = C_element
FEATURE [App::DocumentObjectGroupPython] O_element089  label="O_element : 049"  # scripted group (container) (typed FeaturePython)
  n = 3
  ref = O_element
FEATURE [App::DocumentObjectGroupPython] G4_SODIUM_CARBONATE  # scripted group (container) (typed FeaturePython)
  Dunit = g/cm3
  Dvalue = 2.532
  Group = -> [Na_element014,C_element104,O_element089]
  conduct = 2
  density = 1
  expand = 3
  formula = G4_SODIUM_CARBONATE
  name = G4_SODIUM_CARBONATE
  specific = 4
FEATURE [App::DocumentObjectGroupPython] Na_element015  label="Na_element : 1"  # scripted group (container) (typed FeaturePython)
  n = 1
  ref = Na_element
FEATURE [App::DocumentObjectGroupPython] I_element009  label="I_element : 005"  # scripted group (container) (typed FeaturePython)
  n = 1
  ref = I_element
FEATURE [App::DocumentObjectGroupPython] G4_SODIUM_IODIDE  # scripted group (container) (typed FeaturePython)
  Dunit = g/cm3
  Dvalue = 3.667
  Group = -> [Na_element015,I_element009]
  conduct = 2
  density = 1
  expand = 3
  formula = G4_SODIUM_IODIDE
  name = G4_SODIUM_IODIDE
  specific = 4
FEATURE [App::DocumentObjectGroupPython] Na_element016  label="Na_element : 003"  # scripted group (container) (typed FeaturePython)
  n = 2
  ref = Na_element
FEATURE [App::DocumentObjectGroupPython] O_element090  label="O_element : 050"  # scripted group (container) (typed FeaturePython)
  n = 1
  ref = O_element
FEATURE [App::DocumentObjectGroupPython] G4_SODIUM_MONOXIDE  # scripted group (container) (typed FeaturePython)
  Dunit = g/cm3
  Dvalue = 2.27
  Group = -> [Na_element016,O_element090]
  conduct = 2
  density = 1
  expand = 3
  formula = G4_SODIUM_MONOXIDE
  name = G4_SODIUM_MONOXIDE
  specific = 4
FEATURE [App::DocumentObjectGroupPython] Na_element017  label="Na_element : 004"  # scripted group (container) (typed FeaturePython)
  n = 1
  ref = Na_element
FEATURE [App::DocumentObjectGroupPython] N_element040  label="N_element : 018"  # scripted group (container) (typed FeaturePython)
  n = 1
  ref = N_element
FEATURE [App::DocumentObjectGroupPython] O_element091  label="O_element : 051"  # scripted group (container) (typed FeaturePython)
  n = 3
  ref = O_element
FEATURE [App::DocumentObjectGroupPython] G4_SODIUM_NITRATE  # scripted group (container) (typed FeaturePython)
  Dunit = g/cm3
  Dvalue = 2.261
  Group = -> [Na_element017,N_element040,O_element091]
  conduct = 2
  density = 1
  expand = 3
  formula = G4_SODIUM_NITRATE
  name = G4_SODIUM_NITRATE
  specific = 4
FEATURE [App::DocumentObjectGroupPython] C_element105  label="C_element : 059"  # scripted group (container) (typed FeaturePython)
  n = 14
  ref = C_element
FEATURE [App::DocumentObjectGroupPython] H_element096  label="H_element : 053"  # scripted group (container) (typed FeaturePython)
  n = 12
  ref = H_element
FEATURE [App::DocumentObjectGroupPython] G4_STILBENE  # scripted group (container) (typed FeaturePython)
  Dunit = g/cm3
  Dvalue = 0.9707
  Group = -> [C_element105,H_element096]
  conduct = 2
  density = 1
  expand = 3
  formula = G4_STILBENE
  name = G4_STILBENE
  specific = 4
FEATURE [App::DocumentObjectGroupPython] C_element106  label="C_element : 12"  # scripted group (container) (typed FeaturePython)
  n = 12
  ref = C_element
FEATURE [App::DocumentObjectGroupPython] H_element097  label="H_element : 22"  # scripted group (container) (typed FeaturePython)
  n = 22
  ref = H_element
FEATURE [App::DocumentObjectGroupPython] O_element092  label="O_element : 11"  # scripted group (container) (typed FeaturePython)
  n = 11
  ref = O_element
FEATURE [App::DocumentObjectGroupPython] G4_SUCROSE  # scripted group (container) (typed FeaturePython)
  Dunit = g/cm3
  Dvalue = 1.5805
  Group = -> [C_element106,H_element097,O_element092]
  conduct = 2
  density = 1
  expand = 3
  formula = G4_SUCROSE
  name = G4_SUCROSE
  specific = 4
FEATURE [App::DocumentObjectGroupPython] C_element107  label="C_element : 18"  # scripted group (container) (typed FeaturePython)
  n = 18
  ref = C_element
FEATURE [App::DocumentObjectGroupPython] H_element098  label="H_element : 054"  # scripted group (container) (typed FeaturePython)
  n = 14
  ref = H_element
FEATURE [App::DocumentObjectGroupPython] G4_TERPHENYL  # scripted group (container) (typed FeaturePython)
  Dunit = g/cm3
  Dvalue = 1.24
  Group = -> [C_element107,H_element098]
  conduct = 2
  density = 1
  expand = 3
  formula = G4_TERPHENYL
  name = G4_TERPHENYL
  specific = 4
FEATURE [App::DocumentObjectGroupPython] H_element099  label="H_element : 0.146"  # scripted group (container) (typed FeaturePython)
  n = 0.106
FEATURE [App::DocumentObjectGroupPython] C_element108  label="C_element : 0.883"  # scripted group (container) (typed FeaturePython)
  n = 0.099
FEATURE [App::DocumentObjectGroupPython] N_element041  label="N_element : 0.020"  # scripted group (container) (typed FeaturePython)
  n = 0.02
FEATURE [App::DocumentObjectGroupPython] O_element093  label="O_element : 0.766"  # scripted group (container) (typed FeaturePython)
  n = 0.766
FEATURE [App::DocumentObjectGroupPython] Na_element018  label="Na_element : 0.101"  # scripted group (container) (typed FeaturePython)
  n = 0.002
FEATURE [App::DocumentObjectGroupPython] P_element010  label="P_element : 0.108"  # scripted group (container) (typed FeaturePython)
  n = 0.001
FEATURE [App::DocumentObjectGroupPython] S_element021  label="S_element : 0.022"  # scripted group (container) (typed FeaturePython)
  n = 0.002
FEATURE [App::DocumentObjectGroupPython] Cl_element024  label="Cl_element : 0.002"  # scripted group (container) (typed FeaturePython)
  n = 0.002
FEATURE [App::DocumentObjectGroupPython] K_element011  label="K_element : 0.017"  # scripted group (container) (typed FeaturePython)
  n = 0.002
FEATURE [App::DocumentObjectGroupPython] G4_TESTIS_ICRP  # scripted group (container) (typed FeaturePython)
  Dunit = g/cm3
  Dvalue = 1.04
  Group = -> [H_element099,C_element108,N_element041,O_element093,Na_element018,P_element010,S_element021,Cl_element024,K_element011]
  conduct = 2
  density = 1
  expand = 3
  formula = G4_TESTIS_ICRP
  name = G4_TESTIS_ICRP
  specific = 4
FEATURE [App::DocumentObjectGroupPython] C_element109  label="C_element : 060"  # scripted group (container) (typed FeaturePython)
  n = 2
  ref = C_element
FEATURE [App::DocumentObjectGroupPython] Cl_element025  label="Cl_element : 012"  # scripted group (container) (typed FeaturePython)
  n = 4
  ref = Cl_element
FEATURE [App::DocumentObjectGroupPython] G4_TETRACHLOROETHYLENE  # scripted group (container) (typed FeaturePython)
  Dunit = g/cm3
  Dvalue = 1.625
  Group = -> [C_element109,Cl_element025]
  conduct = 2
  density = 1
  expand = 3
  formula = G4_TETRACHLOROETHYLENE
  name = G4_TETRACHLOROETHYLENE
  specific = 4
FEATURE [App::DocumentObjectGroupPython] Tl_element001  label="Tl_element : 1"  # scripted group (container) (typed FeaturePython)
  n = 1
  ref = Tl_element
FEATURE [App::DocumentObjectGroupPython] Cl_element026  label="Cl_element : 013"  # scripted group (container) (typed FeaturePython)
  n = 1
  ref = Cl_element
FEATURE [App::DocumentObjectGroupPython] G4_THALLIUM_CHLORIDE  # scripted group (container) (typed FeaturePython)
  Dunit = g/cm3
  Dvalue = 7.004
  Group = -> [Tl_element001,Cl_element026]
  conduct = 2
  density = 1
  expand = 3
  formula = G4_THALLIUM_CHLORIDE
  name = G4_THALLIUM_CHLORIDE
  specific = 4
FEATURE [App::DocumentObjectGroupPython] H_element100  label="H_element : 0.147"  # scripted group (container) (typed FeaturePython)
  n = 0.105
FEATURE [App::DocumentObjectGroupPython] C_element110  label="C_element : 0.256"  # scripted group (container) (typed FeaturePython)
  n = 0.256
FEATURE [App::DocumentObjectGroupPython] N_element042  label="N_element : 0.760"  # scripted group (container) (typed FeaturePython)
  n = 0.027
FEATURE [App::DocumentObjectGroupPython] O_element094  label="O_element : 0.602"  # scripted group (container) (typed FeaturePython)
  n = 0.602
FEATURE [App::DocumentObjectGroupPython] Na_element019  label="Na_element : 0.102"  # scripted group (container) (typed FeaturePython)
  n = 0.001
FEATURE [App::DocumentObjectGroupPython] P_element011  label="P_element : 0.109"  # scripted group (container) (typed FeaturePython)
  n = 0.002
FEATURE [App::DocumentObjectGroupPython] S_element022  label="S_element : 0.023"  # scripted group (container) (typed FeaturePython)
  n = 0.003
FEATURE [App::DocumentObjectGroupPython] Cl_element027  label="Cl_element : 0.591"  # scripted group (container) (typed FeaturePython)
  n = 0.002
FEATURE [App::DocumentObjectGroupPython] K_element012  label="K_element : 0.018"  # scripted group (container) (typed FeaturePython)
  n = 0.002
FEATURE [App::DocumentObjectGroupPython] G4_TISSUE_SOFT_ICRP  # scripted group (container) (typed FeaturePython)
  Dunit = g/cm3
  Dvalue = 1.03
  Group = -> [H_element100,C_element110,N_element042,O_element094,Na_element019,P_element011,S_element022,Cl_element027,K_element012]
  conduct = 2
  density = 1
  expand = 3
  formula = G4_TISSUE_SOFT_ICRP
  name = G4_TISSUE_SOFT_ICRP
  specific = 4
FEATURE [App::DocumentObjectGroupPython] H_element101  label="H_element : 0.148"  # scripted group (container) (typed FeaturePython)
  n = 0.101
FEATURE [App::DocumentObjectGroupPython] C_element111  label="C_element : 0.111"  # scripted group (container) (typed FeaturePython)
  n = 0.111
FEATURE [App::DocumentObjectGroupPython] N_element043  label="N_element : 0.026"  # scripted group (container) (typed FeaturePython)
  n = 0.026
FEATURE [App::DocumentObjectGroupPython] O_element095  label="O_element : 0.762"  # scripted group (container) (typed FeaturePython)
  n = 0.762
FEATURE [App::DocumentObjectGroupPython] G4_TISSUE_SOFT_ICRU_4  label="G4_TISSUE_SOFT_ICRU-4"  # scripted group (container) (typed FeaturePython)
  Dunit = g/cm3
  Dvalue = 1
  Group = -> [H_element101,C_element111,N_element043,O_element095]
  conduct = 2
  density = 1
  expand = 3
  formula = G4_TISSUE_SOFT_ICRU-4
  name = G4_TISSUE_SOFT_ICRU-4
  specific = 4
FEATURE [App::DocumentObjectGroupPython] H_element102  label="H_element : 0.149"  # scripted group (container) (typed FeaturePython)
  n = 0.101869
FEATURE [App::DocumentObjectGroupPython] C_element112  label="C_element : 0.456"  # scripted group (container) (typed FeaturePython)
  n = 0.456179
FEATURE [App::DocumentObjectGroupPython] N_element044  label="N_element : 0.761"  # scripted group (container) (typed FeaturePython)
  n = 0.035172
FEATURE [App::DocumentObjectGroupPython] O_element096  label="O_element : 0.407"  # scripted group (container) (typed FeaturePython)
  n = 0.40678
FEATURE [App::DocumentObjectGroupPython] G4_TISSUE_METHANE  label="G4_TISSUE-METHANE"  # scripted group (container) (typed FeaturePython)
  Dunit = g/cm3
  Dvalue = 0.00106409
  Group = -> [H_element102,C_element112,N_element044,O_element096]
  conduct = 2
  density = 1
  expand = 3
  formula = G4_TISSUE-METHANE
  name = G4_TISSUE-METHANE
  specific = 4
FEATURE [App::DocumentObjectGroupPython] H_element103  label="H_element : 0.103"  # scripted group (container) (typed FeaturePython)
  n = 0.102672
FEATURE [App::DocumentObjectGroupPython] C_element113  label="C_element : 0.569"  # scripted group (container) (typed FeaturePython)
  n = 0.56894
FEATURE [App::DocumentObjectGroupPython] N_element045  label="N_element : 0.762"  # scripted group (container) (typed FeaturePython)
  n = 0.035022
FEATURE [App::DocumentObjectGroupPython] O_element097  label="O_element : 0.293"  # scripted group (container) (typed FeaturePython)
  n = 0.293366
FEATURE [App::DocumentObjectGroupPython] G4_TISSUE_PROPANE  label="G4_TISSUE-PROPANE"  # scripted group (container) (typed FeaturePython)
  Dunit = g/cm3
  Dvalue = 0.00182628
  Group = -> [H_element103,C_element113,N_element045,O_element097]
  conduct = 2
  density = 1
  expand = 3
  formula = G4_TISSUE-PROPANE
  name = G4_TISSUE-PROPANE
  specific = 4
FEATURE [App::DocumentObjectGroupPython] Ti_element003  label="Ti_element : 1"  # scripted group (container) (typed FeaturePython)
  n = 1
  ref = Ti_element
FEATURE [App::DocumentObjectGroupPython] O_element098  label="O_element : 052"  # scripted group (container) (typed FeaturePython)
  n = 2
  ref = O_element
FEATURE [App::DocumentObjectGroupPython] G4_TITANIUM_DIOXIDE  # scripted group (container) (typed FeaturePython)
  Dunit = g/cm3
  Dvalue = 4.26
  Group = -> [Ti_element003,O_element098]
  conduct = 2
  density = 1
  expand = 3
  formula = G4_TITANIUM_DIOXIDE
  name = G4_TITANIUM_DIOXIDE
  specific = 4
FEATURE [App::DocumentObjectGroupPython] C_element114  label="C_element : 061"  # scripted group (container) (typed FeaturePython)
  n = 7
  ref = C_element
FEATURE [App::DocumentObjectGroupPython] H_element104  label="H_element : 055"  # scripted group (container) (typed FeaturePython)
  n = 8
  ref = H_element
FEATURE [App::DocumentObjectGroupPython] G4_TOLUENE  # scripted group (container) (typed FeaturePython)
  Dunit = g/cm3
  Dvalue = 0.8669
  Group = -> [C_element114,H_element104]
  conduct = 2
  density = 1
  expand = 3
  formula = G4_TOLUENE
  name = G4_TOLUENE
  specific = 4
FEATURE [App::DocumentObjectGroupPython] C_element115  label="C_element : 062"  # scripted group (container) (typed FeaturePython)
  n = 2
  ref = C_element
FEATURE [App::DocumentObjectGroupPython] H_element105  label="H_element : 056"  # scripted group (container) (typed FeaturePython)
  n = 1
  ref = H_element
FEATURE [App::DocumentObjectGroupPython] Cl_element028  label="Cl_element : 014"  # scripted group (container) (typed FeaturePython)
  n = 3
  ref = Cl_element
FEATURE [App::DocumentObjectGroupPython] G4_TRICHLOROETHYLENE  # scripted group (container) (typed FeaturePython)
  Dunit = g/cm3
  Dvalue = 1.46
  Group = -> [C_element115,H_element105,Cl_element028]
  conduct = 2
  density = 1
  expand = 3
  formula = G4_TRICHLOROETHYLENE
  name = G4_TRICHLOROETHYLENE
  specific = 4
FEATURE [App::DocumentObjectGroupPython] C_element116  label="C_element : 063"  # scripted group (container) (typed FeaturePython)
  n = 6
  ref = C_element
FEATURE [App::DocumentObjectGroupPython] H_element106  label="H_element : 15"  # scripted group (container) (typed FeaturePython)
  n = 15
  ref = H_element
FEATURE [App::DocumentObjectGroupPython] O_element099  label="O_element : 053"  # scripted group (container) (typed FeaturePython)
  n = 4
  ref = O_element
FEATURE [App::DocumentObjectGroupPython] P_element012  label="P_element : 1"  # scripted group (container) (typed FeaturePython)
  n = 1
  ref = P_element
FEATURE [App::DocumentObjectGroupPython] G4_TRIETHYL_PHOSPHATE  # scripted group (container) (typed FeaturePython)
  Dunit = g/cm3
  Dvalue = 1.07
  Group = -> [C_element116,H_element106,O_element099,P_element012]
  conduct = 2
  density = 1
  expand = 3
  formula = G4_TRIETHYL_PHOSPHATE
  name = G4_TRIETHYL_PHOSPHATE
  specific = 4
FEATURE [App::DocumentObjectGroupPython] W_element003  label="W_element : 003"  # scripted group (container) (typed FeaturePython)
  n = 1
  ref = W_element
FEATURE [App::DocumentObjectGroupPython] F_element017  label="F_element : 6"  # scripted group (container) (typed FeaturePython)
  n = 6
  ref = F_element
FEATURE [App::DocumentObjectGroupPython] G4_TUNGSTEN_HEXAFLUORIDE  # scripted group (container) (typed FeaturePython)
  Dunit = g/cm3
  Dvalue = 2.4
  Group = -> [W_element003,F_element017]
  conduct = 2
  density = 1
  expand = 3
  formula = G4_TUNGSTEN_HEXAFLUORIDE
  name = G4_TUNGSTEN_HEXAFLUORIDE
  specific = 4
FEATURE [App::DocumentObjectGroupPython] U_element001  label="U_element : 1"  # scripted group (container) (typed FeaturePython)
  n = 1
  ref = U_element
FEATURE [App::DocumentObjectGroupPython] C_element117  label="C_element : 064"  # scripted group (container) (typed FeaturePython)
  n = 2
  ref = C_element
FEATURE [App::DocumentObjectGroupPython] G4_URANIUM_DICARBIDE  # scripted group (container) (typed FeaturePython)
  Dunit = g/cm3
  Dvalue = 11.28
  Group = -> [U_element001,C_element117]
  conduct = 2
  density = 1
  expand = 3
  formula = G4_URANIUM_DICARBIDE
  name = G4_URANIUM_DICARBIDE
  specific = 4
FEATURE [App::DocumentObjectGroupPython] U_element002  label="U_element : 002"  # scripted group (container) (typed FeaturePython)
  n = 1
  ref = U_element
FEATURE [App::DocumentObjectGroupPython] C_element118  label="C_element : 065"  # scripted group (container) (typed FeaturePython)
  n = 1
  ref = C_element
FEATURE [App::DocumentObjectGroupPython] G4_URANIUM_MONOCARBIDE  # scripted group (container) (typed FeaturePython)
  Dunit = g/cm3
  Dvalue = 13.63
  Group = -> [U_element002,C_element118]
  conduct = 2
  density = 1
  expand = 3
  formula = G4_URANIUM_MONOCARBIDE
  name = G4_URANIUM_MONOCARBIDE
  specific = 4
FEATURE [App::DocumentObjectGroupPython] U_element003  label="U_element : 003"  # scripted group (container) (typed FeaturePython)
  n = 1
  ref = U_element
FEATURE [App::DocumentObjectGroupPython] O_element100  label="O_element : 054"  # scripted group (container) (typed FeaturePython)
  n = 2
  ref = O_element
FEATURE [App::DocumentObjectGroupPython] G4_URANIUM_OXIDE  # scripted group (container) (typed FeaturePython)
  Dunit = g/cm3
  Dvalue = 10.96
  Group = -> [U_element003,O_element100]
  conduct = 2
  density = 1
  expand = 3
  formula = G4_URANIUM_OXIDE
  name = G4_URANIUM_OXIDE
  specific = 4
FEATURE [App::DocumentObjectGroupPython] C_element119  label="C_element : 066"  # scripted group (container) (typed FeaturePython)
  n = 1
  ref = C_element
FEATURE [App::DocumentObjectGroupPython] H_element107  label="H_element : 057"  # scripted group (container) (typed FeaturePython)
  n = 4
  ref = H_element
FEATURE [App::DocumentObjectGroupPython] N_element046  label="N_element : 019"  # scripted group (container) (typed FeaturePython)
  n = 2
  ref = N_element
FEATURE [App::DocumentObjectGroupPython] O_element101  label="O_element : 055"  # scripted group (container) (typed FeaturePython)
  n = 1
  ref = O_element
FEATURE [App::DocumentObjectGroupPython] G4_UREA  # scripted group (container) (typed FeaturePython)
  Dunit = g/cm3
  Dvalue = 1.323
  Group = -> [C_element119,H_element107,N_element046,O_element101]
  conduct = 2
  density = 1
  expand = 3
  formula = G4_UREA
  name = G4_UREA
  specific = 4
FEATURE [App::DocumentObjectGroupPython] C_element120  label="C_element : 067"  # scripted group (container) (typed FeaturePython)
  n = 5
  ref = C_element
FEATURE [App::DocumentObjectGroupPython] H_element108  label="H_element : 058"  # scripted group (container) (typed FeaturePython)
  n = 11
  ref = H_element
FEATURE [App::DocumentObjectGroupPython] N_element047  label="N_element : 020"  # scripted group (container) (typed FeaturePython)
  n = 1
  ref = N_element
FEATURE [App::DocumentObjectGroupPython] O_element102  label="O_element : 056"  # scripted group (container) (typed FeaturePython)
  n = 2
  ref = O_element
FEATURE [App::DocumentObjectGroupPython] G4_VALINE  # scripted group (container) (typed FeaturePython)
  Dunit = g/cm3
  Dvalue = 1.23
  Group = -> [C_element120,H_element108,N_element047,O_element102]
  conduct = 2
  density = 1
  expand = 3
  formula = G4_VALINE
  name = G4_VALINE
  specific = 4
FEATURE [App::DocumentObjectGroupPython] H_element109  label="H_element : 0.009"  # scripted group (container) (typed FeaturePython)
  n = 0.009417
FEATURE [App::DocumentObjectGroupPython] C_element121  label="C_element : 0.281"  # scripted group (container) (typed FeaturePython)
  n = 0.280555
FEATURE [App::DocumentObjectGroupPython] F_element018  label="F_element : 0.710"  # scripted group (container) (typed FeaturePython)
  n = 0.710028
FEATURE [App::DocumentObjectGroupPython] G4_VITON  # scripted group (container) (typed FeaturePython)
  Dunit = g/cm3
  Dvalue = 1.8
  Group = -> [H_element109,C_element121,F_element018]
  conduct = 2
  density = 1
  expand = 3
  formula = G4_VITON
  name = G4_VITON
  specific = 4
FEATURE [App::DocumentObjectGroupPython] H_element110  label="H_element : 059"  # scripted group (container) (typed FeaturePython)
  n = 2
  ref = H_element
FEATURE [App::DocumentObjectGroupPython] O_element103  label="O_element : 057"  # scripted group (container) (typed FeaturePython)
  n = 1
  ref = O_element
FEATURE [App::DocumentObjectGroupPython] G4_WATER  # scripted group (container) (typed FeaturePython)
  Dunit = g/cm3
  Dvalue = 1
  Group = -> [H_element110,O_element103]
  conduct = 2
  density = 1
  expand = 3
  formula = G4_WATER
  name = G4_WATER
  specific = 4
FEATURE [App::DocumentObjectGroupPython] H_element111  label="H_element : 060"  # scripted group (container) (typed FeaturePython)
  n = 2
  ref = H_element
FEATURE [App::DocumentObjectGroupPython] O_element104  label="O_element : 058"  # scripted group (container) (typed FeaturePython)
  n = 1
  ref = O_element
FEATURE [App::DocumentObjectGroupPython] G4_WATER_VAPOR  # scripted group (container) (typed FeaturePython)
  Dunit = g/cm3
  Dvalue = 0.000756182
  Group = -> [H_element111,O_element104]
  conduct = 2
  density = 1
  expand = 3
  formula = G4_WATER_VAPOR
  name = G4_WATER_VAPOR
  specific = 4
FEATURE [App::DocumentObjectGroupPython] C_element122  label="C_element : 068"  # scripted group (container) (typed FeaturePython)
  n = 8
  ref = C_element
FEATURE [App::DocumentObjectGroupPython] H_element112  label="H_element : 061"  # scripted group (container) (typed FeaturePython)
  n = 10
  ref = H_element
FEATURE [App::DocumentObjectGroupPython] G4_XYLENE  # scripted group (container) (typed FeaturePython)
  Dunit = g/cm3
  Dvalue = 0.87
  Group = -> [C_element122,H_element112]
  conduct = 2
  density = 1
  expand = 3
  formula = G4_XYLENE
  name = G4_XYLENE
  specific = 4
FEATURE [App::DocumentObjectGroupPython] C_element123  label="C_element : 069"  # scripted group (container) (typed FeaturePython)
  n = 1
  ref = C_element
FEATURE [App::DocumentObjectGroupPython] G4_GRAPHITE  # scripted group (container) (typed FeaturePython)
  Dunit = g/cm3
  Dvalue = 2.21
  Group = -> [C_element123]
  conduct = 2
  density = 1
  expand = 3
  formula = G4_GRAPHITE
  name = G4_GRAPHITE
  specific = 4
FEATURE [App::DocumentObjectGroupPython] NIST  # scripted group (container) (typed FeaturePython)
  Group = -> [G4_A_150_TISSUE,G4_ACETONE,G4_ACETYLENE,G4_ADENINE,G4_ADIPOSE_TISSUE_ICRP,G4_AIR,G4_ALANINE,G4_ALUMINUM_OXIDE,G4_AMBER,G4_AMMONIA,G4_ANILINE,G4_ANTHRACENE,G4_B_100_BONE,G4_BAKELITE,G4_BARIUM_FLUORIDE,G4_BARIUM_SULFATE,G4_BENZENE,G4_BERYLLIUM_OXIDE,G4_BGO,G4_BLOOD_ICRP,G4_BONE_COMPACT_ICRU,G4_BONE_CORTICAL_ICRP,G4_BORON_CARBIDE,G4_BORON_OXIDE,G4_BRAIN_ICRP,G4_BUTANE,G4_N_BUTYL_ALCOHOL,G4_C_552,+152 more]
FEATURE [App::DocumentObjectGroupPython] H_element113  label="H_element : 062"  # scripted group (container) (typed FeaturePython)
  n = 1
  ref = H_element
FEATURE [App::DocumentObjectGroupPython] G4_H  # scripted group (container) (typed FeaturePython)
  Dunit = g/cm3
  Dvalue = 8.3748e-05
  Group = -> [H_element113]
  conduct = 2
  density = 1
  expand = 3
  formula = H
  name = G4_H
  specific = 4
FEATURE [App::DocumentObjectGroupPython] He_element001  label="He_element : 1"  # scripted group (container) (typed FeaturePython)
  n = 1
  ref = He_element
FEATURE [App::DocumentObjectGroupPython] G4_He  # scripted group (container) (typed FeaturePython)
  Dunit = g/cm3
  Dvalue = 0.000166322
  Group = -> [He_element001]
  conduct = 2
  density = 1
  expand = 3
  formula = He
  name = G4_He
  specific = 4
FEATURE [App::DocumentObjectGroupPython] Li_element008  label="Li_element : 008"  # scripted group (container) (typed FeaturePython)
  n = 1
  ref = Li_element
FEATURE [App::DocumentObjectGroupPython] G4_Li  # scripted group (container) (typed FeaturePython)
  Dunit = g/cm3
  Dvalue = 0.534
  Group = -> [Li_element008]
  conduct = 2
  density = 1
  expand = 3
  formula = Li
  name = G4_Li
  specific = 4
FEATURE [App::DocumentObjectGroupPython] Be_element002  label="Be_element : 002"  # scripted group (container) (typed FeaturePython)
  n = 1
  ref = Be_element
FEATURE [App::DocumentObjectGroupPython] G4_Be  # scripted group (container) (typed FeaturePython)
  Dunit = g/cm3
  Dvalue = 1.848
  Group = -> [Be_element002]
  conduct = 2
  density = 1
  expand = 3
  formula = Be
  name = G4_Be
  specific = 4
FEATURE [App::DocumentObjectGroupPython] B_element007  label="B_element : 007"  # scripted group (container) (typed FeaturePython)
  n = 1
  ref = B_element
FEATURE [App::DocumentObjectGroupPython] G4_B  # scripted group (container) (typed FeaturePython)
  Dunit = g/cm3
  Dvalue = 2.37
  Group = -> [B_element007]
  conduct = 2
  density = 1
  expand = 3
  formula = B
  name = G4_B
  specific = 4
FEATURE [App::DocumentObjectGroupPython] C_element124  label="C_element : 070"  # scripted group (container) (typed FeaturePython)
  n = 1
  ref = C_element
FEATURE [App::DocumentObjectGroupPython] G4_C  # scripted group (container) (typed FeaturePython)
  Dunit = g/cm3
  Dvalue = 2
  Group = -> [C_element124]
  conduct = 2
  density = 1
  expand = 3
  formula = C
  name = G4_C
  specific = 4
FEATURE [App::DocumentObjectGroupPython] N_element048  label="N_element : 021"  # scripted group (container) (typed FeaturePython)
  n = 1
  ref = N_element
FEATURE [App::DocumentObjectGroupPython] G4_N  # scripted group (container) (typed FeaturePython)
  Dunit = g/cm3
  Dvalue = 0.0011652
  Group = -> [N_element048]
  conduct = 2
  density = 1
  expand = 3
  formula = N
  name = G4_N
  specific = 4
FEATURE [App::DocumentObjectGroupPython] O_element105  label="O_element : 059"  # scripted group (container) (typed FeaturePython)
  n = 1
  ref = O_element
FEATURE [App::DocumentObjectGroupPython] G4_O  # scripted group (container) (typed FeaturePython)
  Dunit = g/cm3
  Dvalue = 0.00133151
  Group = -> [O_element105]
  conduct = 2
  density = 1
  expand = 3
  formula = O
  name = G4_O
  specific = 4
FEATURE [App::DocumentObjectGroupPython] F_element019  label="F_element : 008"  # scripted group (container) (typed FeaturePython)
  n = 1
  ref = F_element
FEATURE [App::DocumentObjectGroupPython] G4_F  # scripted group (container) (typed FeaturePython)
  Dunit = g/cm3
  Dvalue = 0.00158029
  Group = -> [F_element019]
  conduct = 2
  density = 1
  expand = 3
  formula = F
  name = G4_F
  specific = 4
FEATURE [App::DocumentObjectGroupPython] Ne_element001  label="Ne_element : 1"  # scripted group (container) (typed FeaturePython)
  n = 1
  ref = Ne_element
FEATURE [App::DocumentObjectGroupPython] G4_Ne  # scripted group (container) (typed FeaturePython)
  Dunit = g/cm3
  Dvalue = 0.000838505
  Group = -> [Ne_element001]
  conduct = 2
  density = 1
  expand = 3
  formula = Ne
  name = G4_Ne
  specific = 4
FEATURE [App::DocumentObjectGroupPython] Na_element020  label="Na_element : 005"  # scripted group (container) (typed FeaturePython)
  n = 1
  ref = Na_element
FEATURE [App::DocumentObjectGroupPython] G4_Na  # scripted group (container) (typed FeaturePython)
  Dunit = g/cm3
  Dvalue = 0.971
  Group = -> [Na_element020]
  conduct = 2
  density = 1
  expand = 3
  formula = Na
  name = G4_Na
  specific = 4
FEATURE [App::DocumentObjectGroupPython] Mg_element011  label="Mg_element : 005"  # scripted group (container) (typed FeaturePython)
  n = 1
  ref = Mg_element
FEATURE [App::DocumentObjectGroupPython] G4_Mg  # scripted group (container) (typed FeaturePython)
  Dunit = g/cm3
  Dvalue = 1.74
  Group = -> [Mg_element011]
  conduct = 2
  density = 1
  expand = 3
  formula = Mg
  name = G4_Mg
  specific = 4
FEATURE [App::DocumentObjectGroupPython] Al_element004  label="Al_element : 1"  # scripted group (container) (typed FeaturePython)
  n = 1
  ref = Al_element
FEATURE [App::DocumentObjectGroupPython] G4_Al  # scripted group (container) (typed FeaturePython)
  Dunit = g/cm3
  Dvalue = 2.699
  Group = -> [Al_element004]
  conduct = 2
  density = 1
  expand = 3
  formula = Al
  name = G4_Al
  specific = 4
FEATURE [App::DocumentObjectGroupPython] Si_element007  label="Si_element : 002"  # scripted group (container) (typed FeaturePython)
  n = 1
  ref = Si_element
FEATURE [App::DocumentObjectGroupPython] G4_Si  # scripted group (container) (typed FeaturePython)
  Dunit = g/cm3
  Dvalue = 2.33
  Group = -> [Si_element007]
  conduct = 2
  density = 1
  expand = 3
  formula = Si
  name = G4_Si
  specific = 4
FEATURE [App::DocumentObjectGroupPython] P_element013  label="P_element : 002"  # scripted group (container) (typed FeaturePython)
  n = 1
  ref = P_element
FEATURE [App::DocumentObjectGroupPython] G4_P  # scripted group (container) (typed FeaturePython)
  Dunit = g/cm3
  Dvalue = 2.2
  Group = -> [P_element013]
  conduct = 2
  density = 1
  expand = 3
  formula = P
  name = G4_P
  specific = 4
FEATURE [App::DocumentObjectGroupPython] S_element023  label="S_element : 007"  # scripted group (container) (typed FeaturePython)
  n = 1
  ref = S_element
FEATURE [App::DocumentObjectGroupPython] G4_S  # scripted group (container) (typed FeaturePython)
  Dunit = g/cm3
  Dvalue = 2
  Group = -> [S_element023]
  conduct = 2
  density = 1
  expand = 3
  formula = S
  name = G4_S
  specific = 4
FEATURE [App::DocumentObjectGroupPython] Cl_element029  label="Cl_element : 015"  # scripted group (container) (typed FeaturePython)
  n = 1
  ref = Cl_element
FEATURE [App::DocumentObjectGroupPython] G4_Cl  # scripted group (container) (typed FeaturePython)
  Dunit = g/cm3
  Dvalue = 0.00299473
  Group = -> [Cl_element029]
  conduct = 2
  density = 1
  expand = 3
  formula = Cl
  name = G4_Cl
  specific = 4
FEATURE [App::DocumentObjectGroupPython] Ar_element002  label="Ar_element : 1"  # scripted group (container) (typed FeaturePython)
  n = 1
  ref = Ar_element
FEATURE [App::DocumentObjectGroupPython] G4_Ar  # scripted group (container) (typed FeaturePython)
  Dunit = g/cm3
  Dvalue = 0.00166201
  Group = -> [Ar_element002]
  conduct = 2
  density = 1
  expand = 3
  formula = Ar
  name = G4_Ar
  specific = 4
FEATURE [App::DocumentObjectGroupPython] K_element013  label="K_element : 003"  # scripted group (container) (typed FeaturePython)
  n = 1
  ref = K_element
FEATURE [App::DocumentObjectGroupPython] G4_K  # scripted group (container) (typed FeaturePython)
  Dunit = g/cm3
  Dvalue = 0.862
  Group = -> [K_element013]
  conduct = 2
  density = 1
  expand = 3
  formula = K
  name = G4_K
  specific = 4
FEATURE [App::DocumentObjectGroupPython] Ca_element014  label="Ca_element : 007"  # scripted group (container) (typed FeaturePython)
  n = 1
  ref = Ca_element
FEATURE [App::DocumentObjectGroupPython] G4_Ca  # scripted group (container) (typed FeaturePython)
  Dunit = g/cm3
  Dvalue = 1.55
  Group = -> [Ca_element014]
  conduct = 2
  density = 1
  expand = 3
  formula = Ca
  name = G4_Ca
  specific = 4
FEATURE [App::DocumentObjectGroupPython] Sc_element001  label="Sc_element : 1"  # scripted group (container) (typed FeaturePython)
  n = 1
  ref = Sc_element
FEATURE [App::DocumentObjectGroupPython] G4_Sc  # scripted group (container) (typed FeaturePython)
  Dunit = g/cm3
  Dvalue = 2.989
  Group = -> [Sc_element001]
  conduct = 2
  density = 1
  expand = 3
  formula = Sc
  name = G4_Sc
  specific = 4
FEATURE [App::DocumentObjectGroupPython] Ti_element004  label="Ti_element : 002"  # scripted group (container) (typed FeaturePython)
  n = 1
  ref = Ti_element
FEATURE [App::DocumentObjectGroupPython] G4_Ti  # scripted group (container) (typed FeaturePython)
  Dunit = g/cm3
  Dvalue = 4.54
  Group = -> [Ti_element004]
  conduct = 2
  density = 1
  expand = 3
  formula = Ti
  name = G4_Ti
  specific = 4
FEATURE [App::DocumentObjectGroupPython] V_element001  label="V_element : 1"  # scripted group (container) (typed FeaturePython)
  n = 1
  ref = V_element
FEATURE [App::DocumentObjectGroupPython] G4_V  # scripted group (container) (typed FeaturePython)
  Dunit = g/cm3
  Dvalue = 6.11
  Group = -> [V_element001]
  conduct = 2
  density = 1
  expand = 3
  formula = V
  name = G4_V
  specific = 4
FEATURE [App::DocumentObjectGroupPython] Cr_element001  label="Cr_element : 1"  # scripted group (container) (typed FeaturePython)
  n = 1
  ref = Cr_element
FEATURE [App::DocumentObjectGroupPython] G4_Cr  # scripted group (container) (typed FeaturePython)
  Dunit = g/cm3
  Dvalue = 7.18
  Group = -> [Cr_element001]
  conduct = 2
  density = 1
  expand = 3
  formula = Cr
  name = G4_Cr
  specific = 4
FEATURE [App::DocumentObjectGroupPython] Mn_element001  label="Mn_element : 1"  # scripted group (container) (typed FeaturePython)
  n = 1
  ref = Mn_element
FEATURE [App::DocumentObjectGroupPython] G4_Mn  # scripted group (container) (typed FeaturePython)
  Dunit = g/cm3
  Dvalue = 7.44
  Group = -> [Mn_element001]
  conduct = 2
  density = 1
  expand = 3
  formula = Mn
  name = G4_Mn
  specific = 4
FEATURE [App::DocumentObjectGroupPython] Fe_element007  label="Fe_element : 004"  # scripted group (container) (typed FeaturePython)
  n = 1
  ref = Fe_element
FEATURE [App::DocumentObjectGroupPython] G4_Fe  # scripted group (container) (typed FeaturePython)
  Dunit = g/cm3
  Dvalue = 7.874
  Group = -> [Fe_element007]
  conduct = 2
  density = 1
  expand = 3
  formula = Fe
  name = G4_Fe
  specific = 4
FEATURE [App::DocumentObjectGroupPython] Co_element001  label="Co_element : 1"  # scripted group (container) (typed FeaturePython)
  n = 1
  ref = Co_element
FEATURE [App::DocumentObjectGroupPython] G4_Co  # scripted group (container) (typed FeaturePython)
  Dunit = g/cm3
  Dvalue = 8.9
  Group = -> [Co_element001]
  conduct = 2
  density = 1
  expand = 3
  formula = Co
  name = G4_Co
  specific = 4
FEATURE [App::DocumentObjectGroupPython] Ni_element001  label="Ni_element : 1"  # scripted group (container) (typed FeaturePython)
  n = 1
  ref = Ni_element
FEATURE [App::DocumentObjectGroupPython] G4_Ni  # scripted group (container) (typed FeaturePython)
  Dunit = g/cm3
  Dvalue = 8.902
  Group = -> [Ni_element001]
  conduct = 2
  density = 1
  expand = 3
  formula = Ni
  name = G4_Ni
  specific = 4
FEATURE [App::DocumentObjectGroupPython] Cu_element001  label="Cu_element : 1"  # scripted group (container) (typed FeaturePython)
  n = 1
  ref = Cu_element
FEATURE [App::DocumentObjectGroupPython] G4_Cu  # scripted group (container) (typed FeaturePython)
  Dunit = g/cm3
  Dvalue = 8.96
  Group = -> [Cu_element001]
  conduct = 2
  density = 1
  expand = 3
  formula = Cu
  name = G4_Cu
  specific = 4
FEATURE [App::DocumentObjectGroupPython] Zn_element001  label="Zn_element : 1"  # scripted group (container) (typed FeaturePython)
  n = 1
  ref = Zn_element
FEATURE [App::DocumentObjectGroupPython] G4_Zn  # scripted group (container) (typed FeaturePython)
  Dunit = g/cm3
  Dvalue = 7.133
  Group = -> [Zn_element001]
  conduct = 2
  density = 1
  expand = 3
  formula = Zn
  name = G4_Zn
  specific = 4
FEATURE [App::DocumentObjectGroupPython] Ga_element002  label="Ga_element : 002"  # scripted group (container) (typed FeaturePython)
  n = 1
  ref = Ga_element
FEATURE [App::DocumentObjectGroupPython] G4_Ga  # scripted group (container) (typed FeaturePython)
  Dunit = g/cm3
  Dvalue = 5.904
  Group = -> [Ga_element002]
  conduct = 2
  density = 1
  expand = 3
  formula = Ga
  name = G4_Ga
  specific = 4
FEATURE [App::DocumentObjectGroupPython] Ge_element002  label="Ge_element : 1"  # scripted group (container) (typed FeaturePython)
  n = 1
  ref = Ge_element
FEATURE [App::DocumentObjectGroupPython] G4_Ge  # scripted group (container) (typed FeaturePython)
  Dunit = g/cm3
  Dvalue = 5.323
  Group = -> [Ge_element002]
  conduct = 2
  density = 1
  expand = 3
  formula = Ge
  name = G4_Ge
  specific = 4
FEATURE [App::DocumentObjectGroupPython] As_element003  label="As_element : 002"  # scripted group (container) (typed FeaturePython)
  n = 1
  ref = As_element
FEATURE [App::DocumentObjectGroupPython] G4_As  # scripted group (container) (typed FeaturePython)
  Dunit = g/cm3
  Dvalue = 5.73
  Group = -> [As_element003]
  conduct = 2
  density = 1
  expand = 3
  formula = As
  name = G4_As
  specific = 4
FEATURE [App::DocumentObjectGroupPython] Se_element001  label="Se_element : 1"  # scripted group (container) (typed FeaturePython)
  n = 1
  ref = Se_element
FEATURE [App::DocumentObjectGroupPython] G4_Se  # scripted group (container) (typed FeaturePython)
  Dunit = g/cm3
  Dvalue = 4.5
  Group = -> [Se_element001]
  conduct = 2
  density = 1
  expand = 3
  formula = Se
  name = G4_Se
  specific = 4
FEATURE [App::DocumentObjectGroupPython] Br_element007  label="Br_element : 004"  # scripted group (container) (typed FeaturePython)
  n = 1
  ref = Br_element
FEATURE [App::DocumentObjectGroupPython] G4_Br  # scripted group (container) (typed FeaturePython)
  Dunit = g/cm3
  Dvalue = 0.0070721
  Group = -> [Br_element007]
  conduct = 2
  density = 1
  expand = 3
  formula = Br
  name = G4_Br
  specific = 4
FEATURE [App::DocumentObjectGroupPython] Kr_element001  label="Kr_element : 1"  # scripted group (container) (typed FeaturePython)
  n = 1
  ref = Kr_element
FEATURE [App::DocumentObjectGroupPython] G4_Kr  # scripted group (container) (typed FeaturePython)
  Dunit = g/cm3
  Dvalue = 0.00347832
  Group = -> [Kr_element001]
  conduct = 2
  density = 1
  expand = 3
  formula = Kr
  name = G4_Kr
  specific = 4
FEATURE [App::DocumentObjectGroupPython] Rb_element001  label="Rb_element : 1"  # scripted group (container) (typed FeaturePython)
  n = 1
  ref = Rb_element
FEATURE [App::DocumentObjectGroupPython] G4_Rb  # scripted group (container) (typed FeaturePython)
  Dunit = g/cm3
  Dvalue = 1.532
  Group = -> [Rb_element001]
  conduct = 2
  density = 1
  expand = 3
  formula = Rb
  name = G4_Rb
  specific = 4
FEATURE [App::DocumentObjectGroupPython] Sr_element001  label="Sr_element : 1"  # scripted group (container) (typed FeaturePython)
  n = 1
  ref = Sr_element
FEATURE [App::DocumentObjectGroupPython] G4_Sr  # scripted group (container) (typed FeaturePython)
  Dunit = g/cm3
  Dvalue = 2.54
  Group = -> [Sr_element001]
  conduct = 2
  density = 1
  expand = 3
  formula = Sr
  name = G4_Sr
  specific = 4
FEATURE [App::DocumentObjectGroupPython] Y_element001  label="Y_element : 1"  # scripted group (container) (typed FeaturePython)
  n = 1
  ref = Y_element
FEATURE [App::DocumentObjectGroupPython] G4_Y  # scripted group (container) (typed FeaturePython)
  Dunit = g/cm3
  Dvalue = 4.469
  Group = -> [Y_element001]
  conduct = 2
  density = 1
  expand = 3
  formula = Y
  name = G4_Y
  specific = 4
FEATURE [App::DocumentObjectGroupPython] Zr_element001  label="Zr_element : 1"  # scripted group (container) (typed FeaturePython)
  n = 1
  ref = Zr_element
FEATURE [App::DocumentObjectGroupPython] G4_Zr  # scripted group (container) (typed FeaturePython)
  Dunit = g/cm3
  Dvalue = 6.506
  Group = -> [Zr_element001]
  conduct = 2
  density = 1
  expand = 3
  formula = Zr
  name = G4_Zr
  specific = 4
FEATURE [App::DocumentObjectGroupPython] Nb_element001  label="Nb_element : 1"  # scripted group (container) (typed FeaturePython)
  n = 1
  ref = Nb_element
FEATURE [App::DocumentObjectGroupPython] G4_Nb  # scripted group (container) (typed FeaturePython)
  Dunit = g/cm3
  Dvalue = 8.57
  Group = -> [Nb_element001]
  conduct = 2
  density = 1
  expand = 3
  formula = Nb
  name = G4_Nb
  specific = 4
FEATURE [App::DocumentObjectGroupPython] Mo_element001  label="Mo_element : 1"  # scripted group (container) (typed FeaturePython)
  n = 1
  ref = Mo_element
FEATURE [App::DocumentObjectGroupPython] G4_Mo  # scripted group (container) (typed FeaturePython)
  Dunit = g/cm3
  Dvalue = 10.22
  Group = -> [Mo_element001]
  conduct = 2
  density = 1
  expand = 3
  formula = Mo
  name = G4_Mo
  specific = 4
FEATURE [App::DocumentObjectGroupPython] Tc_element001  label="Tc_element : 1"  # scripted group (container) (typed FeaturePython)
  n = 1
  ref = Tc_element
FEATURE [App::DocumentObjectGroupPython] G4_Tc  # scripted group (container) (typed FeaturePython)
  Dunit = g/cm3
  Dvalue = 11.5
  Group = -> [Tc_element001]
  conduct = 2
  density = 1
  expand = 3
  formula = Tc
  name = G4_Tc
  specific = 4
FEATURE [App::DocumentObjectGroupPython] Ru_element001  label="Ru_element : 1"  # scripted group (container) (typed FeaturePython)
  n = 1
  ref = Ru_element
FEATURE [App::DocumentObjectGroupPython] G4_Ru  # scripted group (container) (typed FeaturePython)
  Dunit = g/cm3
  Dvalue = 12.41
  Group = -> [Ru_element001]
  conduct = 2
  density = 1
  expand = 3
  formula = Ru
  name = G4_Ru
  specific = 4
FEATURE [App::DocumentObjectGroupPython] Rh_element001  label="Rh_element : 1"  # scripted group (container) (typed FeaturePython)
  n = 1
  ref = Rh_element
FEATURE [App::DocumentObjectGroupPython] G4_Rh  # scripted group (container) (typed FeaturePython)
  Dunit = g/cm3
  Dvalue = 12.41
  Group = -> [Rh_element001]
  conduct = 2
  density = 1
  expand = 3
  formula = Rh
  name = G4_Rh
  specific = 4
FEATURE [App::DocumentObjectGroupPython] Pd_element001  label="Pd_element : 1"  # scripted group (container) (typed FeaturePython)
  n = 1
  ref = Pd_element
FEATURE [App::DocumentObjectGroupPython] G4_Pd  # scripted group (container) (typed FeaturePython)
  Dunit = g/cm3
  Dvalue = 12.02
  Group = -> [Pd_element001]
  conduct = 2
  density = 1
  expand = 3
  formula = Pd
  name = G4_Pd
  specific = 4
FEATURE [App::DocumentObjectGroupPython] Ag_element006  label="Ag_element : 004"  # scripted group (container) (typed FeaturePython)
  n = 1
  ref = Ag_element
FEATURE [App::DocumentObjectGroupPython] G4_Ag  # scripted group (container) (typed FeaturePython)
  Dunit = g/cm3
  Dvalue = 10.5
  Group = -> [Ag_element006]
  conduct = 2
  density = 1
  expand = 3
  formula = Ag
  name = G4_Ag
  specific = 4
FEATURE [App::DocumentObjectGroupPython] Cd_element003  label="Cd_element : 003"  # scripted group (container) (typed FeaturePython)
  n = 1
  ref = Cd_element
FEATURE [App::DocumentObjectGroupPython] G4_Cd  # scripted group (container) (typed FeaturePython)
  Dunit = g/cm3
  Dvalue = 8.65
  Group = -> [Cd_element003]
  conduct = 2
  density = 1
  expand = 3
  formula = Cd
  name = G4_Cd
  specific = 4
FEATURE [App::DocumentObjectGroupPython] In_element001  label="In_element : 1"  # scripted group (container) (typed FeaturePython)
  n = 1
  ref = In_element
FEATURE [App::DocumentObjectGroupPython] G4_In  # scripted group (container) (typed FeaturePython)
  Dunit = g/cm3
  Dvalue = 7.31
  Group = -> [In_element001]
  conduct = 2
  density = 1
  expand = 3
  formula = In
  name = G4_In
  specific = 4
FEATURE [App::DocumentObjectGroupPython] Sn_element001  label="Sn_element : 1"  # scripted group (container) (typed FeaturePython)
  n = 1
  ref = Sn_element
FEATURE [App::DocumentObjectGroupPython] G4_Sn  # scripted group (container) (typed FeaturePython)
  Dunit = g/cm3
  Dvalue = 7.31
  Group = -> [Sn_element001]
  conduct = 2
  density = 1
  expand = 3
  formula = Sn
  name = G4_Sn
  specific = 4
FEATURE [App::DocumentObjectGroupPython] Sb_element001  label="Sb_element : 1"  # scripted group (container) (typed FeaturePython)
  n = 1
  ref = Sb_element
FEATURE [App::DocumentObjectGroupPython] G4_Sb  # scripted group (container) (typed FeaturePython)
  Dunit = g/cm3
  Dvalue = 6.691
  Group = -> [Sb_element001]
  conduct = 2
  density = 1
  expand = 3
  formula = Sb
  name = G4_Sb
  specific = 4
FEATURE [App::DocumentObjectGroupPython] Te_element002  label="Te_element : 002"  # scripted group (container) (typed FeaturePython)
  n = 1
  ref = Te_element
FEATURE [App::DocumentObjectGroupPython] G4_Te  # scripted group (container) (typed FeaturePython)
  Dunit = g/cm3
  Dvalue = 6.24
  Group = -> [Te_element002]
  conduct = 2
  density = 1
  expand = 3
  formula = Te
  name = G4_Te
  specific = 4
FEATURE [App::DocumentObjectGroupPython] I_element010  label="I_element : 006"  # scripted group (container) (typed FeaturePython)
  n = 1
  ref = I_element
FEATURE [App::DocumentObjectGroupPython] G4_I  # scripted group (container) (typed FeaturePython)
  Dunit = g/cm3
  Dvalue = 4.93
  Group = -> [I_element010]
  conduct = 2
  density = 1
  expand = 3
  formula = I
  name = G4_I
  specific = 4
FEATURE [App::DocumentObjectGroupPython] Xe_element001  label="Xe_element : 1"  # scripted group (container) (typed FeaturePython)
  n = 1
  ref = Xe_element
FEATURE [App::DocumentObjectGroupPython] G4_Xe  # scripted group (container) (typed FeaturePython)
  Dunit = g/cm3
  Dvalue = 0.00548536
  Group = -> [Xe_element001]
  conduct = 2
  density = 1
  expand = 3
  formula = Xe
  name = G4_Xe
  specific = 4
FEATURE [App::DocumentObjectGroupPython] Cs_element003  label="Cs_element : 003"  # scripted group (container) (typed FeaturePython)
  n = 1
  ref = Cs_element
FEATURE [App::DocumentObjectGroupPython] G4_Cs  # scripted group (container) (typed FeaturePython)
  Dunit = g/cm3
  Dvalue = 1.873
  Group = -> [Cs_element003]
  conduct = 2
  density = 1
  expand = 3
  formula = Cs
  name = G4_Cs
  specific = 4
FEATURE [App::DocumentObjectGroupPython] Ba_element003  label="Ba_element : 003"  # scripted group (container) (typed FeaturePython)
  n = 1
  ref = Ba_element
FEATURE [App::DocumentObjectGroupPython] G4_Ba  # scripted group (container) (typed FeaturePython)
  Dunit = g/cm3
  Dvalue = 3.5
  Group = -> [Ba_element003]
  conduct = 2
  density = 1
  expand = 3
  formula = Ba
  name = G4_Ba
  specific = 4
FEATURE [App::DocumentObjectGroupPython] La_element003  label="La_element : 003"  # scripted group (container) (typed FeaturePython)
  n = 1
  ref = La_element
FEATURE [App::DocumentObjectGroupPython] G4_La  # scripted group (container) (typed FeaturePython)
  Dunit = g/cm3
  Dvalue = 6.154
  Group = -> [La_element003]
  conduct = 2
  density = 1
  expand = 3
  formula = La
  name = G4_La
  specific = 4
FEATURE [App::DocumentObjectGroupPython] Ce_element002  label="Ce_element : 1"  # scripted group (container) (typed FeaturePython)
  n = 1
  ref = Ce_element
FEATURE [App::DocumentObjectGroupPython] G4_Ce  # scripted group (container) (typed FeaturePython)
  Dunit = g/cm3
  Dvalue = 6.657
  Group = -> [Ce_element002]
  conduct = 2
  density = 1
  expand = 3
  formula = Ce
  name = G4_Ce
  specific = 4
FEATURE [App::DocumentObjectGroupPython] Pr_element001  label="Pr_element : 1"  # scripted group (container) (typed FeaturePython)
  n = 1
  ref = Pr_element
FEATURE [App::DocumentObjectGroupPython] G4_Pr  # scripted group (container) (typed FeaturePython)
  Dunit = g/cm3
  Dvalue = 6.71
  Group = -> [Pr_element001]
  conduct = 2
  density = 1
  expand = 3
  formula = Pr
  name = G4_Pr
  specific = 4
FEATURE [App::DocumentObjectGroupPython] Nd_element001  label="Nd_element : 1"  # scripted group (container) (typed FeaturePython)
  n = 1
  ref = Nd_element
FEATURE [App::DocumentObjectGroupPython] G4_Nd  # scripted group (container) (typed FeaturePython)
  Dunit = g/cm3
  Dvalue = 6.9
  Group = -> [Nd_element001]
  conduct = 2
  density = 1
  expand = 3
  formula = Nd
  name = G4_Nd
  specific = 4
FEATURE [App::DocumentObjectGroupPython] Pm_element001  label="Pm_element : 1"  # scripted group (container) (typed FeaturePython)
  n = 1
  ref = Pm_element
FEATURE [App::DocumentObjectGroupPython] G4_Pm  # scripted group (container) (typed FeaturePython)
  Dunit = g/cm3
  Dvalue = 7.22
  Group = -> [Pm_element001]
  conduct = 2
  density = 1
  expand = 3
  formula = Pm
  name = G4_Pm
  specific = 4
FEATURE [App::DocumentObjectGroupPython] Sm_element001  label="Sm_element : 1"  # scripted group (container) (typed FeaturePython)
  n = 1
  ref = Sm_element
FEATURE [App::DocumentObjectGroupPython] G4_Sm  # scripted group (container) (typed FeaturePython)
  Dunit = g/cm3
  Dvalue = 7.46
  Group = -> [Sm_element001]
  conduct = 2
  density = 1
  expand = 3
  formula = Sm
  name = G4_Sm
  specific = 4
FEATURE [App::DocumentObjectGroupPython] Eu_element001  label="Eu_element : 1"  # scripted group (container) (typed FeaturePython)
  n = 1
  ref = Eu_element
FEATURE [App::DocumentObjectGroupPython] G4_Eu  # scripted group (container) (typed FeaturePython)
  Dunit = g/cm3
  Dvalue = 5.243
  Group = -> [Eu_element001]
  conduct = 2
  density = 1
  expand = 3
  formula = Eu
  name = G4_Eu
  specific = 4
FEATURE [App::DocumentObjectGroupPython] Gd_element002  label="Gd_element : 1"  # scripted group (container) (typed FeaturePython)
  n = 1
  ref = Gd_element
FEATURE [App::DocumentObjectGroupPython] G4_Gd  # scripted group (container) (typed FeaturePython)
  Dunit = g/cm3
  Dvalue = 7.9004
  Group = -> [Gd_element002]
  conduct = 2
  density = 1
  expand = 3
  formula = Gd
  name = G4_Gd
  specific = 4
FEATURE [App::DocumentObjectGroupPython] Tb_element001  label="Tb_element : 1"  # scripted group (container) (typed FeaturePython)
  n = 1
  ref = Tb_element
FEATURE [App::DocumentObjectGroupPython] G4_Tb  # scripted group (container) (typed FeaturePython)
  Dunit = g/cm3
  Dvalue = 8.229
  Group = -> [Tb_element001]
  conduct = 2
  density = 1
  expand = 3
  formula = Tb
  name = G4_Tb
  specific = 4
FEATURE [App::DocumentObjectGroupPython] Dy_element001  label="Dy_element : 1"  # scripted group (container) (typed FeaturePython)
  n = 1
  ref = Dy_element
FEATURE [App::DocumentObjectGroupPython] G4_Dy  # scripted group (container) (typed FeaturePython)
  Dunit = g/cm3
  Dvalue = 8.55
  Group = -> [Dy_element001]
  conduct = 2
  density = 1
  expand = 3
  formula = Dy
  name = G4_Dy
  specific = 4
FEATURE [App::DocumentObjectGroupPython] Ho_element001  label="Ho_element : 1"  # scripted group (container) (typed FeaturePython)
  n = 1
  ref = Ho_element
FEATURE [App::DocumentObjectGroupPython] G4_Ho  # scripted group (container) (typed FeaturePython)
  Dunit = g/cm3
  Dvalue = 8.795
  Group = -> [Ho_element001]
  conduct = 2
  density = 1
  expand = 3
  formula = Ho
  name = G4_Ho
  specific = 4
FEATURE [App::DocumentObjectGroupPython] Er_element001  label="Er_element : 1"  # scripted group (container) (typed FeaturePython)
  n = 1
  ref = Er_element
FEATURE [App::DocumentObjectGroupPython] G4_Er  # scripted group (container) (typed FeaturePython)
  Dunit = g/cm3
  Dvalue = 9.066
  Group = -> [Er_element001]
  conduct = 2
  density = 1
  expand = 3
  formula = Er
  name = G4_Er
  specific = 4
FEATURE [App::DocumentObjectGroupPython] Tm_element001  label="Tm_element : 1"  # scripted group (container) (typed FeaturePython)
  n = 1
  ref = Tm_element
FEATURE [App::DocumentObjectGroupPython] G4_Tm  # scripted group (container) (typed FeaturePython)
  Dunit = g/cm3
  Dvalue = 9.321
  Group = -> [Tm_element001]
  conduct = 2
  density = 1
  expand = 3
  formula = Tm
  name = G4_Tm
  specific = 4
FEATURE [App::DocumentObjectGroupPython] Yb_element001  label="Yb_element : 1"  # scripted group (container) (typed FeaturePython)
  n = 1
  ref = Yb_element
FEATURE [App::DocumentObjectGroupPython] G4_Yb  # scripted group (container) (typed FeaturePython)
  Dunit = g/cm3
  Dvalue = 6.73
  Group = -> [Yb_element001]
  conduct = 2
  density = 1
  expand = 3
  formula = Yb
  name = G4_Yb
  specific = 4
FEATURE [App::DocumentObjectGroupPython] Lu_element001  label="Lu_element : 1"  # scripted group (container) (typed FeaturePython)
  n = 1
  ref = Lu_element
FEATURE [App::DocumentObjectGroupPython] G4_Lu  # scripted group (container) (typed FeaturePython)
  Dunit = g/cm3
  Dvalue = 9.84
  Group = -> [Lu_element001]
  conduct = 2
  density = 1
  expand = 3
  formula = Lu
  name = G4_Lu
  specific = 4
FEATURE [App::DocumentObjectGroupPython] Hf_element001  label="Hf_element : 1"  # scripted group (container) (typed FeaturePython)
  n = 1
  ref = Hf_element
FEATURE [App::DocumentObjectGroupPython] G4_Hf  # scripted group (container) (typed FeaturePython)
  Dunit = g/cm3
  Dvalue = 13.31
  Group = -> [Hf_element001]
  conduct = 2
  density = 1
  expand = 3
  formula = Hf
  name = G4_Hf
  specific = 4
FEATURE [App::DocumentObjectGroupPython] Ta_element001  label="Ta_element : 1"  # scripted group (container) (typed FeaturePython)
  n = 1
  ref = Ta_element
FEATURE [App::DocumentObjectGroupPython] G4_Ta  # scripted group (container) (typed FeaturePython)
  Dunit = g/cm3
  Dvalue = 16.654
  Group = -> [Ta_element001]
  conduct = 2
  density = 1
  expand = 3
  formula = Ta
  name = G4_Ta
  specific = 4
FEATURE [App::DocumentObjectGroupPython] W_element004  label="W_element : 004"  # scripted group (container) (typed FeaturePython)
  n = 1
  ref = W_element
FEATURE [App::DocumentObjectGroupPython] G4_W  # scripted group (container) (typed FeaturePython)
  Dunit = g/cm3
  Dvalue = 19.3
  Group = -> [W_element004]
  conduct = 2
  density = 1
  expand = 3
  formula = W
  name = G4_W
  specific = 4
FEATURE [App::DocumentObjectGroupPython] Re_element001  label="Re_element : 1"  # scripted group (container) (typed FeaturePython)
  n = 1
  ref = Re_element
FEATURE [App::DocumentObjectGroupPython] G4_Re  # scripted group (container) (typed FeaturePython)
  Dunit = g/cm3
  Dvalue = 21.02
  Group = -> [Re_element001]
  conduct = 2
  density = 1
  expand = 3
  formula = Re
  name = G4_Re
  specific = 4
FEATURE [App::DocumentObjectGroupPython] Os_element001  label="Os_element : 1"  # scripted group (container) (typed FeaturePython)
  n = 1
  ref = Os_element
FEATURE [App::DocumentObjectGroupPython] G4_Os  # scripted group (container) (typed FeaturePython)
  Dunit = g/cm3
  Dvalue = 22.57
  Group = -> [Os_element001]
  conduct = 2
  density = 1
  expand = 3
  formula = Os
  name = G4_Os
  specific = 4
FEATURE [App::DocumentObjectGroupPython] Ir_element001  label="Ir_element : 1"  # scripted group (container) (typed FeaturePython)
  n = 1
  ref = Ir_element
FEATURE [App::DocumentObjectGroupPython] G4_Ir  # scripted group (container) (typed FeaturePython)
  Dunit = g/cm3
  Dvalue = 22.42
  Group = -> [Ir_element001]
  conduct = 2
  density = 1
  expand = 3
  formula = Ir
  name = G4_Ir
  specific = 4
FEATURE [App::DocumentObjectGroupPython] Pt_element001  label="Pt_element : 1"  # scripted group (container) (typed FeaturePython)
  n = 1
  ref = Pt_element
FEATURE [App::DocumentObjectGroupPython] G4_Pt  # scripted group (container) (typed FeaturePython)
  Dunit = g/cm3
  Dvalue = 21.45
  Group = -> [Pt_element001]
  conduct = 2
  density = 1
  expand = 3
  formula = Pt
  name = G4_Pt
  specific = 4
FEATURE [App::DocumentObjectGroupPython] Au_element001  label="Au_element : 1"  # scripted group (container) (typed FeaturePython)
  n = 1
  ref = Au_element
FEATURE [App::DocumentObjectGroupPython] G4_Au  # scripted group (container) (typed FeaturePython)
  Dunit = g/cm3
  Dvalue = 19.32
  Group = -> [Au_element001]
  conduct = 2
  density = 1
  expand = 3
  formula = Au
  name = G4_Au
  specific = 4
FEATURE [App::DocumentObjectGroupPython] Hg_element002  label="Hg_element : 002"  # scripted group (container) (typed FeaturePython)
  n = 1
  ref = Hg_element
FEATURE [App::DocumentObjectGroupPython] G4_Hg  # scripted group (container) (typed FeaturePython)
  Dunit = g/cm3
  Dvalue = 13.546
  Group = -> [Hg_element002]
  conduct = 2
  density = 1
  expand = 3
  formula = Hg
  name = G4_Hg
  specific = 4
FEATURE [App::DocumentObjectGroupPython] Tl_element002  label="Tl_element : 002"  # scripted group (container) (typed FeaturePython)
  n = 1
  ref = Tl_element
FEATURE [App::DocumentObjectGroupPython] G4_Tl  # scripted group (container) (typed FeaturePython)
  Dunit = g/cm3
  Dvalue = 11.72
  Group = -> [Tl_element002]
  conduct = 2
  density = 1
  expand = 3
  formula = Tl
  name = G4_Tl
  specific = 4
FEATURE [App::DocumentObjectGroupPython] Pb_element003  label="Pb_element : 1"  # scripted group (container) (typed FeaturePython)
  n = 1
  ref = Pb_element
FEATURE [App::DocumentObjectGroupPython] G4_Pb  # scripted group (container) (typed FeaturePython)
  Dunit = g/cm3
  Dvalue = 11.35
  Group = -> [Pb_element003]
  conduct = 2
  density = 1
  expand = 3
  formula = Pb
  name = G4_Pb
  specific = 4
FEATURE [App::DocumentObjectGroupPython] Bi_element002  label="Bi_element : 1"  # scripted group (container) (typed FeaturePython)
  n = 1
  ref = Bi_element
FEATURE [App::DocumentObjectGroupPython] G4_Bi  # scripted group (container) (typed FeaturePython)
  Dunit = g/cm3
  Dvalue = 9.747
  Group = -> [Bi_element002]
  conduct = 2
  density = 1
  expand = 3
  formula = Bi
  name = G4_Bi
  specific = 4
FEATURE [App::DocumentObjectGroupPython] Po_element001  label="Po_element : 1"  # scripted group (container) (typed FeaturePython)
  n = 1
  ref = Po_element
FEATURE [App::DocumentObjectGroupPython] G4_Po  # scripted group (container) (typed FeaturePython)
  Dunit = g/cm3
  Dvalue = 9.32
  Group = -> [Po_element001]
  conduct = 2
  density = 1
  expand = 3
  formula = Po
  name = G4_Po
  specific = 4
FEATURE [App::DocumentObjectGroupPython] At_element001  label="At_element : 1"  # scripted group (container) (typed FeaturePython)
  n = 1
  ref = At_element
FEATURE [App::DocumentObjectGroupPython] G4_At  # scripted group (container) (typed FeaturePython)
  Dunit = g/cm3
  Dvalue = 9.32
  Group = -> [At_element001]
  conduct = 2
  density = 1
  expand = 3
  formula = At
  name = G4_At
  specific = 4
FEATURE [App::DocumentObjectGroupPython] Rn_element001  label="Rn_element : 1"  # scripted group (container) (typed FeaturePython)
  n = 1
  ref = Rn_element
FEATURE [App::DocumentObjectGroupPython] G4_Rn  # scripted group (container) (typed FeaturePython)
  Dunit = g/cm3
  Dvalue = 0.00900662
  Group = -> [Rn_element001]
  conduct = 2
  density = 1
  expand = 3
  formula = Rn
  name = G4_Rn
  specific = 4
FEATURE [App::DocumentObjectGroupPython] Fr_element001  label="Fr_element : 1"  # scripted group (container) (typed FeaturePython)
  n = 1
  ref = Fr_element
FEATURE [App::DocumentObjectGroupPython] G4_Fr  # scripted group (container) (typed FeaturePython)
  Dunit = g/cm3
  Dvalue = 1
  Group = -> [Fr_element001]
  conduct = 2
  density = 1
  expand = 3
  formula = Fr
  name = G4_Fr
  specific = 4
FEATURE [App::DocumentObjectGroupPython] Ra_element001  label="Ra_element : 1"  # scripted group (container) (typed FeaturePython)
  n = 1
  ref = Ra_element
FEATURE [App::DocumentObjectGroupPython] G4_Ra  # scripted group (container) (typed FeaturePython)
  Dunit = g/cm3
  Dvalue = 5
  Group = -> [Ra_element001]
  conduct = 2
  density = 1
  expand = 3
  formula = Ra
  name = G4_Ra
  specific = 4
FEATURE [App::DocumentObjectGroupPython] Ac_element001  label="Ac_element : 1"  # scripted group (container) (typed FeaturePython)
  n = 1
  ref = Ac_element
FEATURE [App::DocumentObjectGroupPython] G4_Ac  # scripted group (container) (typed FeaturePython)
  Dunit = g/cm3
  Dvalue = 10.07
  Group = -> [Ac_element001]
  conduct = 2
  density = 1
  expand = 3
  formula = Ac
  name = G4_Ac
  specific = 4
FEATURE [App::DocumentObjectGroupPython] Th_element001  label="Th_element : 1"  # scripted group (container) (typed FeaturePython)
  n = 1
  ref = Th_element
FEATURE [App::DocumentObjectGroupPython] G4_Th  # scripted group (container) (typed FeaturePython)
  Dunit = g/cm3
  Dvalue = 11.72
  Group = -> [Th_element001]
  conduct = 2
  density = 1
  expand = 3
  formula = Th
  name = G4_Th
  specific = 4
FEATURE [App::DocumentObjectGroupPython] Pa_element001  label="Pa_element : 1"  # scripted group (container) (typed FeaturePython)
  n = 1
  ref = Pa_element
FEATURE [App::DocumentObjectGroupPython] G4_Pa  # scripted group (container) (typed FeaturePython)
  Dunit = g/cm3
  Dvalue = 15.37
  Group = -> [Pa_element001]
  conduct = 2
  density = 1
  expand = 3
  formula = Pa
  name = G4_Pa
  specific = 4
FEATURE [App::DocumentObjectGroupPython] U_element004  label="U_element : 004"  # scripted group (container) (typed FeaturePython)
  n = 1
  ref = U_element
FEATURE [App::DocumentObjectGroupPython] G4_U  # scripted group (container) (typed FeaturePython)
  Dunit = g/cm3
  Dvalue = 18.95
  Group = -> [U_element004]
  conduct = 2
  density = 1
  expand = 3
  formula = U
  name = G4_U
  specific = 4
FEATURE [App::DocumentObjectGroupPython] Np_element001  label="Np_element : 1"  # scripted group (container) (typed FeaturePython)
  n = 1
  ref = Np_element
FEATURE [App::DocumentObjectGroupPython] G4_Np  # scripted group (container) (typed FeaturePython)
  Dunit = g/cm3
  Dvalue = 20.25
  Group = -> [Np_element001]
  conduct = 2
  density = 1
  expand = 3
  formula = Np
  name = G4_Np
  specific = 4
FEATURE [App::DocumentObjectGroupPython] Pu_element002  label="Pu_element : 002"  # scripted group (container) (typed FeaturePython)
  n = 1
  ref = Pu_element
FEATURE [App::DocumentObjectGroupPython] G4_Pu  # scripted group (container) (typed FeaturePython)
  Dunit = g/cm3
  Dvalue = 19.84
  Group = -> [Pu_element002]
  conduct = 2
  density = 1
  expand = 3
  formula = Pu
  name = G4_Pu
  specific = 4
FEATURE [App::DocumentObjectGroupPython] Am_element001  label="Am_element : 1"  # scripted group (container) (typed FeaturePython)
  n = 1
  ref = Am_element
FEATURE [App::DocumentObjectGroupPython] G4_Am  # scripted group (container) (typed FeaturePython)
  Dunit = g/cm3
  Dvalue = 13.67
  Group = -> [Am_element001]
  conduct = 2
  density = 1
  expand = 3
  formula = Am
  name = G4_Am
  specific = 4
FEATURE [App::DocumentObjectGroupPython] Cm_element001  label="Cm_element : 1"  # scripted group (container) (typed FeaturePython)
  n = 1
  ref = Cm_element
FEATURE [App::DocumentObjectGroupPython] G4_Cm  # scripted group (container) (typed FeaturePython)
  Dunit = g/cm3
  Dvalue = 13.51
  Group = -> [Cm_element001]
  conduct = 2
  density = 1
  expand = 3
  formula = Cm
  name = G4_Cm
  specific = 4
FEATURE [App::DocumentObjectGroupPython] Bk_element001  label="Bk_element : 1"  # scripted group (container) (typed FeaturePython)
  n = 1
  ref = Bk_element
FEATURE [App::DocumentObjectGroupPython] G4_Bk  # scripted group (container) (typed FeaturePython)
  Dunit = g/cm3
  Dvalue = 14
  Group = -> [Bk_element001]
  conduct = 2
  density = 1
  expand = 3
  formula = Bk
  name = G4_Bk
  specific = 4
FEATURE [App::DocumentObjectGroupPython] Cf_element001  label="Cf_element : 1"  # scripted group (container) (typed FeaturePython)
  n = 1
  ref = Cf_element
FEATURE [App::DocumentObjectGroupPython] G4_Cf  # scripted group (container) (typed FeaturePython)
  Dunit = g/cm3
  Dvalue = 10
  Group = -> [Cf_element001]
  conduct = 2
  density = 1
  expand = 3
  formula = Cf
  name = G4_Cf
  specific = 4
FEATURE [App::DocumentObjectGroupPython] Element  # scripted group (container) (typed FeaturePython)
  Group = -> [G4_H,G4_He,G4_Li,G4_Be,G4_B,G4_C,G4_N,G4_O,G4_F,G4_Ne,G4_Na,G4_Mg,G4_Al,G4_Si,G4_P,G4_S,G4_Cl,G4_Ar,G4_K,G4_Ca,G4_Sc,G4_Ti,G4_V,G4_Cr,G4_Mn,G4_Fe,G4_Co,G4_Ni,G4_Cu,G4_Zn,G4_Ga,G4_Ge,G4_As,G4_Se,G4_Br,G4_Kr,G4_Rb,G4_Sr,G4_Y,G4_Zr,G4_Nb,G4_Mo,G4_Tc,G4_Ru,G4_Rh,G4_Pd,G4_Ag,G4_Cd,G4_In,G4_Sn,G4_Sb,G4_Te,G4_I,G4_Xe,G4_Cs,G4_Ba,G4_La,G4_Ce,G4_Pr,G4_Nd,G4_Pm,G4_Sm,G4_Eu,G4_Gd,G4_Tb,G4_Dy,G4_Ho,G4_Er,+30 more]
FEATURE [App::DocumentObjectGroupPython] H_element114  label="H_element : 063"  # scripted group (container) (typed FeaturePython)
  n = 2
  ref = H_element
FEATURE [App::DocumentObjectGroupPython] G4_lH2  # scripted group (container) (typed FeaturePython)
  Dunit = g/cm3
  Dvalue = 0.0708
  Group = -> [H_element114]
  conduct = 2
  density = 1
  expand = 3
  formula = G4_lH2
  name = G4_lH2
  specific = 4
FEATURE [App::DocumentObjectGroupPython] N_element049  label="N_element : 022"  # scripted group (container) (typed FeaturePython)
  n = 2
  ref = N_element
FEATURE [App::DocumentObjectGroupPython] G4_lN2  # scripted group (container) (typed FeaturePython)
  Dunit = g/cm3
  Dvalue = 0.807
  Group = -> [N_element049]
  conduct = 2
  density = 1
  expand = 3
  formula = G4_lN2
  name = G4_lN2
  specific = 4
FEATURE [App::DocumentObjectGroupPython] O_element106  label="O_element : 060"  # scripted group (container) (typed FeaturePython)
  n = 2
  ref = O_element
FEATURE [App::DocumentObjectGroupPython] G4_lO2  # scripted group (container) (typed FeaturePython)
  Dunit = g/cm3
  Dvalue = 1.141
  Group = -> [O_element106]
  conduct = 2
  density = 1
  expand = 3
  formula = G4_lO2
  name = G4_lO2
  specific = 4
FEATURE [App::DocumentObjectGroupPython] Ar_element003  label="Ar_element : 002"  # scripted group (container) (typed FeaturePython)
  n = 1
  ref = Ar_element
FEATURE [App::DocumentObjectGroupPython] G4_lAr  # scripted group (container) (typed FeaturePython)
  Dunit = g/cm3
  Dvalue = 1.396
  Group = -> [Ar_element003]
  conduct = 2
  density = 1
  expand = 3
  formula = G4_lAr
  name = G4_lAr
  specific = 4
FEATURE [App::DocumentObjectGroupPython] Br_element008  label="Br_element : 005"  # scripted group (container) (typed FeaturePython)
  n = 1
  ref = Br_element
FEATURE [App::DocumentObjectGroupPython] G4_lBr  # scripted group (container) (typed FeaturePython)
  Dunit = g/cm3
  Dvalue = 3.1028
  Group = -> [Br_element008]
  conduct = 2
  density = 1
  expand = 3
  formula = G4_lBr
  name = G4_lBr
  specific = 4
FEATURE [App::DocumentObjectGroupPython] Kr_element002  label="Kr_element : 002"  # scripted group (container) (typed FeaturePython)
  n = 1
  ref = Kr_element
FEATURE [App::DocumentObjectGroupPython] G4_lKr  # scripted group (container) (typed FeaturePython)
  Dunit = g/cm3
  Dvalue = 2.418
  Group = -> [Kr_element002]
  conduct = 2
  density = 1
  expand = 3
  formula = G4_lKr
  name = G4_lKr
  specific = 4
FEATURE [App::DocumentObjectGroupPython] Xe_element002  label="Xe_element : 002"  # scripted group (container) (typed FeaturePython)
  n = 1
  ref = Xe_element
FEATURE [App::DocumentObjectGroupPython] G4_lXe  # scripted group (container) (typed FeaturePython)
  Dunit = g/cm3
  Dvalue = 2.953
  Group = -> [Xe_element002]
  conduct = 2
  density = 1
  expand = 3
  formula = G4_lXe
  name = G4_lXe
  specific = 4
FEATURE [App::DocumentObjectGroupPython] O_element107  label="O_element : 061"  # scripted group (container) (typed FeaturePython)
  n = 4
  ref = O_element
FEATURE [App::DocumentObjectGroupPython] Pb_element004  label="Pb_element : 002"  # scripted group (container) (typed FeaturePython)
  n = 1
  ref = Pb_element
FEATURE [App::DocumentObjectGroupPython] W_element005  label="W_element : 005"  # scripted group (container) (typed FeaturePython)
  n = 1
  ref = W_element
FEATURE [App::DocumentObjectGroupPython] G4_PbWO4  # scripted group (container) (typed FeaturePython)
  Dunit = g/cm3
  Dvalue = 8.28
  Group = -> [O_element107,Pb_element004,W_element005]
  conduct = 2
  density = 1
  expand = 3
  formula = G4_PbWO4
  name = G4_PbWO4
  specific = 4
FEATURE [App::DocumentObjectGroupPython] H_element115  label="H_element : 064"  # scripted group (container) (typed FeaturePython)
  n = 1
  ref = H_element
FEATURE [App::DocumentObjectGroupPython] G4_Galactic  # scripted group (container) (typed FeaturePython)
  Dunit = g/cm3
  Dvalue = 0
  Group = -> [H_element115]
  conduct = 2
  density = 1
  expand = 3
  formula = G4_Galactic
  name = G4_Galactic
  specific = 4
FEATURE [App::DocumentObjectGroupPython] C_element125  label="C_element : 071"  # scripted group (container) (typed FeaturePython)
  n = 1
  ref = C_element
FEATURE [App::DocumentObjectGroupPython] G4_GRAPHITE_POROUS  # scripted group (container) (typed FeaturePython)
  Dunit = g/cm3
  Dvalue = 1.7
  Group = -> [C_element125]
  conduct = 2
  density = 1
  expand = 3
  formula = G4_GRAPHITE_POROUS
  name = G4_GRAPHITE_POROUS
  specific = 4
FEATURE [App::DocumentObjectGroupPython] H_element116  label="H_element : 0.150"  # scripted group (container) (typed FeaturePython)
  n = 0.080538
FEATURE [App::DocumentObjectGroupPython] C_element126  label="C_element : 0.600"  # scripted group (container) (typed FeaturePython)
  n = 0.599848
FEATURE [App::DocumentObjectGroupPython] O_element108  label="O_element : 0.320"  # scripted group (container) (typed FeaturePython)
  n = 0.319614
FEATURE [App::DocumentObjectGroupPython] G4_LUCITE  # scripted group (container) (typed FeaturePython)
  Dunit = g/cm3
  Dvalue = 1.19
  Group = -> [H_element116,C_element126,O_element108]
  conduct = 2
  density = 1
  expand = 3
  formula = G4_LUCITE
  name = G4_LUCITE
  specific = 4
FEATURE [App::DocumentObjectGroupPython] Cu_element002  label="Cu_element : 62"  # scripted group (container) (typed FeaturePython)
  n = 62
  ref = Cu_element
FEATURE [App::DocumentObjectGroupPython] Zn_element002  label="Zn_element : 35"  # scripted group (container) (typed FeaturePython)
  n = 35
  ref = Zn_element
FEATURE [App::DocumentObjectGroupPython] Pb_element005  label="Pb_element : 3"  # scripted group (container) (typed FeaturePython)
  n = 3
  ref = Pb_element
FEATURE [App::DocumentObjectGroupPython] G4_BRASS  # scripted group (container) (typed FeaturePython)
  Dunit = g/cm3
  Dvalue = 8.52
  Group = -> [Cu_element002,Zn_element002,Pb_element005]
  conduct = 2
  density = 1
  expand = 3
  formula = G4_BRASS
  name = G4_BRASS
  specific = 4
FEATURE [App::DocumentObjectGroupPython] Cu_element003  label="Cu_element : 89"  # scripted group (container) (typed FeaturePython)
  n = 89
  ref = Cu_element
FEATURE [App::DocumentObjectGroupPython] Zn_element003  label="Zn_element : 9"  # scripted group (container) (typed FeaturePython)
  n = 9
  ref = Zn_element
FEATURE [App::DocumentObjectGroupPython] Pb_element006  label="Pb_element : 2"  # scripted group (container) (typed FeaturePython)
  n = 2
  ref = Pb_element
FEATURE [App::DocumentObjectGroupPython] G4_BRONZE  # scripted group (container) (typed FeaturePython)
  Dunit = g/cm3
  Dvalue = 8.82
  Group = -> [Cu_element003,Zn_element003,Pb_element006]
  conduct = 2
  density = 1
  expand = 3
  formula = G4_BRONZE
  name = G4_BRONZE
  specific = 4
FEATURE [App::DocumentObjectGroupPython] Fe_element008  label="Fe_element : 74"  # scripted group (container) (typed FeaturePython)
  n = 74
  ref = Fe_element
FEATURE [App::DocumentObjectGroupPython] Cr_element002  label="Cr_element : 18"  # scripted group (container) (typed FeaturePython)
  n = 18
  ref = Cr_element
FEATURE [App::DocumentObjectGroupPython] Ni_element002  label="Ni_element : 8"  # scripted group (container) (typed FeaturePython)
  n = 8
  ref = Ni_element
FEATURE [App::DocumentObjectGroupPython] G4_STAINLESS_STEEL  label="G4_STAINLESS-STEEL"  # scripted group (container) (typed FeaturePython)
  Dunit = g/cm3
  Dvalue = 8
  Group = -> [Fe_element008,Cr_element002,Ni_element002]
  conduct = 2
  density = 1
  expand = 3
  formula = G4_STAINLESS-STEEL
  name = G4_STAINLESS-STEEL
  specific = 4
FEATURE [App::DocumentObjectGroupPython] H_element117  label="H_element : 065"  # scripted group (container) (typed FeaturePython)
  n = 18
  ref = H_element
FEATURE [App::DocumentObjectGroupPython] C_element127  label="C_element : 072"  # scripted group (container) (typed FeaturePython)
  n = 12
  ref = C_element
FEATURE [App::DocumentObjectGroupPython] O_element109  label="O_element : 062"  # scripted group (container) (typed FeaturePython)
  n = 7
  ref = O_element
FEATURE [App::DocumentObjectGroupPython] G4_CR39  # scripted group (container) (typed FeaturePython)
  Dunit = g/cm3
  Dvalue = 1.32
  Group = -> [H_element117,C_element127,O_element109]
  conduct = 2
  density = 1
  expand = 3
  formula = G4_CR39
  name = G4_CR39
  specific = 4
FEATURE [App::DocumentObjectGroupPython] H_element118  label="H_element : 38"  # scripted group (container) (typed FeaturePython)
  n = 38
  ref = H_element
FEATURE [App::DocumentObjectGroupPython] C_element128  label="C_element : 073"  # scripted group (container) (typed FeaturePython)
  n = 18
  ref = C_element
FEATURE [App::DocumentObjectGroupPython] O_element110  label="O_element : 063"  # scripted group (container) (typed FeaturePython)
  n = 1
  ref = O_element
FEATURE [App::DocumentObjectGroupPython] G4_OCTADECANOL  # scripted group (container) (typed FeaturePython)
  Dunit = g/cm3
  Dvalue = 0.812
  Group = -> [H_element118,C_element128,O_element110]
  conduct = 2
  density = 1
  expand = 3
  formula = G4_OCTADECANOL
  name = G4_OCTADECANOL
  specific = 4
FEATURE [App::DocumentObjectGroupPython] HEP  # scripted group (container) (typed FeaturePython)
  Group = -> [G4_lH2,G4_lN2,G4_lO2,G4_lAr,G4_lBr,G4_lKr,G4_lXe,G4_PbWO4,G4_Galactic,G4_GRAPHITE_POROUS,G4_LUCITE,G4_BRASS,G4_BRONZE,G4_STAINLESS_STEEL,G4_CR39,G4_OCTADECANOL]
FEATURE [App::DocumentObjectGroupPython] C_element129  label="C_element : 074"  # scripted group (container) (typed FeaturePython)
  n = 14
  ref = C_element
FEATURE [App::DocumentObjectGroupPython] H_element119  label="H_element : 066"  # scripted group (container) (typed FeaturePython)
  n = 10
  ref = H_element
FEATURE [App::DocumentObjectGroupPython] O_element111  label="O_element : 064"  # scripted group (container) (typed FeaturePython)
  n = 2
  ref = O_element
FEATURE [App::DocumentObjectGroupPython] N_element050  label="N_element : 023"  # scripted group (container) (typed FeaturePython)
  n = 2
  ref = N_element
FEATURE [App::DocumentObjectGroupPython] G4_KEVLAR  # scripted group (container) (typed FeaturePython)
  Dunit = g/cm3
  Dvalue = 1.44
  Group = -> [C_element129,H_element119,O_element111,N_element050]
  conduct = 2
  density = 1
  expand = 3
  formula = G4_KEVLAR
  name = G4_KEVLAR
  specific = 4
FEATURE [App::DocumentObjectGroupPython] C_element130  label="C_element : 075"  # scripted group (container) (typed FeaturePython)
  n = 10
  ref = C_element
FEATURE [App::DocumentObjectGroupPython] H_element120  label="H_element : 067"  # scripted group (container) (typed FeaturePython)
  n = 8
  ref = H_element
FEATURE [App::DocumentObjectGroupPython] O_element112  label="O_element : 065"  # scripted group (container) (typed FeaturePython)
  n = 4
  ref = O_element
FEATURE [App::DocumentObjectGroupPython] G4_DACRON  # scripted group (container) (typed FeaturePython)
  Dunit = g/cm3
  Dvalue = 1.4
  Group = -> [C_element130,H_element120,O_element112]
  conduct = 2
  density = 1
  expand = 3
  formula = G4_DACRON
  name = G4_DACRON
  specific = 4
FEATURE [App::DocumentObjectGroupPython] C_element131  label="C_element : 076"  # scripted group (container) (typed FeaturePython)
  n = 4
  ref = C_element
FEATURE [App::DocumentObjectGroupPython] H_element121  label="H_element : 068"  # scripted group (container) (typed FeaturePython)
  n = 5
  ref = H_element
FEATURE [App::DocumentObjectGroupPython] Cl_element030  label="Cl_element : 016"  # scripted group (container) (typed FeaturePython)
  n = 1
  ref = Cl_element
FEATURE [App::DocumentObjectGroupPython] G4_NEOPRENE  # scripted group (container) (typed FeaturePython)
  Dunit = g/cm3
  Dvalue = 1.23
  Group = -> [C_element131,H_element121,Cl_element030]
  conduct = 2
  density = 1
  expand = 3
  formula = G4_NEOPRENE
  name = G4_NEOPRENE
  specific = 4
FEATURE [App::DocumentObjectGroupPython] Space  # scripted group (container) (typed FeaturePython)
  Group = -> [G4_KEVLAR,G4_DACRON,G4_NEOPRENE]
FEATURE [App::DocumentObjectGroupPython] H_element122  label="H_element : 069"  # scripted group (container) (typed FeaturePython)
  n = 5
  ref = H_element
FEATURE [App::DocumentObjectGroupPython] C_element132  label="C_element : 077"  # scripted group (container) (typed FeaturePython)
  n = 4
  ref = C_element
FEATURE [App::DocumentObjectGroupPython] N_element051  label="N_element : 3"  # scripted group (container) (typed FeaturePython)
  n = 3
  ref = N_element
FEATURE [App::DocumentObjectGroupPython] O_element113  label="O_element : 066"  # scripted group (container) (typed FeaturePython)
  n = 1
  ref = O_element
FEATURE [App::DocumentObjectGroupPython] G4_CYTOSINE  # scripted group (container) (typed FeaturePython)
  Dunit = g/cm3
  Dvalue = 1.55
  Group = -> [H_element122,C_element132,N_element051,O_element113]
  conduct = 2
  density = 1
  expand = 3
  formula = G4_CYTOSINE
  name = G4_CYTOSINE
  specific = 4
FEATURE [App::DocumentObjectGroupPython] H_element123  label="H_element : 070"  # scripted group (container) (typed FeaturePython)
  n = 6
  ref = H_element
FEATURE [App::DocumentObjectGroupPython] C_element133  label="C_element : 078"  # scripted group (container) (typed FeaturePython)
  n = 5
  ref = C_element
FEATURE [App::DocumentObjectGroupPython] N_element052  label="N_element : 024"  # scripted group (container) (typed FeaturePython)
  n = 2
  ref = N_element
FEATURE [App::DocumentObjectGroupPython] O_element114  label="O_element : 067"  # scripted group (container) (typed FeaturePython)
  n = 2
  ref = O_element
FEATURE [App::DocumentObjectGroupPython] G4_THYMINE  # scripted group (container) (typed FeaturePython)
  Dunit = g/cm3
  Dvalue = 1.23
  Group = -> [H_element123,C_element133,N_element052,O_element114]
  conduct = 2
  density = 1
  expand = 3
  formula = G4_THYMINE
  name = G4_THYMINE
  specific = 4
FEATURE [App::DocumentObjectGroupPython] H_element124  label="H_element : 071"  # scripted group (container) (typed FeaturePython)
  n = 4
  ref = H_element
FEATURE [App::DocumentObjectGroupPython] C_element134  label="C_element : 079"  # scripted group (container) (typed FeaturePython)
  n = 4
  ref = C_element
FEATURE [App::DocumentObjectGroupPython] N_element053  label="N_element : 025"  # scripted group (container) (typed FeaturePython)
  n = 2
  ref = N_element
FEATURE [App::DocumentObjectGroupPython] O_element115  label="O_element : 068"  # scripted group (container) (typed FeaturePython)
  n = 2
  ref = O_element
FEATURE [App::DocumentObjectGroupPython] G4_URACIL  # scripted group (container) (typed FeaturePython)
  Dunit = g/cm3
  Dvalue = 1.32
  Group = -> [H_element124,C_element134,N_element053,O_element115]
  conduct = 2
  density = 1
  expand = 3
  formula = G4_URACIL
  name = G4_URACIL
  specific = 4
FEATURE [App::DocumentObjectGroupPython] H_element125  label="H_element : 072"  # scripted group (container) (typed FeaturePython)
  n = 4
  ref = H_element
FEATURE [App::DocumentObjectGroupPython] C_element135  label="C_element : 080"  # scripted group (container) (typed FeaturePython)
  n = 5
  ref = C_element
FEATURE [App::DocumentObjectGroupPython] N_element054  label="N_element : 026"  # scripted group (container) (typed FeaturePython)
  n = 5
  ref = N_element
FEATURE [App::DocumentObjectGroupPython] G4_DNA_ADENINE  # scripted group (container) (typed FeaturePython)
  Dunit = g/cm3
  Dvalue = 1
  Group = -> [H_element125,C_element135,N_element054]
  conduct = 2
  density = 1
  expand = 3
  formula = G4_DNA_ADENINE
  name = G4_DNA_ADENINE
  specific = 4
FEATURE [App::DocumentObjectGroupPython] H_element126  label="H_element : 073"  # scripted group (container) (typed FeaturePython)
  n = 4
  ref = H_element
FEATURE [App::DocumentObjectGroupPython] C_element136  label="C_element : 081"  # scripted group (container) (typed FeaturePython)
  n = 5
  ref = C_element
FEATURE [App::DocumentObjectGroupPython] N_element055  label="N_element : 027"  # scripted group (container) (typed FeaturePython)
  n = 5
  ref = N_element
FEATURE [App::DocumentObjectGroupPython] O_element116  label="O_element : 069"  # scripted group (container) (typed FeaturePython)
  n = 1
  ref = O_element
FEATURE [App::DocumentObjectGroupPython] G4_DNA_GUANINE  # scripted group (container) (typed FeaturePython)
  Dunit = g/cm3
  Dvalue = 1
  Group = -> [H_element126,C_element136,N_element055,O_element116]
  conduct = 2
  density = 1
  expand = 3
  formula = G4_DNA_GUANINE
  name = G4_DNA_GUANINE
  specific = 4
FEATURE [App::DocumentObjectGroupPython] H_element127  label="H_element : 074"  # scripted group (container) (typed FeaturePython)
  n = 4
  ref = H_element
FEATURE [App::DocumentObjectGroupPython] C_element137  label="C_element : 082"  # scripted group (container) (typed FeaturePython)
  n = 4
  ref = C_element
FEATURE [App::DocumentObjectGroupPython] N_element056  label="N_element : 028"  # scripted group (container) (typed FeaturePython)
  n = 3
  ref = N_element
FEATURE [App::DocumentObjectGroupPython] O_element117  label="O_element : 070"  # scripted group (container) (typed FeaturePython)
  n = 1
  ref = O_element
FEATURE [App::DocumentObjectGroupPython] G4_DNA_CYTOSINE  # scripted group (container) (typed FeaturePython)
  Dunit = g/cm3
  Dvalue = 1
  Group = -> [H_element127,C_element137,N_element056,O_element117]
  conduct = 2
  density = 1
  expand = 3
  formula = G4_DNA_CYTOSINE
  name = G4_DNA_CYTOSINE
  specific = 4
FEATURE [App::DocumentObjectGroupPython] H_element128  label="H_element : 075"  # scripted group (container) (typed FeaturePython)
  n = 5
  ref = H_element
FEATURE [App::DocumentObjectGroupPython] C_element138  label="C_element : 083"  # scripted group (container) (typed FeaturePython)
  n = 5
  ref = C_element
FEATURE [App::DocumentObjectGroupPython] N_element057  label="N_element : 029"  # scripted group (container) (typed FeaturePython)
  n = 2
  ref = N_element
FEATURE [App::DocumentObjectGroupPython] O_element118  label="O_element : 071"  # scripted group (container) (typed FeaturePython)
  n = 2
  ref = O_element
FEATURE [App::DocumentObjectGroupPython] G4_DNA_THYMINE  # scripted group (container) (typed FeaturePython)
  Dunit = g/cm3
  Dvalue = 1
  Group = -> [H_element128,C_element138,N_element057,O_element118]
  conduct = 2
  density = 1
  expand = 3
  formula = G4_DNA_THYMINE
  name = G4_DNA_THYMINE
  specific = 4
FEATURE [App::DocumentObjectGroupPython] H_element129  label="H_element : 076"  # scripted group (container) (typed FeaturePython)
  n = 3
  ref = H_element
FEATURE [App::DocumentObjectGroupPython] C_element139  label="C_element : 084"  # scripted group (container) (typed FeaturePython)
  n = 4
  ref = C_element
FEATURE [App::DocumentObjectGroupPython] N_element058  label="N_element : 030"  # scripted group (container) (typed FeaturePython)
  n = 2
  ref = N_element
FEATURE [App::DocumentObjectGroupPython] O_element119  label="O_element : 072"  # scripted group (container) (typed FeaturePython)
  n = 2
  ref = O_element
FEATURE [App::DocumentObjectGroupPython] G4_DNA_URACIL  # scripted group (container) (typed FeaturePython)
  Dunit = g/cm3
  Dvalue = 1
  Group = -> [H_element129,C_element139,N_element058,O_element119]
  conduct = 2
  density = 1
  expand = 3
  formula = G4_DNA_URACIL
  name = G4_DNA_URACIL
  specific = 4
FEATURE [App::DocumentObjectGroupPython] H_element130  label="H_element : 077"  # scripted group (container) (typed FeaturePython)
  n = 10
  ref = H_element
FEATURE [App::DocumentObjectGroupPython] C_element140  label="C_element : 085"  # scripted group (container) (typed FeaturePython)
  n = 10
  ref = C_element
FEATURE [App::DocumentObjectGroupPython] N_element059  label="N_element : 031"  # scripted group (container) (typed FeaturePython)
  n = 5
  ref = N_element
FEATURE [App::DocumentObjectGroupPython] O_element120  label="O_element : 073"  # scripted group (container) (typed FeaturePython)
  n = 4
  ref = O_element
FEATURE [App::DocumentObjectGroupPython] G4_DNA_ADENOSINE  # scripted group (container) (typed FeaturePython)
  Dunit = g/cm3
  Dvalue = 1
  Group = -> [H_element130,C_element140,N_element059,O_element120]
  conduct = 2
  density = 1
  expand = 3
  formula = G4_DNA_ADENOSINE
  name = G4_DNA_ADENOSINE
  specific = 4
FEATURE [App::DocumentObjectGroupPython] H_element131  label="H_element : 078"  # scripted group (container) (typed FeaturePython)
  n = 10
  ref = H_element
FEATURE [App::DocumentObjectGroupPython] C_element141  label="C_element : 086"  # scripted group (container) (typed FeaturePython)
  n = 10
  ref = C_element
FEATURE [App::DocumentObjectGroupPython] N_element060  label="N_element : 032"  # scripted group (container) (typed FeaturePython)
  n = 5
  ref = N_element
FEATURE [App::DocumentObjectGroupPython] O_element121  label="O_element : 074"  # scripted group (container) (typed FeaturePython)
  n = 5
  ref = O_element
FEATURE [App::DocumentObjectGroupPython] G4_DNA_GUANOSINE  # scripted group (container) (typed FeaturePython)
  Dunit = g/cm3
  Dvalue = 1
  Group = -> [H_element131,C_element141,N_element060,O_element121]
  conduct = 2
  density = 1
  expand = 3
  formula = G4_DNA_GUANOSINE
  name = G4_DNA_GUANOSINE
  specific = 4
FEATURE [App::DocumentObjectGroupPython] H_element132  label="H_element : 079"  # scripted group (container) (typed FeaturePython)
  n = 10
  ref = H_element
FEATURE [App::DocumentObjectGroupPython] C_element142  label="C_element : 087"  # scripted group (container) (typed FeaturePython)
  n = 9
  ref = C_element
FEATURE [App::DocumentObjectGroupPython] N_element061  label="N_element : 033"  # scripted group (container) (typed FeaturePython)
  n = 3
  ref = N_element
FEATURE [App::DocumentObjectGroupPython] O_element122  label="O_element : 075"  # scripted group (container) (typed FeaturePython)
  n = 5
  ref = O_element
FEATURE [App::DocumentObjectGroupPython] G4_DNA_CYTIDINE  # scripted group (container) (typed FeaturePython)
  Dunit = g/cm3
  Dvalue = 1
  Group = -> [H_element132,C_element142,N_element061,O_element122]
  conduct = 2
  density = 1
  expand = 3
  formula = G4_DNA_CYTIDINE
  name = G4_DNA_CYTIDINE
  specific = 4
FEATURE [App::DocumentObjectGroupPython] H_element133  label="H_element : 080"  # scripted group (container) (typed FeaturePython)
  n = 9
  ref = H_element
FEATURE [App::DocumentObjectGroupPython] C_element143  label="C_element : 088"  # scripted group (container) (typed FeaturePython)
  n = 9
  ref = C_element
FEATURE [App::DocumentObjectGroupPython] N_element062  label="N_element : 034"  # scripted group (container) (typed FeaturePython)
  n = 2
  ref = N_element
FEATURE [App::DocumentObjectGroupPython] O_element123  label="O_element : 076"  # scripted group (container) (typed FeaturePython)
  n = 6
  ref = O_element
FEATURE [App::DocumentObjectGroupPython] G4_DNA_URIDINE  # scripted group (container) (typed FeaturePython)
  Dunit = g/cm3
  Dvalue = 1
  Group = -> [H_element133,C_element143,N_element062,O_element123]
  conduct = 2
  density = 1
  expand = 3
  formula = G4_DNA_URIDINE
  name = G4_DNA_URIDINE
  specific = 4
FEATURE [App::DocumentObjectGroupPython] H_element134  label="H_element : 081"  # scripted group (container) (typed FeaturePython)
  n = 11
  ref = H_element
FEATURE [App::DocumentObjectGroupPython] C_element144  label="C_element : 089"  # scripted group (container) (typed FeaturePython)
  n = 10
  ref = C_element
FEATURE [App::DocumentObjectGroupPython] N_element063  label="N_element : 035"  # scripted group (container) (typed FeaturePython)
  n = 2
  ref = N_element
FEATURE [App::DocumentObjectGroupPython] O_element124  label="O_element : 077"  # scripted group (container) (typed FeaturePython)
  n = 6
  ref = O_element
FEATURE [App::DocumentObjectGroupPython] G4_DNA_METHYLURIDINE  # scripted group (container) (typed FeaturePython)
  Dunit = g/cm3
  Dvalue = 1
  Group = -> [H_element134,C_element144,N_element063,O_element124]
  conduct = 2
  density = 1
  expand = 3
  formula = G4_DNA_METHYLURIDINE
  name = G4_DNA_METHYLURIDINE
  specific = 4
FEATURE [App::DocumentObjectGroupPython] P_element014  label="P_element : 003"  # scripted group (container) (typed FeaturePython)
  n = 1
  ref = P_element
FEATURE [App::DocumentObjectGroupPython] O_element125  label="O_element : 078"  # scripted group (container) (typed FeaturePython)
  n = 3
  ref = O_element
FEATURE [App::DocumentObjectGroupPython] G4_DNA_MONOPHOSPHATE  # scripted group (container) (typed FeaturePython)
  Dunit = g/cm3
  Dvalue = 1
  Group = -> [P_element014,O_element125]
  conduct = 2
  density = 1
  expand = 3
  formula = G4_DNA_MONOPHOSPHATE
  name = G4_DNA_MONOPHOSPHATE
  specific = 4
FEATURE [App::DocumentObjectGroupPython] H_element135  label="H_element : 082"  # scripted group (container) (typed FeaturePython)
  n = 10
  ref = H_element
FEATURE [App::DocumentObjectGroupPython] C_element145  label="C_element : 090"  # scripted group (container) (typed FeaturePython)
  n = 10
  ref = C_element
FEATURE [App::DocumentObjectGroupPython] N_element064  label="N_element : 036"  # scripted group (container) (typed FeaturePython)
  n = 5
  ref = N_element
FEATURE [App::DocumentObjectGroupPython] O_element126  label="O_element : 079"  # scripted group (container) (typed FeaturePython)
  n = 7
  ref = O_element
FEATURE [App::DocumentObjectGroupPython] P_element015  label="P_element : 004"  # scripted group (container) (typed FeaturePython)
  n = 1
  ref = P_element
FEATURE [App::DocumentObjectGroupPython] G4_DNA_A  # scripted group (container) (typed FeaturePython)
  Dunit = g/cm3
  Dvalue = 1
  Group = -> [H_element135,C_element145,N_element064,O_element126,P_element015]
  conduct = 2
  density = 1
  expand = 3
  formula = G4_DNA_A
  name = G4_DNA_A
  specific = 4
FEATURE [App::DocumentObjectGroupPython] H_element136  label="H_element : 083"  # scripted group (container) (typed FeaturePython)
  n = 10
  ref = H_element
FEATURE [App::DocumentObjectGroupPython] C_element146  label="C_element : 091"  # scripted group (container) (typed FeaturePython)
  n = 10
  ref = C_element
FEATURE [App::DocumentObjectGroupPython] N_element065  label="N_element : 037"  # scripted group (container) (typed FeaturePython)
  n = 5
  ref = N_element
FEATURE [App::DocumentObjectGroupPython] O_element127  label="O_element : 8"  # scripted group (container) (typed FeaturePython)
  n = 8
  ref = O_element
FEATURE [App::DocumentObjectGroupPython] P_element016  label="P_element : 005"  # scripted group (container) (typed FeaturePython)
  n = 1
  ref = P_element
FEATURE [App::DocumentObjectGroupPython] G4_DNA_G  # scripted group (container) (typed FeaturePython)
  Dunit = g/cm3
  Dvalue = 1
  Group = -> [H_element136,C_element146,N_element065,O_element127,P_element016]
  conduct = 2
  density = 1
  expand = 3
  formula = G4_DNA_G
  name = G4_DNA_G
  specific = 4
FEATURE [App::DocumentObjectGroupPython] H_element137  label="H_element : 084"  # scripted group (container) (typed FeaturePython)
  n = 10
  ref = H_element
FEATURE [App::DocumentObjectGroupPython] C_element147  label="C_element : 092"  # scripted group (container) (typed FeaturePython)
  n = 9
  ref = C_element
FEATURE [App::DocumentObjectGroupPython] N_element066  label="N_element : 038"  # scripted group (container) (typed FeaturePython)
  n = 3
  ref = N_element
FEATURE [App::DocumentObjectGroupPython] O_element128  label="O_element : 080"  # scripted group (container) (typed FeaturePython)
  n = 8
  ref = O_element
FEATURE [App::DocumentObjectGroupPython] P_element017  label="P_element : 006"  # scripted group (container) (typed FeaturePython)
  n = 1
  ref = P_element
FEATURE [App::DocumentObjectGroupPython] G4_DNA_C  # scripted group (container) (typed FeaturePython)
  Dunit = g/cm3
  Dvalue = 1
  Group = -> [H_element137,C_element147,N_element066,O_element128,P_element017]
  conduct = 2
  density = 1
  expand = 3
  formula = G4_DNA_C
  name = G4_DNA_C
  specific = 4
FEATURE [App::DocumentObjectGroupPython] H_element138  label="H_element : 085"  # scripted group (container) (typed FeaturePython)
  n = 9
  ref = H_element
FEATURE [App::DocumentObjectGroupPython] C_element148  label="C_element : 093"  # scripted group (container) (typed FeaturePython)
  n = 9
  ref = C_element
FEATURE [App::DocumentObjectGroupPython] N_element067  label="N_element : 039"  # scripted group (container) (typed FeaturePython)
  n = 2
  ref = N_element
FEATURE [App::DocumentObjectGroupPython] O_element129  label="O_element : 9"  # scripted group (container) (typed FeaturePython)
  n = 9
  ref = O_element
FEATURE [App::DocumentObjectGroupPython] P_element018  label="P_element : 007"  # scripted group (container) (typed FeaturePython)
  n = 1
  ref = P_element
FEATURE [App::DocumentObjectGroupPython] G4_DNA_U  # scripted group (container) (typed FeaturePython)
  Dunit = g/cm3
  Dvalue = 1
  Group = -> [H_element138,C_element148,N_element067,O_element129,P_element018]
  conduct = 2
  density = 1
  expand = 3
  formula = G4_DNA_U
  name = G4_DNA_U
  specific = 4
FEATURE [App::DocumentObjectGroupPython] H_element139  label="H_element : 086"  # scripted group (container) (typed FeaturePython)
  n = 11
  ref = H_element
FEATURE [App::DocumentObjectGroupPython] C_element149  label="C_element : 094"  # scripted group (container) (typed FeaturePython)
  n = 10
  ref = C_element
FEATURE [App::DocumentObjectGroupPython] N_element068  label="N_element : 040"  # scripted group (container) (typed FeaturePython)
  n = 2
  ref = N_element
FEATURE [App::DocumentObjectGroupPython] O_element130  label="O_element : 081"  # scripted group (container) (typed FeaturePython)
  n = 9
  ref = O_element
FEATURE [App::DocumentObjectGroupPython] P_element019  label="P_element : 008"  # scripted group (container) (typed FeaturePython)
  n = 1
  ref = P_element
FEATURE [App::DocumentObjectGroupPython] G4_DNA_MU  # scripted group (container) (typed FeaturePython)
  Dunit = g/cm3
  Dvalue = 1
  Group = -> [H_element139,C_element149,N_element068,O_element130,P_element019]
  conduct = 2
  density = 1
  expand = 3
  formula = G4_DNA_MU
  name = G4_DNA_MU
  specific = 4
FEATURE [App::DocumentObjectGroupPython] BioChemical  # scripted group (container) (typed FeaturePython)
  Group = -> [G4_CYTOSINE,G4_THYMINE,G4_URACIL,G4_DNA_ADENINE,G4_DNA_GUANINE,G4_DNA_CYTOSINE,G4_DNA_THYMINE,G4_DNA_URACIL,G4_DNA_ADENOSINE,G4_DNA_GUANOSINE,G4_DNA_CYTIDINE,G4_DNA_URIDINE,G4_DNA_METHYLURIDINE,G4_DNA_MONOPHOSPHATE,G4_DNA_A,G4_DNA_G,G4_DNA_C,G4_DNA_U,G4_DNA_MU]
FEATURE [App::DocumentObjectGroupPython] G4Materials  # scripted group (container) (typed FeaturePython)
  Group = -> [NIST,Element,HEP,Space,BioChemical]
  version = 1
FEATURE [App::DocumentObjectGroupPython] Geant4  # scripted group (container) (typed FeaturePython)
  Group = -> [G4Isotopes,G4Elements,G4Materials]
FEATURE [App::DocumentObjectGroupPython] Materials  # scripted group (container) (typed FeaturePython)
  Group = -> [Geant4]
FEATURE [Part::FeaturePython] GDMLBox_WorldBox  # WARN: FeaturePython — macro-defined, semantics opaque (R4)
  lunit = 2
  material = 5
  x = 260.26
  y = 182
  z = 169
FEATURE [Part::FeaturePython] GDMLBox_Box  # WARN: FeaturePython — macro-defined, semantics opaque (R4)
  Placement = pos=(30,0,0) rot=(0,0,1;0rad)
  lunit = 2
  material = 0
  x = 10
  y = 10
  z = 10
FEATURE [Part::FeaturePython] GDMLTorus  # WARN: FeaturePython — macro-defined, semantics opaque (R4)
  Placement = pos=(30,0,0) rot=(0,1,0;1.5708rad)
  aunit = deg
  deltaphi = 360
  lunit = 2
  material = 0
  rmax = 2
  rmin = 0
  rtor = 8
  startphi = 0
FEATURE [Part::MultiFuse] Fusion
  Placement = pos=(0,-25,0) rot=(0,0,1;0.523599rad)
  Shapes = -> [GDMLBox_Box,GDMLTorus]
FEATURE [Part::FeaturePython] Array  # Draft array (typed FeaturePython)
  AlwaysSyncPlacement = false
  Angle = 180
  ArrayType = 1
  Axis = (0,0,1)
  Base = -> Fusion
  Center = (0,0,0)
  Count = 5
  ExpandArray = false
  Fuse = false
  IntervalAxis = (0,0,0)
  IntervalX = (50,0,0)
  IntervalY = (0,50,0)
  IntervalZ = (0,0,50)
  NumberCircles = 3
  NumberPolar = 5
  NumberX = 2
  NumberY = 2
  NumberZ = 1
  Placement = pos=(42,35,0) rot=(0,0,1;0.785398rad)
  PlacementList = 5 placements: [(0,-25,0),(17.6777,-17.6777,0),(25,-5.55112e-15,0),(17.6777,17.6777,0),(3.06162e-15,25,0)]
  RadialDistance = 50
  ScaleList = (5) [(1,1,1),(1,1,1),(1,1,1),(1,1,1),(1,1,1)]
  Symmetry = 1
  TangentialDistance = 25
FEATURE [App::Part] Part001
  Group = -> [Array]
  Origin = -> Origin004
FEATURE [App::Part] worldVOL
  Group = -> [GDMLBox_WorldBox,Part001]
  Origin = -> Origin
